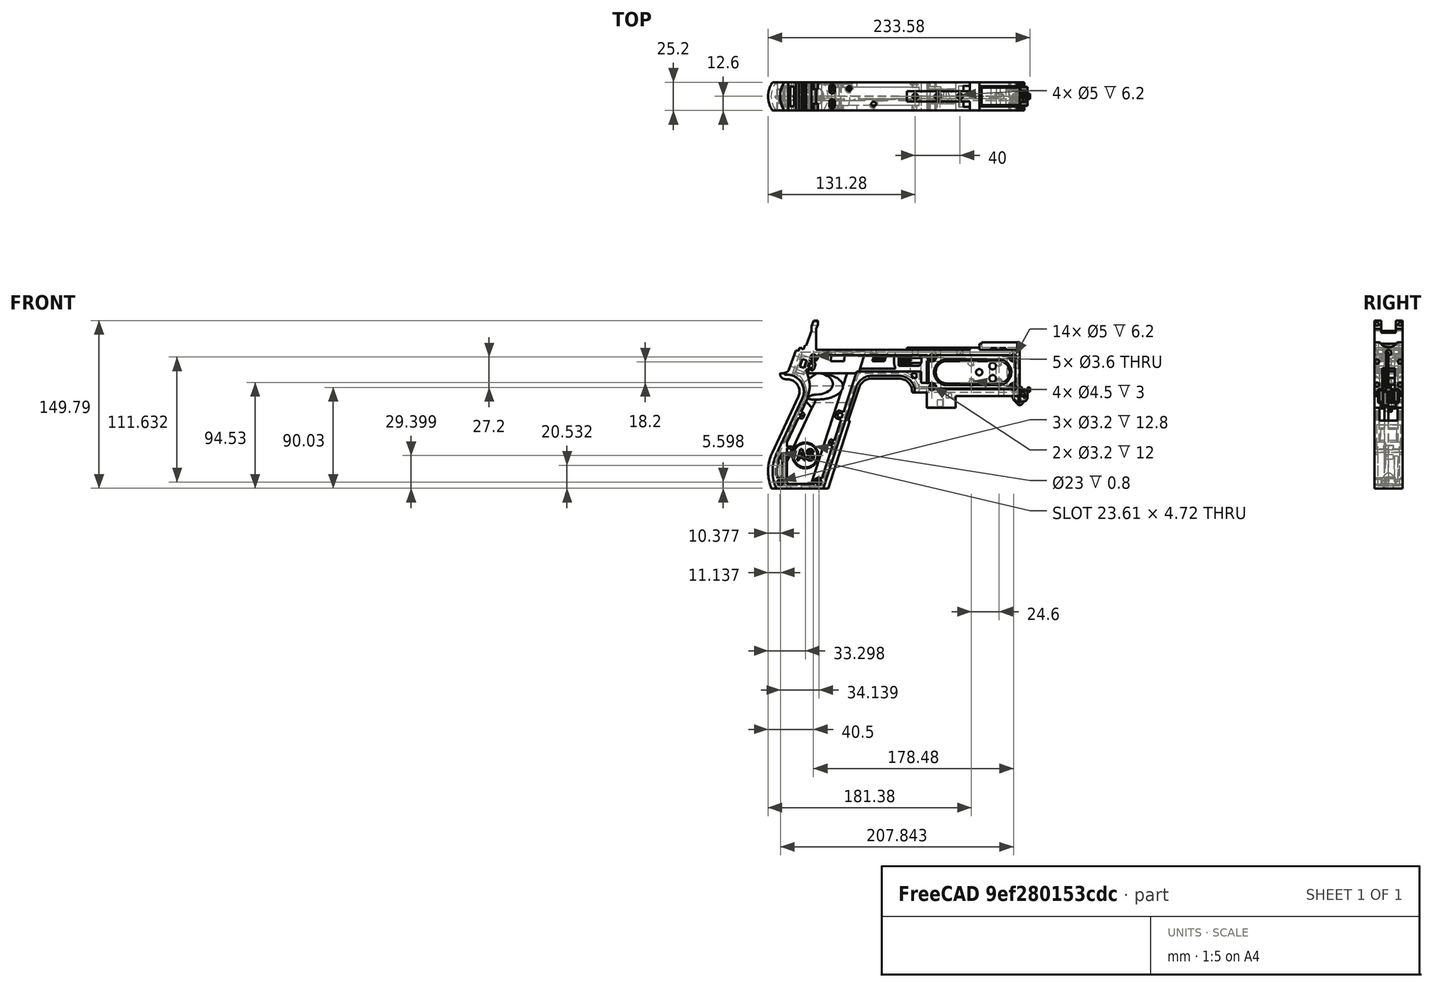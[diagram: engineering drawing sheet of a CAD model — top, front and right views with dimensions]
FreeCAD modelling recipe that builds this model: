
FCSTD DOCUMENT  (FreeCAD 1.0R39319 (Git))
Label: PICON-OF_ver_38
License: All rights reserved
LicenseURL: https://en.wikipedia.org/wiki/All_rights_reserved
objects: Sketcher::SketchObject×107, Part::Extrusion×50, Part::Cut×39, PartDesign::Pad×29, PartDesign::Pocket×18, PartDesign::Chamfer×15, PartDesign::Body×10, PartDesign::Fillet×6, PartDesign::SubtractivePipe×4, Part::Part2DObjectPython×4, PartDesign::SubtractiveLoft×4, PartDesign::Plane×2, PartDesign::SubShapeBinder×2, Part::Sweep×1, PartDesign::ShapeBinder×1, Part::MultiFuse×1, Mesh::Feature×1
note: 552 computed .brp shape members not serialized (recipe doc carries the construction recipe); baked Part::Feature solids carry a one-line shape summary decoded from their .brp

FEATURE [Sketcher::SketchObject] Sketch  label="corpo principale"
  ArcFitTolerance = 1e-06
  AttacherType = Attacher::AttachEngine3D
  AttachmentSupport = -> [XZ_Plane]
  FullyConstrained = true
  MakeInternals = false
  MapMode = 5
  Placement = pos=(0,0,0) rot=(1,0,0;1.5708rad)
  sketch-geometry (65):
    g0: LineSegment StartX=0 StartY=0 StartZ=0 EndX=-57.2 EndY=0 EndZ=0
    g1: LineSegment StartX=-57.2 StartY=0 StartZ=0 EndX=-57.2 EndY=-10.4 EndZ=0
    g2: LineSegment StartX=-57.2 StartY=-10.4 StartZ=0 EndX=-82.8 EndY=-10.4 EndZ=0
    g3: LineSegment StartX=-82.8 StartY=-10.4 StartZ=0 EndX=-82.8 EndY=3.2 EndZ=0
    g4: LineSegment StartX=-82.8 StartY=3.2 StartZ=0 EndX=-93.6 EndY=3.2 EndZ=0
    g5: LineSegment StartX=-93.6 StartY=3.2 StartZ=0 EndX=-93.6 EndY=4 EndZ=0
    g6: LineSegment StartX=-107.6 StartY=18 StartZ=0 EndX=-132.428 EndY=18 EndZ=0
    g7: LineSegment StartX=-145.743 StartY=8.32624 StartZ=0 EndX=-175.232 EndY=-82.4316 EndZ=0
    g8: LineSegment StartX=-175.232 StartY=-82.4316 StartZ=0 EndX=-217.232 EndY=-82.4316 EndZ=0
    g9: LineSegment StartX=-217.232 StartY=-52.1862 StartZ=0 EndX=-193.988 EndY=-2.33927 EndZ=0
    g10: LineSegment StartX=-206.196 StartY=23.0857 StartZ=0 EndX=-199.861 EndY=40.4914 EndZ=0
    g11: LineSegment StartX=-199.861 StartY=40.4914 StartZ=0 EndX=-197.061 EndY=40.4914 EndZ=0
    g12: LineSegment StartX=-197.061 StartY=40.4914 StartZ=0 EndX=-197.061 EndY=42.8914 EndZ=0
    g13: LineSegment StartX=-197.061 StartY=42.8914 StartZ=0 EndX=-194.261 EndY=42.8914 EndZ=0
    g14: LineSegment StartX=-194.261 StartY=42.8914 StartZ=0 EndX=-194.535 EndY=42.1397 EndZ=0
    g15: LineSegment StartX=-194.535 StartY=42.1397 StartZ=0 EndX=-193.031 EndY=41.5924 EndZ=0
    g16: LineSegment StartX=-193.031 StartY=41.5924 StartZ=0 EndX=-191.663 EndY=45.3512 EndZ=0
    g17: LineSegment StartX=-191.663 StartY=45.3512 StartZ=0 EndX=-190.536 EndY=44.9408 EndZ=0
    g18: LineSegment StartX=-190.536 StartY=44.9408 StartZ=0 EndX=-185.747 EndY=58.0965 EndZ=0
    g19: LineSegment StartX=-185.747 StartY=58.0965 StartZ=0 EndX=-185.747 EndY=62.0965 EndZ=0
    g20: LineSegment StartX=-185.747 StartY=62.0965 StartZ=0 EndX=-183.832 EndY=67.3588 EndZ=0
    g21: LineSegment StartX=-183.832 StartY=67.3588 StartZ=0 EndX=-180.232 EndY=67.3588 EndZ=0
    g22: LineSegment StartX=-180.232 StartY=67.3588 StartZ=0 EndX=-180.232 EndY=63.7588 EndZ=0
    g23: LineSegment StartX=-180.232 StartY=63.7588 StartZ=0 EndX=-181.6 EndY=60 EndZ=0
    g24: LineSegment StartX=-181.6 StartY=60 StartZ=0 EndX=-181.6 EndY=41.2 EndZ=0
    g25: LineSegment StartX=-181.6 StartY=41.2 StartZ=0 EndX=-100.8 EndY=41.2 EndZ=0
    g26: LineSegment StartX=-36 StartY=43.2 StartZ=0 EndX=-36 EndY=41.2 EndZ=0
    g27: LineSegment StartX=0 StartY=48 StartZ=0 EndX=0 EndY=0 EndZ=0
    g28: LineSegment StartX=-209.901 StartY=19.85 StartZ=0 EndX=-209.901 EndY=20.1 EndZ=0
    g29: LineSegment StartX=-208.001 StartY=22 StartZ=0 EndX=-207.747 EndY=22 EndZ=0
    g30: LineSegment StartX=-207.583 StartY=19 StartZ=0 EndX=-209.051 EndY=19 EndZ=0
    g31: ArcOfCircle CenterX=-208.001 CenterY=20.1 CenterZ=0 NormalX=0 NormalY=0 NormalZ=1 AngleXU=0 Radius=1.9 StartAngle=1.5708 EndAngle=3.14159
    g32: GeomPoint [constr] X=-209.901 Y=22 Z=0
    g33: ArcOfCircle CenterX=-209.051 CenterY=19.85 CenterZ=0 NormalX=0 NormalY=0 NormalZ=1 AngleXU=0 Radius=0.85 StartAngle=3.14159 EndAngle=4.71239
    g34: GeomPoint [constr] X=-209.901 Y=19 Z=0
    g35: ArcOfCircle CenterX=-207.747 CenterY=23.65 CenterZ=0 NormalX=0 NormalY=0 NormalZ=1 AngleXU=0 Radius=1.65 StartAngle=4.71239 EndAngle=5.93412
    g36: GeomPoint [constr] X=-206.591 Y=22 Z=0
    g37: LineSegment StartX=-4 StartY=6 StartZ=0 EndX=-4 EndY=36.4 EndZ=0
    g38: LineSegment StartX=-4 StartY=36.4 StartZ=0 EndX=-185.2 EndY=36.4 EndZ=0
    g39: LineSegment StartX=-185.2 StartY=36.4 StartZ=0 EndX=-190.441 EndY=22 EndZ=0
    g40: LineSegment StartX=-214.575 StartY=-78.4316 StartZ=0 EndX=-178.142 EndY=-78.4316 EndZ=0
    g41: LineSegment StartX=-178.142 StartY=-78.4316 StartZ=0 EndX=-145.51 EndY=22 EndZ=0
    g42: LineSegment StartX=-145.51 StartY=22 StartZ=0 EndX=-87.91 EndY=22 EndZ=0
    g43: LineSegment StartX=-87.91 StartY=22 StartZ=0 EndX=-87.91 EndY=11.6 EndZ=0
    g44: LineSegment StartX=-87.91 StartY=11.6 StartZ=0 EndX=-80.11 EndY=11.6 EndZ=0
    g45: LineSegment StartX=-80.11 StartY=11.6 StartZ=0 EndX=-80.11 EndY=6 EndZ=0
    g46: LineSegment StartX=-80.11 StartY=6 StartZ=0 EndX=-4 EndY=6 EndZ=0
    g47: LineSegment StartX=-190.363 StartY=-4.02975 StartZ=0 EndX=-213.607 EndY=-53.8767 EndZ=0
    g48: ArcOfCircle CenterX=-132.428 CenterY=4 CenterZ=0 NormalX=0 NormalY=0 NormalZ=1 AngleXU=0 Radius=14 StartAngle=1.5708 EndAngle=2.82743
    g49: GeomPoint [constr] X=-142.6 Y=18 Z=0
    g50: ArcOfCircle CenterX=-107.6 CenterY=4 CenterZ=0 NormalX=0 NormalY=0 NormalZ=1 AngleXU=0 Radius=14 StartAngle=0 EndAngle=1.5708
    g51: GeomPoint [constr] X=-93.6 Y=18 Z=0
    g52: ArcOfCircle CenterX=-184.801 CenterY=-67.3089 CenterZ=0 NormalX=0 NormalY=0 NormalZ=1 AngleXU=0 Radius=35.7833 StartAngle=2.70526 EndAngle=3.57792
    g53: ArcOfCircle CenterX=-207.583 CenterY=4 CenterZ=0 NormalX=0 NormalY=0 NormalZ=1 AngleXU=0 Radius=15 StartAngle=5.84685 EndAngle=7.85398
    g54: LineSegment [constr] StartX=-213.607 StartY=-53.8767 StartZ=0 EndX=-217.232 EndY=-52.1862 EndZ=0
    g55: ArcOfCircle CenterX=-184.801 CenterY=-67.3089 CenterZ=0 NormalX=0 NormalY=0 NormalZ=1 AngleXU=0 Radius=31.7833 StartAngle=2.70526 EndAngle=3.49911
    g56: ArcOfCircle CenterX=-218.095 CenterY=8.90192 CenterZ=0 NormalX=0 NormalY=0 NormalZ=1 AngleXU=0 Radius=30.5989 StartAngle=5.84685 EndAngle=6.72553
    g57: LineSegment StartX=-44.6 StartY=43.2 StartZ=0 EndX=-36 EndY=43.2 EndZ=0
    g58: LineSegment StartX=-100.8 StartY=41.2 StartZ=0 EndX=-44.6 EndY=41.2 EndZ=0
    g59: LineSegment StartX=-44.6 StartY=41.2 StartZ=0 EndX=-44.6 EndY=43.2 EndZ=0
    g60: LineSegment StartX=-2.4 StartY=48 StartZ=0 EndX=0 EndY=48 EndZ=0
    g61: LineSegment StartX=-36 StartY=41.2 StartZ=0 EndX=-2.4 EndY=41.2 EndZ=0
    g62: LineSegment StartX=-2.4 StartY=41.2 StartZ=0 EndX=-2.4 EndY=48 EndZ=0
    g63: LineSegment [constr] StartX=-181.6 StartY=36.4 StartZ=0 EndX=-152.209 EndY=36.4 EndZ=0
    g64: LineSegment [constr] StartX=-181.6 StartY=36.4 StartZ=0 EndX=-130.41 EndY=36.4 EndZ=0
  constraints (183):
    c: Coincident(g-1,g0)
    c: PointOnObject(g0,g-1)
    c: Coincident(g0,g1)
    c: Vertical(g1)
    c: Coincident(g1,g2)
    c: Horizontal(g2)
    c: Coincident(g2,g3)
    c: Vertical(g3)
    c: Coincident(g3,g4)
    c: Coincident(g4,g5)
    c: Vertical(g5)
    c: Horizontal(g6)
    c: Coincident(g7,g8)
    c: Horizontal(g8)
    c: Coincident(g10,g11)
    c: Horizontal(g11)
    c: Coincident(g11,g12)
    c: Vertical(g12)
    c: Coincident(g12,g13)
    c: Horizontal(g13)
    c: Coincident(g13,g14)
    c: Coincident(g14,g15)
    c: Coincident(g15,g16)
    c: Coincident(g16,g17)
    c: Coincident(g17,g18)
    c: Coincident(g18,g19)
    c: Vertical(g19)
    c: Coincident(g19,g20)
    c: Coincident(g20,g21)
    c: Horizontal(g21)
    c: Coincident(g21,g22)
    c: Vertical(g22)
    c: Coincident(g22,g23)
    c: Coincident(g23,g24)
    c: Vertical(g24)
    c: Coincident(g24,g25)
    c: Horizontal(g25)
    c: Coincident(g57,g26)
    c: Vertical(g26)
    c: Coincident(g26,g61)
    c: PointOnObject(g60,g-2)
    c: Coincident(g60,g27)
    c: Coincident(g27,g0)
    c: DistanceY(g27,g27) = 48
    c: DistanceY(g1,g1) = 10.4
    c: DistanceX(g0,g0) = 57.2
    c: DistanceX(g2,g2) = 25.6
    c: Horizontal(g4)
    c: DistanceY(g3,g3) = 13.6
    c: DistanceX(g4,g4) = 10.8
    c: DistanceY(g5,g51) = 14.8
    c: DistanceX(g49,g51) = 49
    c: Distance(g7,g49) = 105.6
    c: DistanceX(g61,g60) = 36
    c: DistanceX(g25,g25) = 80.8
    c: DistanceY(g24,g24) = 18.8
    c: DistanceY(g22,g22) = 3.6
    c: Distance(g23) = 4
    c: Angle(g-1,g23) = 1.22173
    c: DistanceX(g21,g21) = 3.6
    c: Distance(g20) = 5.6
    c: Angle(g-1,g20) = 1.22173
    c: DistanceY(g19,g19) = 4
    c: Distance(g18) = 14
    c: Angle(g-1,g18) = 1.22173
    c: Distance(g17) = 1.2
    c: Distance(g16) = 4
    c: Angle(g16) = 1.22173
    c: Perpendicular(g18,g17)
    c: Distance(g15) = 1.6
    c: Perpendicular(g16,g15)
    c: Distance(g14) = 0.8
    c: DistanceX(g13,g13) = 2.8
    c: Perpendicular(g15,g14)
    c: DistanceY(g12,g12) = 2.4
    c: DistanceX(g11,g11) = 2.8
    c: Distance(g9) = 55
    c: Angle(g9,g-1) = 2.00713
    c: Horizontal(g29)
    c: Vertical(g28)
    c: Horizontal(g30)
    c: PointOnObject(g32,g29)
    c: PointOnObject(g32,g28)
    c: Tangent(g29,g31) = 1.5708
    c: Tangent(g28,g31) = 1.5708
    c: PointOnObject(g34,g28)
    c: PointOnObject(g34,g30)
    c: Tangent(g28,g33) = 1.5708
    c: Tangent(g30,g33) = 1.5708
    c: PointOnObject(g36,g29)
    c: PointOnObject(g36,g10)
    c: Tangent(g29,g35) = -1.5708
    c: Tangent(g10,g35) = -1.5708
    c: Angle(g-1,g10) = 1.22173
    c: Radius(g35) = 1.65
    c: Vertical(g37)
    c: Coincident(g37,g38)
    c: Horizontal(g38)
    c: Coincident(g38,g39)
    c: Horizontal(g40)
    c: Coincident(g40,g41)
    c: Coincident(g41,g42)
    c: Horizontal(g42)
    c: Coincident(g42,g43)
    c: Vertical(g43)
    c: Coincident(g43,g44)
    c: Horizontal(g44)
    c: Coincident(g44,g45)
    c: Vertical(g45)
    c: Coincident(g45,g46)
    c: Coincident(g46,g37)
    c: Horizontal(g46)
    c: DistanceY(g0,g37) = 6
    c: DistanceX(g37,g0) = 4
    c: DistanceY(g37,g25) = 4.8
    c: DistanceX(g38,g38) = 181.2
    c: DistanceX(g42,g42) = 57.6
    c: DistanceY(g49,g41) = 4
    c: DistanceX(g41,g49) = 2.91
    c: DistanceY(g43,g43) = 10.4
    c: DistanceX(g44,g44) = 7.8
    c: DistanceY(g7,g40) = 4
    c: Distance(g47) = 55
    c: Angle(g-1,g39) = 1.22173
    c: PointOnObject(g49,g7)
    c: PointOnObject(g49,g6)
    c: Tangent(g7,g48) = -1.5708
    c: Tangent(g6,g48) = -1.5708
    c: PointOnObject(g51,g5)
    c: PointOnObject(g51,g6)
    c: Tangent(g5,g50) = -1.5708
    c: Tangent(g6,g50) = -1.5708
    c: Radius(g50) = 14
    c: Radius(g48) = 14
    c: DistanceX(g8,g8) = 42
    c: Angle(g7,g-1) = 1.88496
    c: Parallel(g41,g7)
    c: Parallel(g47,g9)
    c: Coincident(g52,g8)
    c: Tangent(g52,g9) = 1.5708
    c: DistanceX(g9,g8) = 0
    c: Tangent(g53,g9) = -1.5708
    c: Tangent(g53,g30) = -1.5708
    c: Diameter(g53) = 30
    c: DistanceY(g53,g0) = -4
    c: Coincident(g54,g47)
    c: Distance(g54) = 4
    c: Coincident(g54,g9)
    c: Coincident(g55,g40)
    c: Tangent(g55,g47) = -1.5708
    c: Coincident(g52,g55)
    c: Coincident(g56,g39)
    c: Tangent(g56,g47) = 1.5708
    c: Horizontal(g57)
    c: DistanceX(g57,g57) = 8.6
    c: Coincident(g58,g25)
    c: Horizontal(g58)
    c: Coincident(g59,g58)
    c: Vertical(g59)
    c: DistanceY(g58,g57) = 2
    c: DistanceX(g58,g58) = 56.2
    c: Coincident(g59,g57)
    c: DistanceY(g41,g36) = 0
    c: DistanceY(g36,g39) = 0
    c: DistanceY(g28,g28) = 0.25
    c: DistanceX(g30,g36) = 2.46
    c: DistanceX(g28,g29) = 1.9
    c: Coincident(g62,g60)
    c: Horizontal(g60)
    c: DistanceX(g62,g27) = 2.4
    c: Coincident(g61,g62)
    c: DistanceY(g26,g26) = 2
    c: Vertical(g62)
    c: DistanceY(g61,g60) = 6.8
    c: Horizontal(g61)
    c: Distance(g63) = 29.391
    c: PointOnObject(g63,g38)
    c: PointOnObject(g63,g38)
    c: Distance(g64) = 51.19
    c: PointOnObject(g64,g38)
    c: PointOnObject(g64,g38)
    c: DistanceX(g24,g63) = 0
    c: DistanceX(g24,g64) = 0
FEATURE [Part::Extrusion] Extrude  label="Extrude corpo principale"
  Base = -> Sketch
  Dir = (0,-1,2e-16)
  DirMode = 2
  FaceMakerClass = Part::FaceMakerBullseye
  FaceMakerMode = 3
  LengthFwd = 25.2
  LengthRev = 12.6
  Solid = true
  Symmetric = true
FEATURE [Sketcher::SketchObject] Sketch002  label="scavo grilletto"
  ArcFitTolerance = 1e-06
  AttachmentSupport = -> [XZ_Plane]
  ExternalGeometry = -> [Sketch]
  FullyConstrained = true
  MakeInternals = false
  MapMode = 5
  Placement = pos=(0,0,0) rot=(1,0,0;1.5708rad)
  sketch-geometry (4):
    g0: LineSegment StartX=-89.51 StartY=22 StartZ=0 EndX=-152.71 EndY=22 EndZ=0
    g1: LineSegment StartX=-152.71 StartY=22 StartZ=0 EndX=-167.006 EndY=-22 EndZ=0
    g2: LineSegment StartX=-167.006 StartY=-22 StartZ=0 EndX=-89.51 EndY=-22 EndZ=0
    g3: LineSegment StartX=-89.51 StartY=-22 StartZ=0 EndX=-89.51 EndY=22 EndZ=0
  constraints (12):
    c: Horizontal(g0)
    c: Coincident(g0,g1)
    c: Coincident(g1,g2)
    c: Horizontal(g2)
    c: Coincident(g2,g3)
    c: Coincident(g3,g0)
    c: Vertical(g3)
    c: Angle(g1,g0) = 1.88496
    c: DistanceY(g3,g3) = 44
    c: DistanceX(g0,g0) = 63.2
    c: DistanceX(g0,g-3) = 1.6
    c: DistanceY(g-3,g0) = 0
FEATURE [Sketcher::SketchObject] Sketch004  label="traiettoria arrotondamento impugnatura anteriore"
  ArcFitTolerance = 1e-06
  AttachmentSupport = -> [XZ_Plane]
  ExternalGeometry = -> [Sketch]
  FullyConstrained = true
  MakeInternals = false
  MapMode = 5
  Placement = pos=(0,0,0) rot=(1,0,0;1.5708rad)
  sketch-geometry (13):
    g0: LineSegment StartX=-175.232 StartY=-82.4316 StartZ=0 EndX=-145.743 EndY=8.32624 EndZ=0
    g1: LineSegment StartX=-93.6 StartY=3.2 StartZ=0 EndX=-93.6 EndY=4 EndZ=0
    g2: LineSegment StartX=-132.428 StartY=18 StartZ=0 EndX=-107.6 EndY=18 EndZ=0
    g3: ArcOfCircle CenterX=-132.428 CenterY=4 CenterZ=0 NormalX=0 NormalY=0 NormalZ=1 AngleXU=0 Radius=14 StartAngle=1.5708 EndAngle=2.82743
    g4: ArcOfCircle CenterX=-107.6 CenterY=4 CenterZ=0 NormalX=0 NormalY=0 NormalZ=1 AngleXU=0 Radius=14 StartAngle=0 EndAngle=1.5708
    g5: LineSegment StartX=-175.232 StartY=-82.4316 StartZ=0 EndX=-217.232 EndY=-82.4316 EndZ=0
    g6: LineSegment StartX=-217.232 StartY=-52.1862 StartZ=0 EndX=-193.988 EndY=-2.33927 EndZ=0
    g7: LineSegment StartX=-209.051 StartY=19 StartZ=0 EndX=-207.583 EndY=19 EndZ=0
    g8: LineSegment StartX=-209.901 StartY=20.1 StartZ=0 EndX=-209.901 EndY=19.85 EndZ=0
    g9: ArcOfCircle CenterX=-184.801 CenterY=-67.3089 CenterZ=0 NormalX=0 NormalY=0 NormalZ=1 AngleXU=0 Radius=35.7833 StartAngle=2.70526 EndAngle=3.57792
    g10: ArcOfCircle CenterX=-207.583 CenterY=4 CenterZ=0 NormalX=0 NormalY=0 NormalZ=1 AngleXU=0 Radius=15 StartAngle=5.84685 EndAngle=7.85398
    g11: ArcOfCircle CenterX=-209.051 CenterY=19.85 CenterZ=0 NormalX=0 NormalY=0 NormalZ=1 AngleXU=0 Radius=0.85 StartAngle=3.14159 EndAngle=4.71239
    g12: ArcOfCircle CenterX=-208.001 CenterY=20.1 CenterZ=0 NormalX=0 NormalY=0 NormalZ=1 AngleXU=0 Radius=1.9 StartAngle=1.5708 EndAngle=3.14159
  constraints (26):
    c: Coincident(g0,g-3)
    c: Coincident(g0,g-6)
    c: Coincident(g1,g-8)
    c: Coincident(g1,g-7)
    c: Coincident(g2,g-5)
    c: Coincident(g2,g-4)
    c: Coincident(g3,g2)
    c: Tangent(g3,g0) = 1.5708
    c: Coincident(g4,g1)
    c: Tangent(g4,g2) = 1.5708
    c: Coincident(g5,g0)
    c: Coincident(g5,g-9)
    c: Coincident(g6,g-12)
    c: Coincident(g6,g-11)
    c: Coincident(g7,g-15)
    c: Coincident(g7,g-14)
    c: Coincident(g8,g-16)
    c: Coincident(g8,g-17)
    c: Tangent(g9,g6) = 1.5708
    c: Coincident(g9,g5)
    c: Coincident(g10,g7)
    c: Tangent(g10,g6) = -1.5708
    c: Tangent(g11,g7) = -1.5708
    c: Coincident(g11,g8)
    c: Tangent(g12,g8) = -1.5708
    c: Coincident(g12,g-17)
FEATURE [PartDesign::Plane] DatumPlane  label="Piano per disegno arrotondamento impugnatura"
  AttachmentSupport = -> [Sketch]
  Length = 68.5841
  MapMode = 7
  Placement = pos=(-145.743,1.8e-15,8.32624) rot=(0.154555,0.154555,0.97582;1.59527rad)
  ResizeMode = 0
  Width = 191.269
FEATURE [Sketcher::SketchObject] Sketch005  label="forma arrotondamento impugnatura anteriore"
  ArcFitTolerance = 1e-06
  AttachmentSupport = -> [DatumPlane]
  FullyConstrained = true
  MakeInternals = false
  MapMode = 5
  Placement = pos=(-145.743,1.8e-15,8.32624) rot=(0.154555,0.154555,0.97582;1.59527rad)
  sketch-geometry (5):
    g0: GeomPoint [constr] X=0 Y=-4 Z=0
    g1: GeomPoint [constr] X=-12.6 Y=7.1e-15 Z=0
    g2: GeomPoint [constr] X=12.6 Y=4.97e-14 Z=0
    g3: LineSegment StartX=-12.6 StartY=7.1e-15 StartZ=0 EndX=12.6 EndY=4.97e-14 EndZ=0
    g4: ArcOfCircle CenterX=-3.88e-14 CenterY=17.845 CenterZ=0 NormalX=0 NormalY=0 NormalZ=1 AngleXU=0 Radius=21.845 StartAngle=4.09759 EndAngle=5.32718
  constraints (11):
    c: DistanceY(g0,g-1) = 4
    c: DistanceX(g-1,g0) = 0
    c: DistanceX(g1,g-1) = 12.6
    c: DistanceX(g-1,g2) = 12.6
    c: DistanceY(g-1,g2) = 0
    c: DistanceY(g-1,g1) = 0
    c: Coincident(g3,g1)
    c: Coincident(g3,g2)
    c: Coincident(g4,g1)
    c: Coincident(g4,g2)
    c: PointOnObject(g0,g4)
FEATURE [Part::Sweep] Sweep  label="Sweep impugnatura"
  Frenet = true
  Sections = -> [Sketch005]
  Solid = true
  Spine = -> Sketch [Edge32,Edge33,Edge34,Edge35,Edge36,Edge37,Edge38,Edge39,Edge40,Edge41,Edge42,Edge43,Edge44]
  Transition = 1
FEATURE [Sketcher::SketchObject] Sketch008  label="buchi e pulizie varie"
  ArcFitTolerance = 1e-06
  AttachmentSupport = -> [XZ_Plane]
  ExternalGeometry = -> [Sketch]
  FullyConstrained = true
  MakeInternals = false
  MapMode = 5
  Placement = pos=(0,0,0) rot=(1,0,0;1.5708rad)
  sketch-geometry (26):
    g0: LineSegment StartX=-96.278 StartY=20.155 StartZ=0 EndX=-92.278 EndY=20.155 EndZ=0
    g1: LineSegment StartX=-92.278 StartY=20.155 StartZ=0 EndX=-92.278 EndY=16.155 EndZ=0
    g2: LineSegment StartX=-92.278 StartY=16.155 StartZ=0 EndX=-96.278 EndY=16.155 EndZ=0
    g3: LineSegment StartX=-96.278 StartY=16.155 StartZ=0 EndX=-96.278 EndY=20.155 EndZ=0
    g4: LineSegment StartX=-222.232 StartY=-82.4316 StartZ=0 EndX=-170.232 EndY=-82.4316 EndZ=0
    g5: LineSegment StartX=-170.232 StartY=-82.4316 StartZ=0 EndX=-170.232 EndY=-86.4316 EndZ=0
    g6: LineSegment StartX=-170.232 StartY=-86.4316 StartZ=0 EndX=-222.232 EndY=-86.4316 EndZ=0
    g7: LineSegment StartX=-222.232 StartY=-86.4316 StartZ=0 EndX=-222.232 EndY=-82.4316 EndZ=0
    g8: LineSegment StartX=-213.901 StartY=20.1 StartZ=0 EndX=-213.901 EndY=26 EndZ=0
    g9: LineSegment StartX=-213.901 StartY=26 StartZ=0 EndX=-206.196 EndY=26 EndZ=0
    g10: LineSegment StartX=-17.4 StartY=42.8 StartZ=0 EndX=-12.4 EndY=42.8 EndZ=0
    g11: LineSegment StartX=-12.4 StartY=42.8 StartZ=0 EndX=-12.4 EndY=41.2 EndZ=0
    g12: LineSegment StartX=-12.4 StartY=41.2 StartZ=0 EndX=-17.4 EndY=41.2 EndZ=0
    g13: LineSegment StartX=-17.4 StartY=41.2 StartZ=0 EndX=-17.4 EndY=42.8 EndZ=0
    g14: LineSegment StartX=-25.9 StartY=42.8 StartZ=0 EndX=-20.9 EndY=42.8 EndZ=0
    g15: LineSegment StartX=-20.9 StartY=42.8 StartZ=0 EndX=-20.9 EndY=41.2 EndZ=0
    g16: LineSegment StartX=-20.9 StartY=41.2 StartZ=0 EndX=-25.9 EndY=41.2 EndZ=0
    g17: LineSegment StartX=-25.9 StartY=41.2 StartZ=0 EndX=-25.9 EndY=42.8 EndZ=0
    g18: GeomPoint [constr] X=-206.196 Y=23.0857 Z=0
    g19: GeomPoint [constr] X=-213.901 Y=20.1 Z=0
    g20: BSplineCurve PolesCount=4 KnotsCount=2 Degree=3 IsPeriodic=0
    g21-g24: Circle [constr] x4 (B-spline internal-alignment scaffolding for g20; pole/knot coordinates omitted)
    g25: LineSegment StartX=-206.196 StartY=26 StartZ=0 EndX=-206.196 EndY=23.0857 EndZ=0
  constraints (73):
    c: Horizontal(g0)
    c: Coincident(g1,g0)
    c: Vertical(g1)
    c: Coincident(g2,g1)
    c: Horizontal(g2)
    c: Coincident(g3,g2)
    c: Coincident(g3,g0)
    c: Vertical(g3)
    c: DistanceX(g0,g-4) = 4.368
    c: DistanceY(g0,g-4) = 1.845
    c: DistanceY(g1,g1) = 4
    c: DistanceX(g2,g2) = 4
    c: Horizontal(g4)
    c: Coincident(g5,g4)
    c: Vertical(g5)
    c: Coincident(g6,g5)
    c: Horizontal(g6)
    c: Coincident(g7,g6)
    c: Coincident(g7,g4)
    c: Vertical(g7)
    c: DistanceY(g7,g7) = 4
    c: DistanceX(g4,g-5) = 5
    c: DistanceX(g-5,g4) = 5
    c: DistanceY(g4,g-5) = 0
    c: Coincident(g9,g8)
    c: Parallel(g9,g-6)
    c: DistanceX(g8,g-8) = 4
    c: Horizontal(g10)
    c: Coincident(g11,g10)
    c: Vertical(g11)
    c: Coincident(g12,g11)
    c: Horizontal(g12)
    c: Coincident(g13,g12)
    c: Coincident(g13,g10)
    c: Vertical(g13)
    c: Horizontal(g14)
    c: Coincident(g15,g14)
    c: Vertical(g15)
    c: Coincident(g16,g15)
    c: Horizontal(g16)
    c: Coincident(g17,g16)
    c: Coincident(g17,g14)
    c: Vertical(g17)
    c: DistanceY(g11,g10) = 1.6
    c: DistanceX(g10,g10) = 5
    c: DistanceY(g15,g14) = 1.6
    c: DistanceX(g14,g14) = 5
    c: DistanceX(g15,g12) = 3.5
    c: DistanceX(g11,g-9) = 10
    c: DistanceY(g-9,g11) = 0
    c: DistanceY(g-9,g15) = 0
    c: Perpendicular(g8,g9)
    c: DistanceY(g-7,g9) = 4
    c: DistanceY(g8,g-8) = 0
    c: InternalAlignment(g18,g20)
    c: InternalAlignment(g19,g20)
    c: InternalAlignment(g21,g20)
    c: Weight(g21) = 1
    c: InternalAlignment(g22,g20)
    c: Equal(g22,g21)
    c: InternalAlignment(g23,g20)
    c: Equal(g23,g21)
    c: InternalAlignment(g24,g20)
    c: Equal(g24,g21)
    c: Coincident(g18,g-12)
    c: Coincident(g19,g8)
    c: Coincident(g25,g9)
    c: Coincident(g25,g20)
    c: Vertical(g25)
    c: DistanceY(g20,g23) = 0
    c: DistanceY(g22,g18) = 2.26
    c: DistanceX(g22,g18) = 0.93
    c: DistanceX(g20,g23) = 2.9
FEATURE [Part::Extrusion] Extrude004  label="Extrude Buchi e pulizie varie"
  Base = -> Sketch008
  Dir = (0,-1,2e-16)
  DirMode = 2
  FaceMakerClass = Part::FaceMakerBullseye
  FaceMakerMode = 3
  LengthFwd = 25.2
  LengthRev = 0
  Solid = true
  Symmetric = true
FEATURE [Sketcher::SketchObject] Sketch009  label="rinforzi"
  ArcFitTolerance = 1e-06
  AttachmentSupport = -> [XZ_Plane]
  ExternalGeometry = -> [Sketch]
  FullyConstrained = true
  MakeInternals = false
  MapMode = 5
  Placement = pos=(0,0,0) rot=(1,0,0;1.5708rad)
  sketch-geometry (9):
    g0: LineSegment StartX=-87.91 StartY=22 StartZ=0 EndX=-87.91 EndY=36.4 EndZ=0
    g1: LineSegment StartX=-87.91 StartY=36.4 StartZ=0 EndX=-97.91 EndY=36.4 EndZ=0
    g2: LineSegment StartX=-97.91 StartY=36.4 StartZ=0 EndX=-97.91 EndY=22 EndZ=0
    g3: LineSegment StartX=-97.91 StartY=22 StartZ=0 EndX=-87.91 EndY=22 EndZ=0
    g4: LineSegment StartX=-149.713 StartY=9.06563 StartZ=0 EndX=-154.586 EndY=-5.93437 EndZ=0
    g5: LineSegment StartX=-154.586 StartY=-5.93437 StartZ=0 EndX=-191.863 EndY=-5.93437 EndZ=0
    g6: LineSegment StartX=-191.863 StartY=-5.93437 StartZ=0 EndX=-191.863 EndY=9.06563 EndZ=0
    g7: LineSegment StartX=-191.863 StartY=9.06563 StartZ=0 EndX=-149.713 EndY=9.06563 EndZ=0
    g8: LineSegment [constr] StartX=-145.51 StartY=22 StartZ=0 EndX=-149.713 EndY=9.06563 EndZ=0
  constraints (25):
    c: Vertical(g0)
    c: Coincident(g1,g0)
    c: Horizontal(g1)
    c: Coincident(g2,g1)
    c: Vertical(g2)
    c: Coincident(g3,g2)
    c: Coincident(g3,g0)
    c: Horizontal(g3)
    c: Coincident(g0,g-4)
    c: DistanceX(g3,g3) = 10
    c: DistanceY(g0,g-3) = 0
    c: Coincident(g5,g4)
    c: Horizontal(g5)
    c: Coincident(g6,g5)
    c: Vertical(g6)
    c: Coincident(g7,g6)
    c: Coincident(g7,g4)
    c: Horizontal(g7)
    c: Distance(g8) = 13.6
    c: Parallel(g-6,g8)
    c: Coincident(g-6,g8)
    c: Parallel(g4,g-6)
    c: DistanceY(g4,g4) = 15
    c: Coincident(g4,g8)
    c: DistanceX(g-5,g5) = -1.5
FEATURE [Part::Extrusion] Extrude001  label="Extrude scavo grilletto"
  Base = -> Sketch002
  Dir = (0,-1,2e-16)
  DirMode = 2
  FaceMakerClass = Part::FaceMakerBullseye
  FaceMakerMode = 3
  LengthFwd = 16
  LengthRev = 0
  Solid = true
  Symmetric = true
FEATURE [Part::Extrusion] Extrude005  label="Extrude Rinforzi"
  Base = -> Sketch009
  Dir = (0,-1,2e-16)
  DirMode = 2
  FaceMakerClass = Part::FaceMakerBullseye
  FaceMakerMode = 3
  LengthFwd = 2
  LengthRev = 0
  Placement = pos=(0,12.6,0) rot=(0,0,1;0rad)
  Solid = true
  Symmetric = false
FEATURE [PartDesign::ShapeBinder] CopyCut
  TraceSupport = false
FEATURE [PartDesign::Plane] DatumPlane001
  AttachmentSupport = -> [CopyCut]
  Length = 60
  MapMode = 5
  Placement = pos=(0,12.6,0) rot=(0,0.707107,0.707107;3.14159rad)
  ResizeMode = 0
  Width = 60
FEATURE [Sketcher::SketchObject] Sketch010  label="buco neopixel"
  ArcFitTolerance = 1e-06
  AttachmentSupport = -> [XZ_Plane]
  ExternalGeometry = -> [Sketch]
  FullyConstrained = true
  MakeInternals = false
  MapMode = 5
  Placement = pos=(0,0,0) rot=(1,0,0;1.5708rad)
  sketch-geometry (5):
    g0: LineSegment [constr] StartX=-199.861 StartY=40.4914 StartZ=0 EndX=-201.368 EndY=36.3521 EndZ=0
    g1: LineSegment StartX=-201.368 StartY=36.3521 StartZ=0 EndX=-204.932 EndY=26.5605 EndZ=0
    g2: LineSegment StartX=-201.368 StartY=36.3521 StartZ=0 EndX=-180.2 EndY=28.6477 EndZ=0
    g3: LineSegment StartX=-180.2 StartY=28.6477 StartZ=0 EndX=-183.764 EndY=18.8561 EndZ=0
    g4: LineSegment StartX=-183.764 StartY=18.8561 StartZ=0 EndX=-204.932 EndY=26.5605 EndZ=0
  constraints (14):
    c: Parallel(g0,g-3)
    c: Distance(g0) = 4.405
    c: Coincident(g0,g-3)
    c: Coincident(g2,g1)
    c: Coincident(g3,g2)
    c: Coincident(g4,g3)
    c: Coincident(g4,g1)
    c: Parallel(g1,g-3)
    c: Distance(g1) = 10.42
    c: Coincident(g1,g0)
    c: Parallel(g2,g4)
    c: Perpendicular(g1,g2)
    c: DistanceX(g-4,g2) = 5
    c: Parallel(g3,g1)
FEATURE [Part::Extrusion] Extrude006  label="Extrude buco neopixel"
  Base = -> Sketch010
  Dir = (0,-1,2e-16)
  DirMode = 2
  FaceMakerClass = Part::FaceMakerBullseye
  FaceMakerMode = 3
  LengthFwd = 17.2
  LengthRev = 0
  Solid = true
  Symmetric = true
FEATURE [Sketcher::SketchObject] Sketch011  label="fermo grilletto"
  ArcFitTolerance = 1e-06
  AttachmentSupport = -> [XZ_Plane]
  ExternalGeometry = -> [Sketch]
  FullyConstrained = true
  MakeInternals = false
  MapMode = 5
  Placement = pos=(0,0,0) rot=(1,0,0;1.5708rad)
  sketch-geometry (18):
    g0: LineSegment [constr] StartX=-145.51 StartY=22 StartZ=0 EndX=-157.347 EndY=-14.4293 EndZ=0
    g1: LineSegment [constr] StartX=-157.347 StartY=-14.4293 StartZ=0 EndX=-157.841 EndY=-15.951 EndZ=0
    g2: LineSegment StartX=-161.151 StartY=-13.1932 StartZ=0 EndX=-155.825 EndY=-14.9237 EndZ=0
    g3: LineSegment StartX=-163.167 StartY=-14.2205 StartZ=0 EndX=-164.403 EndY=-18.0247 EndZ=0
    g4: LineSegment StartX=-163.376 StartY=-20.0408 StartZ=0 EndX=-158.05 EndY=-21.7713 EndZ=0
    g5: LineSegment StartX=-158.05 StartY=-21.7713 StartZ=0 EndX=-155.825 EndY=-14.9237 EndZ=0
    g6: LineSegment StartX=-161.645 StartY=-14.7149 StartZ=0 EndX=-157.841 EndY=-15.951 EndZ=0
    g7: LineSegment StartX=-157.841 StartY=-15.951 StartZ=0 EndX=-159.077 EndY=-19.7552 EndZ=0
    g8: LineSegment StartX=-159.077 StartY=-19.7552 StartZ=0 EndX=-162.881 EndY=-18.5191 EndZ=0
    g9: LineSegment StartX=-162.881 StartY=-18.5191 StartZ=0 EndX=-161.645 EndY=-14.7149 EndZ=0
    g10: LineSegment [constr] StartX=-161.645 StartY=-14.7149 StartZ=0 EndX=-161.151 EndY=-13.1932 EndZ=0
    g11: LineSegment [constr] StartX=-159.077 StartY=-19.7552 StartZ=0 EndX=-157.555 EndY=-20.2496 EndZ=0
    g12: LineSegment [constr] StartX=-159.077 StartY=-19.7552 StartZ=0 EndX=-159.572 EndY=-21.2769 EndZ=0
    g13: LineSegment [constr] StartX=-161.645 StartY=-14.7149 StartZ=0 EndX=-163.167 EndY=-14.2205 EndZ=0
    g14: ArcOfCircle CenterX=-161.645 CenterY=-14.7149 CenterZ=0 NormalX=0 NormalY=0 NormalZ=1 AngleXU=0 Radius=1.6 StartAngle=1.25664 EndAngle=2.82743
    g15: GeomPoint [constr] X=-162.673 Y=-12.6988 Z=0
    g16: ArcOfCircle CenterX=-162.881 CenterY=-18.5191 CenterZ=0 NormalX=0 NormalY=0 NormalZ=1 AngleXU=0 Radius=1.6 StartAngle=2.82743 EndAngle=4.39823
    g17: GeomPoint [constr] X=-164.897 Y=-19.5464 Z=0
  constraints (48):
    c: Parallel(g0,g-3)
    c: Distance(g0) = 38.304
    c: Coincident(g0,g-3)
    c: Parallel(g1,g-3)
    c: Distance(g1) = 1.6
    c: Coincident(g1,g0)
    c: Coincident(g5,g4)
    c: Coincident(g5,g2)
    c: Coincident(g7,g6)
    c: Coincident(g8,g7)
    c: Coincident(g9,g8)
    c: Coincident(g9,g6)
    c: Parallel(g7,g-3)
    c: Parallel(g9,g7)
    c: Perpendicular(g6,g7)
    c: Parallel(g6,g8)
    c: Distance(g6) = 4
    c: Distance(g9) = 4
    c: Parallel(g5,g7)
    c: Parallel(g9,g3)
    c: Parallel(g2,g6)
    c: Parallel(g4,g8)
    c: Parallel(g13,g6)
    c: Parallel(g10,g9)
    c: Parallel(g11,g8)
    c: Parallel(g12,g7)
    c: Distance(g10) = 1.6
    c: Distance(g13) = 1.6
    c: Distance(g12) = 1.6
    c: Distance(g11) = 1.6
    c: Coincident(g10,g6)
    c: Coincident(g13,g6)
    c: Coincident(g12,g7)
    c: Coincident(g11,g7)
    c: Distance(g10,g15) = 1.6
    c: Distance(g15,g13) = 1.6
    c: Distance(g4,g12) = 1.6
    c: Distance(g4,g11) = 1.6
    c: PointOnObject(g15,g2)
    c: Tangent(g3,g14) = -1.5708
    c: Tangent(g2,g14) = 1.5708
    c: PointOnObject(g17,g4)
    c: PointOnObject(g17,g3)
    c: Tangent(g4,g16) = -1.5708
    c: Tangent(g3,g16) = -1.5708
    c: Equal(g16,g14)
    c: Coincident(g16,g8)
    c: Coincident(g6,g1)
FEATURE [Part::Extrusion] Extrude007  label="Extrude fermo grilletto"
  Base = -> Sketch011
  Dir = (0,-1,2e-16)
  DirMode = 2
  FaceMakerClass = Part::FaceMakerBullseye
  FaceMakerMode = 3
  LengthFwd = 25.2
  LengthRev = 0
  Solid = true
  Symmetric = true
FEATURE [Sketcher::SketchObject] Sketch012  label="buco oled"
  ArcFitTolerance = 1e-06
  AttachmentSupport = -> [XZ_Plane]
  ExternalGeometry = -> [Sketch]
  FullyConstrained = true
  MakeInternals = false
  MapMode = 5
  Placement = pos=(0,0,0) rot=(1,0,0;1.5708rad)
  sketch-geometry (4):
    g0: LineSegment StartX=-185.747 StartY=58.0965 StartZ=0 EndX=-180.232 EndY=56.0891 EndZ=0
    g1: LineSegment StartX=-185.747 StartY=58.0965 StartZ=0 EndX=-185.747 EndY=67.3588 EndZ=0
    g2: LineSegment StartX=-185.747 StartY=67.3588 StartZ=0 EndX=-180.232 EndY=67.3588 EndZ=0
    g3: LineSegment StartX=-180.232 StartY=67.3588 StartZ=0 EndX=-180.232 EndY=56.0891 EndZ=0
  constraints (10):
    c: Coincident(g1,g0)
    c: Coincident(g2,g1)
    c: Coincident(g3,g2)
    c: Coincident(g3,g0)
    c: Parallel(g1,g-5)
    c: Perpendicular(g-3,g0)
    c: Parallel(g2,g-6)
    c: Parallel(g3,g-4)
    c: Coincident(g0,g-5)
    c: Coincident(g2,g-6)
FEATURE [Part::Extrusion] Extrude008  label="Extrude buco oled"
  Base = -> Sketch012
  Dir = (0,-1,2e-16)
  DirMode = 2
  FaceMakerClass = Part::FaceMakerBullseye
  FaceMakerMode = 3
  LengthFwd = 12.8
  LengthRev = 0
  Solid = true
  Symmetric = true
FEATURE [Sketcher::SketchObject] Sketch013  label="buco pompa"
  ArcFitTolerance = 1e-06
  AttachmentSupport = -> [XZ_Plane]
  ExternalGeometry = -> [Sketch]
  FullyConstrained = true
  MakeInternals = false
  MapMode = 5
  Placement = pos=(0,0,0) rot=(1,0,0;1.5708rad)
  sketch-geometry (8):
    g0: LineSegment StartX=-82.8 StartY=-10.4 StartZ=0 EndX=-82.8 EndY=-9.6 EndZ=0
    g1: LineSegment StartX=-82.8 StartY=-9.6 StartZ=0 EndX=-67.9 EndY=-9.6 EndZ=0
    g2: LineSegment StartX=-67.9 StartY=-9.6 StartZ=0 EndX=-67.9 EndY=6 EndZ=0
    g3: LineSegment StartX=-67.9 StartY=6 StartZ=0 EndX=-65.9 EndY=6 EndZ=0
    g4: LineSegment StartX=-65.9 StartY=6 StartZ=0 EndX=-65.9 EndY=-1.7 EndZ=0
    g5: LineSegment StartX=-65.9 StartY=-1.7 StartZ=0 EndX=-57.2 EndY=-1.7 EndZ=0
    g6: LineSegment StartX=-57.2 StartY=-1.7 StartZ=0 EndX=-57.2 EndY=-10.4 EndZ=0
    g7: LineSegment StartX=-57.2 StartY=-10.4 StartZ=0 EndX=-82.8 EndY=-10.4 EndZ=0
  constraints (22):
    c: Vertical(g0)
    c: Coincident(g1,g0)
    c: Horizontal(g1)
    c: Coincident(g2,g1)
    c: Vertical(g2)
    c: Coincident(g3,g2)
    c: Horizontal(g3)
    c: Coincident(g4,g3)
    c: Vertical(g4)
    c: Coincident(g5,g4)
    c: Horizontal(g5)
    c: Coincident(g6,g5)
    c: Vertical(g6)
    c: Coincident(g7,g6)
    c: Coincident(g7,g0)
    c: DistanceY(g0,g0) = 0.8
    c: DistanceY(g6,g6) = 8.7
    c: DistanceX(g1,g1) = 14.9
    c: DistanceX(g3,g3) = 2
    c: Coincident(g0,g-4)
    c: DistanceY(g2,g-6) = 0
    c: Coincident(g6,g-5)
FEATURE [Part::Extrusion] Extrude009  label="Extrude buco pompa"
  Base = -> Sketch013
  Dir = (0,-1,2e-16)
  DirMode = 2
  FaceMakerClass = Part::FaceMakerBullseye
  FaceMakerMode = 3
  LengthFwd = 13.2
  LengthRev = 0
  Solid = true
  Symmetric = true
FEATURE [Sketcher::SketchObject] Sketch014  label="buco frontale"
  ArcFitTolerance = 1e-06
  AttachmentSupport = -> [XZ_Plane]
  ExternalGeometry = -> [Sketch]
  FullyConstrained = true
  MakeInternals = false
  MapMode = 5
  Placement = pos=(0,0,0) rot=(1,0,0;1.5708rad)
  sketch-geometry (10):
    g0: LineSegment StartX=0 StartY=0 StartZ=0 EndX=0 EndY=24.671 EndZ=0
    g1: LineSegment StartX=0 StartY=24.671 StartZ=0 EndX=-4 EndY=24.671 EndZ=0
    g2: LineSegment StartX=-4 StartY=24.671 StartZ=0 EndX=-4 EndY=16 EndZ=0
    g3: LineSegment StartX=-4 StartY=16 StartZ=0 EndX=-2.4 EndY=16 EndZ=0
    g4: LineSegment StartX=-2.4 StartY=16 StartZ=0 EndX=-2.4 EndY=10 EndZ=0
    g5: LineSegment StartX=-2.4 StartY=10 StartZ=0 EndX=-12 EndY=10 EndZ=0
    g6: LineSegment StartX=-12 StartY=10 StartZ=0 EndX=-12 EndY=6 EndZ=0
    g7: LineSegment StartX=-12 StartY=6 StartZ=0 EndX=-2.4 EndY=6 EndZ=0
    g8: LineSegment StartX=-2.4 StartY=6 StartZ=0 EndX=-2.4 EndY=0 EndZ=0
    g9: LineSegment StartX=-2.4 StartY=0 StartZ=0 EndX=0 EndY=0 EndZ=0
  constraints (29):
    c: Vertical(g0)
    c: Coincident(g1,g0)
    c: Horizontal(g1)
    c: Coincident(g2,g1)
    c: Vertical(g2)
    c: Coincident(g3,g2)
    c: Horizontal(g3)
    c: Coincident(g4,g3)
    c: Vertical(g4)
    c: Coincident(g5,g4)
    c: Horizontal(g5)
    c: Coincident(g6,g5)
    c: Vertical(g6)
    c: Coincident(g7,g6)
    c: Coincident(g8,g7)
    c: Vertical(g8)
    c: Coincident(g9,g8)
    c: Coincident(g9,g0)
    c: Horizontal(g9)
    c: DistanceY(g0,g0) = 24.671
    c: Horizontal(g7)
    c: DistanceY(g6,g6) = 4
    c: DistanceY(g4,g4) = 6
    c: DistanceX(g9,g9) = 2.4
    c: Coincident(g0,g-1)
    c: DistanceY(g-3,g7) = 0
    c: DistanceX(g8,g4) = 0
    c: DistanceX(g-3,g1) = 0
    c: DistanceX(g6,g-3) = 8
FEATURE [Part::Extrusion] Extrude010  label="Extrude buco frontale"
  Base = -> Sketch014
  Dir = (0,-1,2e-16)
  DirMode = 2
  FaceMakerClass = Part::FaceMakerBullseye
  FaceMakerMode = 3
  LengthFwd = 11.2
  LengthRev = 0
  Solid = true
  Symmetric = true
FEATURE [Sketcher::SketchObject] Sketch015  label="guida rail"
  ArcFitTolerance = 1e-06
  AttachmentSupport = -> [XZ_Plane]
  ExternalGeometry = -> [Sketch]
  FullyConstrained = true
  MakeInternals = false
  MapMode = 5
  Placement = pos=(0,0,0) rot=(1,0,0;1.5708rad)
  sketch-geometry (4):
    g0: LineSegment StartX=-100.8 StartY=43.2 StartZ=0 EndX=-44.6 EndY=43.2 EndZ=0
    g1: LineSegment StartX=-44.6 StartY=43.2 StartZ=0 EndX=-44.6 EndY=41.2 EndZ=0
    g2: LineSegment StartX=-44.6 StartY=41.2 StartZ=0 EndX=-100.8 EndY=41.2 EndZ=0
    g3: LineSegment StartX=-100.8 StartY=41.2 StartZ=0 EndX=-100.8 EndY=43.2 EndZ=0
  constraints (9):
    c: Horizontal(g0)
    c: Coincident(g1,g0)
    c: Coincident(g2,g1)
    c: Coincident(g3,g2)
    c: Coincident(g3,g0)
    c: Vertical(g3)
    c: Coincident(g2,g-3)
    c: Coincident(g1,g-3)
    c: Coincident(g0,g-4)
FEATURE [Part::Extrusion] Extrude011  label="Extrude guida rail"
  Base = -> Sketch015
  Dir = (0,-1,2e-16)
  DirMode = 2
  FaceMakerClass = Part::FaceMakerBullseye
  FaceMakerMode = 3
  LengthFwd = 9
  LengthRev = 0
  Solid = true
  Symmetric = true
FEATURE [Sketcher::SketchObject] Sketch016  label="guide per coperture laterali"
  ArcFitTolerance = 1e-06
  AttachmentSupport = -> [XZ_Plane]
  ExternalGeometry = -> [Sketch]
  FullyConstrained = true
  MakeInternals = false
  MapMode = 5
  Placement = pos=(0,0,0) rot=(1,0,0;1.5708rad)
  sketch-geometry (14):
    g0: Circle CenterX=-5.6 CenterY=7.6 CenterZ=0 NormalX=0 NormalY=0 NormalZ=1 AngleXU=0 Radius=1.6
    g1: Circle CenterX=-5.6 CenterY=7.6 CenterZ=0 NormalX=0 NormalY=0 NormalZ=1 AngleXU=0 Radius=4
    g2: Circle CenterX=-5.6 CenterY=34.8 CenterZ=0 NormalX=0 NormalY=0 NormalZ=1 AngleXU=0 Radius=1.6
    g3: Circle CenterX=-5.6 CenterY=34.8 CenterZ=0 NormalX=0 NormalY=0 NormalZ=1 AngleXU=0 Radius=4
    g4: Circle CenterX=-184.08 CenterY=34.8 CenterZ=0 NormalX=0 NormalY=0 NormalZ=1 AngleXU=0 Radius=1.6
    g5: Circle CenterX=-184.08 CenterY=34.8 CenterZ=0 NormalX=0 NormalY=0 NormalZ=1 AngleXU=0 Radius=4
    g6: Circle CenterX=-179.305 CenterY=-76.8316 CenterZ=0 NormalX=0 NormalY=0 NormalZ=1 AngleXU=0 Radius=1.6
    g7: Circle CenterX=-179.305 CenterY=-76.8316 CenterZ=0 NormalX=0 NormalY=0 NormalZ=1 AngleXU=0 Radius=4
    g8: Circle CenterX=-213.443 CenterY=-76.8316 CenterZ=0 NormalX=0 NormalY=0 NormalZ=1 AngleXU=0 Radius=1.6
    g9: Circle CenterX=-213.443 CenterY=-76.8316 CenterZ=0 NormalX=0 NormalY=0 NormalZ=1 AngleXU=0 Radius=4
    g10: Circle CenterX=-78.51 CenterY=7.6 CenterZ=0 NormalX=0 NormalY=0 NormalZ=1 AngleXU=0 Radius=1.6
    g11: Circle CenterX=-78.51 CenterY=7.6 CenterZ=0 NormalX=0 NormalY=0 NormalZ=1 AngleXU=0 Radius=4
    g12: Circle CenterX=-78.51 CenterY=34.8 CenterZ=0 NormalX=0 NormalY=0 NormalZ=1 AngleXU=0 Radius=1.6
    g13: Circle CenterX=-78.51 CenterY=34.8 CenterZ=0 NormalX=0 NormalY=0 NormalZ=1 AngleXU=0 Radius=4
  constraints (35):
    c: Diameter(g0) = 3.2
    c: Diameter(g1) = 8
    c: Coincident(g0,g1)
    c: Diameter(g2) = 3.2
    c: Diameter(g3) = 8
    c: Coincident(g3,g2)
    c: Tangent(g2,g-7)
    c: Diameter(g4) = 3.2
    c: Diameter(g5) = 8
    c: Coincident(g5,g4)
    c: Tangent(g4,g-7)
    c: Tangent(g4,g-8)
    c: Diameter(g6) = 3.2
    c: Diameter(g7) = 8
    c: Coincident(g7,g6)
    c: Tangent(g6,g-9)
    c: Tangent(g6,g-10)
    c: Diameter(g8) = 3.2
    c: Diameter(g9) = 8
    c: Coincident(g9,g8)
    c: Tangent(g8,g-10)
    c: Tangent(g8,g-11)
    c: Diameter(g10) = 3.2
    c: Diameter(g11) = 8
    c: Diameter(g12) = 3.2
    c: Diameter(g13) = 8
    c: Coincident(g12,g13)
    c: Coincident(g10,g11)
    c: Tangent(g12,g-7)
    c: DistanceX(g12,g10) = 0
    c: Tangent(g2,g-6)
    c: Tangent(g0,g-6)
    c: Tangent(g0,g-3)
    c: Tangent(g10,g-3)
    c: Tangent(g10,g-4)
FEATURE [Part::Extrusion] Extrude012  label="extrude guide per coperture laterali"
  Base = -> Sketch016
  Dir = (0,-1,2e-16)
  DirMode = 2
  FaceMakerClass = Part::FaceMakerBullseye
  FaceMakerMode = 3
  LengthFwd = 25.2
  LengthRev = 0
  Solid = true
  Symmetric = true
FEATURE [Sketcher::SketchObject] Sketch017  label="supporto CAM"
  ArcFitTolerance = 1e-06
  AttachmentSupport = -> [XZ_Plane]
  ExternalGeometry = -> [Sketch]
  FullyConstrained = true
  MakeInternals = false
  MapMode = 5
  Placement = pos=(0,0,0) rot=(1,0,0;1.5708rad)
  sketch-geometry (6):
    g0: LineSegment StartX=-2.4 StartY=48 StartZ=0 EndX=-2.4 EndY=41.2 EndZ=0
    g1: LineSegment StartX=-2.4 StartY=48 StartZ=0 EndX=-34 EndY=48 EndZ=0
    g2: LineSegment StartX=-34 StartY=48 StartZ=0 EndX=-34 EndY=46.72 EndZ=0
    g3: LineSegment StartX=-34 StartY=46.72 StartZ=0 EndX=-36 EndY=46.72 EndZ=0
    g4: LineSegment StartX=-36 StartY=46.72 StartZ=0 EndX=-36 EndY=41.2 EndZ=0
    g5: LineSegment StartX=-36 StartY=41.2 StartZ=0 EndX=-2.4 EndY=41.2 EndZ=0
  constraints (15):
    c: Coincident(g1,g0)
    c: Horizontal(g1)
    c: Coincident(g2,g1)
    c: Vertical(g2)
    c: Coincident(g3,g2)
    c: Horizontal(g3)
    c: Coincident(g4,g3)
    c: Coincident(g5,g4)
    c: DistanceX(g1,g0) = 31.6
    c: Coincident(g5,g0)
    c: Vertical(g4)
    c: DistanceY(g2,g1) = 1.28
    c: Coincident(g0,g-3)
    c: Coincident(g0,g-3)
    c: Coincident(g4,g-4)
FEATURE [Part::Extrusion] Extrude013  label="Extrude supporto CAM"
  Base = -> Sketch017
  Dir = (0,-1,2e-16)
  DirMode = 2
  FaceMakerClass = Part::FaceMakerBullseye
  FaceMakerMode = 3
  LengthFwd = 17.8
  LengthRev = 0
  Solid = true
  Symmetric = true
FEATURE [Sketcher::SketchObject] Sketch018  label="Scavo CAM"
  ArcFitTolerance = 1e-06
  AttachmentSupport = -> [YZ_Plane]
  ExternalGeometry = -> [Sketch]
  FullyConstrained = true
  MakeInternals = false
  MapMode = 5
  Placement = pos=(0,0,0) rot=(0.57735,0.57735,0.57735;2.0944rad)
  sketch-geometry (4):
    g0: LineSegment StartX=-7.73 StartY=48 StartZ=0 EndX=7.73 EndY=48 EndZ=0
    g1: LineSegment [constr] StartX=1.07e-14 StartY=48 StartZ=0 EndX=0 EndY=43.5155 EndZ=0
    g2: ArcOfCircle CenterX=9e-15 CenterY=52.42 CenterZ=0 NormalX=0 NormalY=0 NormalZ=1 AngleXU=0 Radius=8.90445 StartAngle=3.66102 EndAngle=5.76376
    g3: Circle [constr] CenterX=9e-15 CenterY=52.42 CenterZ=0 NormalX=0 NormalY=0 NormalZ=1 AngleXU=0 Radius=8.9
  constraints (13):
    c: Horizontal(g0)
    c: DistanceY(g-3,g0) = 0
    c: DistanceX(g0,g0) = 15.46
    c: DistanceX(g0,g-3) = 7.73
    c: DistanceX(g-3) = 0
    c: Coincident(g1,g-3)
    c: PointOnObject(g1,g-2)
    c: Coincident(g2,g0)
    c: Coincident(g2,g0)
    c: PointOnObject(g1,g2)
    c: Diameter(g3) = 17.8
    c: DistanceY(g1,g3) = 4.42
    c: Coincident(g2,g3)
FEATURE [Part::Extrusion] Extrude014  label="Extrude Scavo CAM"
  Base = -> Sketch018
  Dir = (1,0,0)
  DirMode = 2
  FaceMakerClass = Part::FaceMakerBullseye
  FaceMakerMode = 3
  LengthFwd = -34
  LengthRev = 0
  Solid = true
  Symmetric = false
FEATURE [Sketcher::SketchObject] Sketch019  label="scavo rumble"
  ArcFitTolerance = 1e-06
  AttachmentSupport = -> [XZ_Plane]
  ExternalGeometry = -> [Sketch]
  FullyConstrained = true
  MakeInternals = false
  MapMode = 5
  Placement = pos=(0,0,0) rot=(1,0,0;1.5708rad)
  sketch-geometry (6):
    g0: LineSegment StartX=-164.575 StartY=-24.3786 StartZ=0 EndX=-159.439 EndY=-26.0473 EndZ=0
    g1: LineSegment StartX=-159.439 StartY=-26.0473 StartZ=0 EndX=-166.547 EndY=-47.9216 EndZ=0
    g2: LineSegment StartX=-166.547 StartY=-47.9216 StartZ=0 EndX=-171.682 EndY=-46.2529 EndZ=0
    g3: LineSegment StartX=-171.682 StartY=-46.2529 StartZ=0 EndX=-164.575 EndY=-24.3786 EndZ=0
    g4: LineSegment [constr] StartX=-145.51 StartY=22 StartZ=0 EndX=-160.961 EndY=-25.5528 EndZ=0
    g5: LineSegment [constr] StartX=-159.439 StartY=-26.0473 StartZ=0 EndX=-160.961 EndY=-25.5528 EndZ=0
  constraints (17):
    c: Coincident(g1,g0)
    c: Coincident(g2,g1)
    c: Coincident(g3,g2)
    c: Coincident(g3,g0)
    c: Parallel(g3,g-3)
    c: Parallel(g3,g1)
    c: Perpendicular(g3,g0)
    c: Perpendicular(g2,g3)
    c: Distance(g2,g0) = 23
    c: Parallel(g4,g-3)
    c: Distance(g4) = 50
    c: Coincident(g4,g-3)
    c: Parallel(g5,g0)
    c: Distance(g5) = 1.6
    c: Coincident(g5,g0)
    c: Distance(g5,g0) = 3.8
    c: Coincident(g5,g4)
FEATURE [Part::Extrusion] Extrude015  label="scavo rumble001"
  Base = -> Sketch019
  Dir = (0,-1,2e-16)
  DirMode = 2
  FaceMakerClass = Part::FaceMakerBullseye
  FaceMakerMode = 3
  LengthFwd = 21
  LengthRev = 0
  Solid = true
  Symmetric = true
FEATURE [Sketcher::SketchObject] Sketch020  label="fermo rumble"
  ArcFitTolerance = 1e-06
  AttachmentSupport = -> [XZ_Plane]
  ExternalGeometry = -> [Sketch019,Sketch]
  FullyConstrained = true
  MakeInternals = false
  MapMode = 5
  Placement = pos=(0,0,0) rot=(1,0,0;1.5708rad)
  sketch-geometry (16):
    g0: LineSegment [constr] StartX=-166.709 StartY=-43.2425 StartZ=0 EndX=-168.068 EndY=-47.4271 EndZ=0
    g1: LineSegment [constr] StartX=-168.068 StartY=-47.4271 StartZ=0 EndX=-166.547 EndY=-47.9216 EndZ=0
    g2: LineSegment StartX=-168.121 StartY=-40.4703 StartZ=0 EndX=-166.029 EndY=-41.1502 EndZ=0
    g3: LineSegment StartX=-166.029 StartY=-41.1502 StartZ=0 EndX=-166.709 EndY=-43.2425 EndZ=0
    g4: LineSegment StartX=-166.709 StartY=-43.2425 StartZ=0 EndX=-168.801 EndY=-42.5626 EndZ=0
    g5: LineSegment StartX=-168.801 StartY=-42.5626 StartZ=0 EndX=-168.121 EndY=-40.4703 EndZ=0
    g6: LineSegment StartX=-167.627 StartY=-38.9486 StartZ=0 EndX=-164.203 EndY=-40.0611 EndZ=0
    g7: LineSegment StartX=-164.203 StartY=-40.0611 StartZ=0 EndX=-165.81 EndY=-45.0066 EndZ=0
    g8: LineSegment StartX=-165.81 StartY=-45.0066 StartZ=0 EndX=-169.234 EndY=-43.8941 EndZ=0
    g9: LineSegment StartX=-170.261 StartY=-41.878 StartZ=0 EndX=-169.643 EndY=-39.9759 EndZ=0
    g10: LineSegment [constr] StartX=-169.643 StartY=-39.9759 StartZ=0 EndX=-169.148 EndY=-38.4542 EndZ=0
    g11: LineSegment [constr] StartX=-169.148 StartY=-38.4542 StartZ=0 EndX=-167.627 EndY=-38.9486 EndZ=0
    g12: ArcOfCircle CenterX=-168.739 CenterY=-42.3724 CenterZ=0 NormalX=0 NormalY=0 NormalZ=1 AngleXU=0 Radius=1.6 StartAngle=2.82743 EndAngle=4.39823
    g13: GeomPoint [constr] X=-170.755 Y=-43.3997 Z=0
    g14: ArcOfCircle CenterX=-168.121 CenterY=-40.4703 CenterZ=0 NormalX=0 NormalY=0 NormalZ=1 AngleXU=0 Radius=1.6 StartAngle=1.25664 EndAngle=2.82743
    g15: GeomPoint [constr] X=-169.148 Y=-38.4542 Z=0
  constraints (42):
    c: Parallel(g0,g-4)
    c: Distance(g0) = 4.4
    c: Coincident(g1,g0)
    c: Perpendicular(g0,g1)
    c: Distance(g1) = 1.6
    c: Coincident(g1,g-5)
    c: Coincident(g3,g2)
    c: Coincident(g4,g3)
    c: Coincident(g5,g4)
    c: Coincident(g5,g2)
    c: Parallel(g3,g-4)
    c: Parallel(g3,g5)
    c: Perpendicular(g2,g3)
    c: Parallel(g4,g2)
    c: Distance(g2) = 2.2
    c: Distance(g3) = 2.2
    c: Coincident(g7,g6)
    c: Coincident(g8,g7)
    c: Parallel(g7,g-4)
    c: Parallel(g7,g9)
    c: Perpendicular(g6,g7)
    c: Parallel(g6,g8)
    c: Distance(g6,g15) = 5.2
    c: Distance(g7) = 5.2
    c: Coincident(g11,g10)
    c: Parallel(g10,g9)
    c: Parallel(g11,g6)
    c: Distance(g10) = 1.6
    c: Distance(g11) = 1.6
    c: Coincident(g10,g15)
    c: Distance(g11,g2) = 1.6
    c: Distance(g2,g10) = 1.6
    c: PointOnObject(g13,g8)
    c: PointOnObject(g13,g9)
    c: Tangent(g8,g12) = 1.5708
    c: Tangent(g9,g12) = 1.5708
    c: PointOnObject(g15,g9)
    c: Tangent(g6,g14) = 1.5708
    c: Tangent(g9,g14) = 1.5708
    c: Equal(g12,g14)
    c: Coincident(g6,g11)
    c: Coincident(g3,g0)
FEATURE [Part::Extrusion] Extrude016  label="Extrude fermo rumble"
  Base = -> Sketch020
  Dir = (0,-1,2e-16)
  DirMode = 2
  FaceMakerClass = Part::FaceMakerBullseye
  FaceMakerMode = 3
  LengthFwd = 25.2
  LengthRev = 0
  Solid = true
  Symmetric = true
FEATURE [Sketcher::SketchObject] Sketch021  label="perno fermo rumble001"
  ArcFitTolerance = 1e-06
  AttachmentSupport = -> [XZ_Plane001]
  FullyConstrained = true
  MakeInternals = false
  MapMode = 5
  Placement = pos=(0,0,0) rot=(1,0,0;1.5708rad)
  sketch-geometry (16):
    g0: LineSegment StartX=0 StartY=0.45 StartZ=0 EndX=0 EndY=1.55 EndZ=0
    g1: LineSegment StartX=0.45 StartY=2 StartZ=0 EndX=1.55 EndY=2 EndZ=0
    g2: LineSegment StartX=2 StartY=1.55 StartZ=0 EndX=2 EndY=0.45 EndZ=0
    g3: LineSegment StartX=1.55 StartY=0 StartZ=0 EndX=0.45 EndY=0 EndZ=0
    g4: ArcOfCircle [constr] CenterX=0.45 CenterY=1.55 CenterZ=0 NormalX=0 NormalY=0 NormalZ=1 AngleXU=0 Radius=0.45 StartAngle=1.5708 EndAngle=3.14159
    g5: GeomPoint [constr] X=0 Y=2 Z=0
    g6: LineSegment StartX=0.45 StartY=2 StartZ=0 EndX=0 EndY=1.55 EndZ=0
    g7: ArcOfCircle [constr] CenterX=1.55 CenterY=1.55 CenterZ=0 NormalX=0 NormalY=0 NormalZ=1 AngleXU=0 Radius=0.45 StartAngle=0 EndAngle=1.5708
    g8: GeomPoint [constr] X=2 Y=2 Z=0
    g9: LineSegment StartX=2 StartY=1.55 StartZ=0 EndX=1.55 EndY=2 EndZ=0
    g10: ArcOfCircle [constr] CenterX=1.55 CenterY=0.45 CenterZ=0 NormalX=0 NormalY=0 NormalZ=1 AngleXU=0 Radius=0.45 StartAngle=4.71239 EndAngle=6.28319
    g11: GeomPoint [constr] X=2 Y=0 Z=0
    g12: LineSegment StartX=1.55 StartY=0 StartZ=0 EndX=2 EndY=0.45 EndZ=0
    g13: ArcOfCircle [constr] CenterX=0.45 CenterY=0.45 CenterZ=0 NormalX=0 NormalY=0 NormalZ=1 AngleXU=0 Radius=0.45 StartAngle=3.14159 EndAngle=4.71239
    g14: GeomPoint [constr] X=0 Y=0 Z=0
    g15: LineSegment StartX=0 StartY=0.45 StartZ=0 EndX=0.45 EndY=0 EndZ=0
  constraints (35):
    c: Coincident(g14,g-1)
    c: PointOnObject(g5,g-2)
    c: Horizontal(g1)
    c: Vertical(g2)
    c: Horizontal(g3)
    c: DistanceX(g5,g8) = 2
    c: DistanceY(g11,g8) = 2
    c: PointOnObject(g5,g0)
    c: PointOnObject(g5,g1)
    c: Tangent(g0,g4) = 1.5708
    c: Tangent(g1,g4) = 1.5708
    c: Coincident(g6,g0)
    c: Coincident(g6,g1)
    c: PointOnObject(g8,g2)
    c: PointOnObject(g8,g1)
    c: Tangent(g2,g7) = 1.5708
    c: Tangent(g1,g7) = 1.5708
    c: Coincident(g9,g2)
    c: Coincident(g9,g1)
    c: PointOnObject(g11,g2)
    c: PointOnObject(g11,g3)
    c: Tangent(g2,g10) = 1.5708
    c: Tangent(g3,g10) = 1.5708
    c: Coincident(g12,g2)
    c: Coincident(g12,g3)
    c: PointOnObject(g14,g0)
    c: PointOnObject(g14,g3)
    c: Tangent(g0,g13) = 1.5708
    c: Tangent(g3,g13) = 1.5708
    c: Coincident(g15,g0)
    c: Coincident(g15,g3)
    c: Equal(g6,g9)
    c: Equal(g9,g12)
    c: Equal(g12,g15)
    c: DistanceX(g14,g3) = 0.45
FEATURE [Sketcher::SketchObject] Sketch022  label="fori per M3x5(OD)x6(L)"
  ArcFitTolerance = 1e-06
  AttachmentSupport = -> [XZ_Plane]
  ExternalGeometry = -> [Sketch016]
  FullyConstrained = true
  MakeInternals = false
  MapMode = 5
  Placement = pos=(0,0,0) rot=(1,0,0;1.5708rad)
  sketch-geometry (7):
    g0: Circle CenterX=-5.6 CenterY=34.8 CenterZ=0 NormalX=0 NormalY=0 NormalZ=1 AngleXU=0 Radius=2.5
    g1: Circle CenterX=-5.6 CenterY=7.6 CenterZ=0 NormalX=0 NormalY=0 NormalZ=1 AngleXU=0 Radius=2.5
    g2: Circle CenterX=-78.51 CenterY=34.8 CenterZ=0 NormalX=0 NormalY=0 NormalZ=1 AngleXU=0 Radius=2.5
    g3: Circle CenterX=-78.51 CenterY=7.6 CenterZ=0 NormalX=0 NormalY=0 NormalZ=1 AngleXU=0 Radius=2.5
    g4: Circle CenterX=-184.08 CenterY=34.8 CenterZ=0 NormalX=0 NormalY=0 NormalZ=1 AngleXU=0 Radius=2.5
    g5: Circle CenterX=-179.305 CenterY=-76.8316 CenterZ=0 NormalX=0 NormalY=0 NormalZ=1 AngleXU=0 Radius=2.5
    g6: Circle CenterX=-213.443 CenterY=-76.8316 CenterZ=0 NormalX=0 NormalY=0 NormalZ=1 AngleXU=0 Radius=2.5
  constraints (14):
    c: Diameter(g0) = 5
    c: Diameter(g1) = 5
    c: Diameter(g2) = 5
    c: Diameter(g3) = 5
    c: Diameter(g4) = 5
    c: Diameter(g5) = 5
    c: Diameter(g6) = 5
    c: Coincident(g0,g-8)
    c: Coincident(g1,g-9)
    c: Coincident(g2,g-6)
    c: Coincident(g3,g-7)
    c: Coincident(g4,g-5)
    c: Coincident(g5,g-4)
    c: Coincident(g6,g-3)
FEATURE [Part::Extrusion] Extrude018  label="Extrude fori M3x5x6 - dx"
  Base = -> Sketch022
  Dir = (0,-1,2e-16)
  DirMode = 2
  FaceMakerClass = Part::FaceMakerBullseye
  FaceMakerMode = 3
  LengthFwd = 6.2
  LengthRev = 0
  Placement = pos=(0,-9.5,0) rot=(0,0,1;0rad)
  Solid = true
  Symmetric = true
FEATURE [Part::Extrusion] Extrude019  label="Extrude fori M3x5x6 - sx"
  Base = -> Sketch022
  Dir = (0,-1,2e-16)
  DirMode = 2
  FaceMakerClass = Part::FaceMakerBullseye
  FaceMakerMode = 3
  LengthFwd = 6.2
  LengthRev = 0
  Placement = pos=(0,9.5,0) rot=(0,0,1;0rad)
  Solid = true
  Symmetric = true
FEATURE [Sketcher::SketchObject] Sketch023  label="foro anteriore M3x5x6"
  ArcFitTolerance = 1e-06
  AttachmentSupport = -> [YZ_Plane]
  FullyConstrained = true
  MakeInternals = false
  MapMode = 5
  Placement = pos=(0,0,0) rot=(0.57735,0.57735,0.57735;2.0944rad)
  sketch-geometry (2):
    g0: LineSegment [constr] StartX=0 StartY=0 StartZ=0 EndX=0 EndY=38.6 EndZ=0
    g1: Circle CenterX=0 CenterY=38.6 CenterZ=0 NormalX=0 NormalY=0 NormalZ=1 AngleXU=0 Radius=2.5
  constraints (5):
    c: Coincident(g0,g-1)
    c: PointOnObject(g0,g-2)
    c: DistanceY(g0,g0) = 38.6
    c: Diameter(g1) = 5
    c: Coincident(g1,g0)
FEATURE [Part::Extrusion] Extrude020  label="Extrude foro anteriore M3x5x6"
  Base = -> Sketch023
  Dir = (1,0,0)
  DirMode = 2
  FaceMakerClass = Part::FaceMakerBullseye
  FaceMakerMode = 3
  LengthFwd = -6.2
  LengthRev = 0
  Solid = true
  Symmetric = false
FEATURE [Sketcher::SketchObject] Sketch024  label="fori per viti frontale"
  ArcFitTolerance = 1e-06
  AttachmentSupport = -> [YZ_Plane]
  FullyConstrained = true
  MakeInternals = false
  MapMode = 5
  Placement = pos=(0,0,0) rot=(0.57735,0.57735,0.57735;2.0944rad)
  sketch-geometry (9):
    g0: LineSegment [constr] StartX=-10.3 StartY=30.721 StartZ=0 EndX=10.3 EndY=30.721 EndZ=0
    g1: LineSegment [constr] StartX=10.3 StartY=30.721 StartZ=0 EndX=10.3 EndY=10.121 EndZ=0
    g2: LineSegment [constr] StartX=10.3 StartY=10.121 StartZ=0 EndX=-10.3 EndY=10.121 EndZ=0
    g3: LineSegment [constr] StartX=-10.3 StartY=10.121 StartZ=0 EndX=-10.3 EndY=30.721 EndZ=0
    g4: LineSegment [constr] StartX=0 StartY=0 StartZ=0 EndX=0 EndY=10.121 EndZ=0
    g5: Circle CenterX=-10.3 CenterY=30.721 CenterZ=0 NormalX=0 NormalY=0 NormalZ=1 AngleXU=0 Radius=2
    g6: Circle CenterX=10.3 CenterY=30.721 CenterZ=0 NormalX=0 NormalY=0 NormalZ=1 AngleXU=0 Radius=2
    g7: Circle CenterX=-10.3 CenterY=10.121 CenterZ=0 NormalX=0 NormalY=0 NormalZ=1 AngleXU=0 Radius=2
    g8: Circle CenterX=10.3 CenterY=10.121 CenterZ=0 NormalX=0 NormalY=0 NormalZ=1 AngleXU=0 Radius=2
  constraints (22):
    c: Horizontal(g0)
    c: Coincident(g1,g0)
    c: Vertical(g1)
    c: Coincident(g2,g1)
    c: Horizontal(g2)
    c: Coincident(g3,g2)
    c: Coincident(g3,g0)
    c: Vertical(g3)
    c: DistanceX(g0,g0) = 20.6
    c: DistanceY(g3,g3) = 20.6
    c: Coincident(g4,g-1)
    c: PointOnObject(g4,g-2)
    c: DistanceY(g4,g4) = 10.121
    c: Symmetric(g2,g2,g4)
    c: Diameter(g5) = 4
    c: Diameter(g6) = 4
    c: Diameter(g7) = 4
    c: Diameter(g8) = 4
    c: Coincident(g5,g0)
    c: Coincident(g6,g0)
    c: Coincident(g7,g2)
    c: Coincident(g8,g1)
FEATURE [Part::Extrusion] Extrude021  label="Extrude fori per viti frontale"
  Base = -> Sketch024
  Dir = (1,0,0)
  DirMode = 2
  FaceMakerClass = Part::FaceMakerBullseye
  FaceMakerMode = 3
  LengthFwd = -2.4
  LengthRev = 0
  Solid = true
  Symmetric = false
FEATURE [Sketcher::SketchObject] Sketch025  label="foro per filo CAM"
  ArcFitTolerance = 1e-06
  AttachmentSupport = -> [XZ_Plane]
  ExternalGeometry = -> [Sketch]
  FullyConstrained = true
  MakeInternals = false
  MapMode = 5
  Placement = pos=(0,0,0) rot=(1,0,0;1.5708rad)
  sketch-geometry (4):
    g0: LineSegment StartX=-44.6 StartY=41.2 StartZ=0 EndX=-44.6 EndY=36.4 EndZ=0
    g1: LineSegment StartX=-44.6 StartY=36.4 StartZ=0 EndX=-54.6 EndY=36.4 EndZ=0
    g2: LineSegment StartX=-54.6 StartY=36.4 StartZ=0 EndX=-50.4 EndY=41.2 EndZ=0
    g3: LineSegment StartX=-50.4 StartY=41.2 StartZ=0 EndX=-44.6 EndY=41.2 EndZ=0
  constraints (11):
    c: Vertical(g0)
    c: Coincident(g1,g0)
    c: Horizontal(g1)
    c: Coincident(g2,g1)
    c: Coincident(g3,g2)
    c: Coincident(g3,g0)
    c: Horizontal(g3)
    c: Coincident(g0,g-3)
    c: DistanceY(g0,g-4) = 0
    c: DistanceX(g3,g3) = 5.8
    c: DistanceX(g1,g1) = 10
FEATURE [Part::Extrusion] Extrude022  label="Extrude foro per filo CAM dx"
  Base = -> Sketch025
  Dir = (0,-1,2e-16)
  DirMode = 2
  FaceMakerClass = Part::FaceMakerBullseye
  FaceMakerMode = 3
  LengthFwd = 4.9
  LengthRev = 0
  Placement = pos=(0,6.95,0) rot=(0,0,1;0rad)
  Solid = true
  Symmetric = true
FEATURE [Part::Extrusion] Extrude023  label="Extrude foro per filo CAM sx"
  Base = -> Sketch025
  Dir = (0,-1,2e-16)
  DirMode = 2
  FaceMakerClass = Part::FaceMakerBullseye
  FaceMakerMode = 3
  LengthFwd = 4.9
  LengthRev = 0
  Placement = pos=(0,-6.95,0) rot=(0,0,1;0rad)
  Solid = true
  Symmetric = true
FEATURE [Sketcher::SketchObject] Sketch026  label="foro sotto anteriore M3x5x6"
  ArcFitTolerance = 1e-06
  AttachmentSupport = -> [XY_Plane]
  FullyConstrained = true
  MakeInternals = false
  MapMode = 5
  sketch-geometry (2):
    g0: LineSegment [constr] StartX=0 StartY=0 StartZ=0 EndX=-16.5 EndY=0 EndZ=0
    g1: Circle CenterX=-16.5 CenterY=0 CenterZ=0 NormalX=0 NormalY=0 NormalZ=1 AngleXU=0 Radius=2.5
  constraints (5):
    c: Distance(g0) = 16.5
    c: Coincident(g0,g-1)
    c: PointOnObject(g0,g-1)
    c: Diameter(g1) = 5
    c: Coincident(g0,g1)
FEATURE [Sketcher::SketchObject] Sketch027  label="foro sotto posteriore M3x5x6"
  ArcFitTolerance = 1e-06
  AttachmentSupport = -> [XY_Plane]
  ExternalGeometry = -> [Sketch]
  FullyConstrained = true
  MakeInternals = false
  MapMode = 5
  sketch-geometry (2):
    g0: LineSegment [constr] StartX=-82.8 StartY=2e-16 StartZ=0 EndX=-71.3 EndY=2e-16 EndZ=0
    g1: Circle CenterX=-71.3 CenterY=2e-16 CenterZ=0 NormalX=0 NormalY=0 NormalZ=1 AngleXU=0 Radius=2.5
  constraints (5):
    c: Distance(g0) = 11.5
    c: Coincident(g0,g-3)
    c: PointOnObject(g0,g-3)
    c: Diameter(g1) = 5
    c: Coincident(g1,g0)
FEATURE [Sketcher::SketchObject] Sketch029  label="fori sotto impugnatura"
  ArcFitTolerance = 1e-06
  AttachmentSupport = -> [XY_Plane]
  ExternalGeometry = -> [Sketch]
  FullyConstrained = true
  MakeInternals = false
  MapMode = 5
  sketch-geometry (15):
    g0: LineSegment [constr] StartX=-175.232 StartY=-1.83e-14 StartZ=0 EndX=-191.232 EndY=0 EndZ=0
    g1: Circle CenterX=-191.232 CenterY=0 CenterZ=0 NormalX=0 NormalY=0 NormalZ=1 AngleXU=0 Radius=3.95
    g2: LineSegment [constr] StartX=-175.232 StartY=-1.83e-14 StartZ=0 EndX=-204.275 EndY=0 EndZ=0
    g3: LineSegment StartX=-204.275 StartY=3.525 StartZ=0 EndX=-204.275 EndY=-3.525 EndZ=0
    g4: LineSegment StartX=-205.4 StartY=-4.65 StartZ=0 EndX=-206.65 EndY=-4.65 EndZ=0
    g5: LineSegment StartX=-207.775 StartY=-3.525 StartZ=0 EndX=-207.775 EndY=3.525 EndZ=0
    g6: LineSegment StartX=-206.65 StartY=4.65 StartZ=0 EndX=-205.4 EndY=4.65 EndZ=0
    g7: ArcOfCircle CenterX=-206.65 CenterY=3.525 CenterZ=0 NormalX=0 NormalY=0 NormalZ=1 AngleXU=0 Radius=1.125 StartAngle=1.5708 EndAngle=3.14159
    g8: GeomPoint [constr] X=-207.775 Y=4.65 Z=0
    g9: ArcOfCircle CenterX=-205.4 CenterY=3.525 CenterZ=0 NormalX=0 NormalY=0 NormalZ=1 AngleXU=0 Radius=1.125 StartAngle=0 EndAngle=1.5708
    g10: GeomPoint [constr] X=-204.275 Y=4.65 Z=0
    g11: ArcOfCircle CenterX=-205.4 CenterY=-3.525 CenterZ=0 NormalX=0 NormalY=0 NormalZ=1 AngleXU=0 Radius=1.125 StartAngle=4.71239 EndAngle=6.28319
    g12: GeomPoint [constr] X=-204.275 Y=-4.65 Z=0
    g13: ArcOfCircle CenterX=-206.65 CenterY=-3.525 CenterZ=0 NormalX=0 NormalY=0 NormalZ=1 AngleXU=0 Radius=1.125 StartAngle=3.14159 EndAngle=4.71239
    g14: GeomPoint [constr] X=-207.775 Y=-4.65 Z=0
  constraints (35):
    c: Distance(g0) = 16
    c: Coincident(g0,g-3)
    c: PointOnObject(g0,g-1)
    c: Diameter(g1) = 7.9
    c: Coincident(g1,g0)
    c: Coincident(g2,g0)
    c: PointOnObject(g2,g-1)
    c: Vertical(g3)
    c: Horizontal(g4)
    c: Vertical(g5)
    c: Horizontal(g6)
    c: DistanceY(g12,g10) = 9.3
    c: DistanceX(g8,g10) = 3.5
    c: Symmetric(g10,g12,g2)
    c: PointOnObject(g8,g5)
    c: PointOnObject(g8,g6)
    c: Tangent(g5,g7) = 1.5708
    c: Tangent(g6,g7) = 1.5708
    c: PointOnObject(g10,g3)
    c: PointOnObject(g10,g6)
    c: Tangent(g3,g9) = 1.5708
    c: Tangent(g6,g9) = 1.5708
    c: PointOnObject(g12,g3)
    c: PointOnObject(g12,g4)
    c: Tangent(g3,g11) = 1.5708
    c: Tangent(g4,g11) = 1.5708
    c: PointOnObject(g14,g4)
    c: PointOnObject(g14,g5)
    c: Tangent(g4,g13) = 1.5708
    c: Tangent(g5,g13) = 1.5708
    c: Equal(g7,g9)
    c: Equal(g9,g11)
    c: Equal(g11,g13)
    c: DistanceX(g6,g6) = 1.25
    c: DistanceX(g-5,g5) = 6.8
FEATURE [Sketcher::SketchObject] Sketch030  label="fori superiori per solenoide e oled"
  ArcFitTolerance = 1e-06
  AttachmentSupport = -> [XY_Plane]
  ExternalGeometry = -> [Sketch]
  FullyConstrained = true
  MakeInternals = false
  MapMode = 5
  sketch-geometry (33):
    g0: LineSegment [constr] StartX=-181.6 StartY=1.12e-14 StartZ=0 EndX=-169.91 EndY=0 EndZ=0
    g1: LineSegment [constr] StartX=-169.91 StartY=0 StartZ=0 EndX=-169.91 EndY=-2.6 EndZ=0
    g2: LineSegment [constr] StartX=-169.91 StartY=0 StartZ=0 EndX=-169.91 EndY=2.6 EndZ=0
    g3: LineSegment StartX=-169.91 StartY=4.975 StartZ=0 EndX=-169.91 EndY=8.225 EndZ=0
    g4: LineSegment StartX=-167.535 StartY=10.6 StartZ=0 EndX=-167.285 EndY=10.6 EndZ=0
    g5: LineSegment StartX=-164.91 StartY=8.225 StartZ=0 EndX=-164.91 EndY=4.975 EndZ=0
    g6: LineSegment StartX=-167.285 StartY=2.6 StartZ=0 EndX=-167.535 EndY=2.6 EndZ=0
    g7: LineSegment StartX=-169.91 StartY=-4.975 StartZ=0 EndX=-169.91 EndY=-8.225 EndZ=0
    g8: LineSegment StartX=-167.535 StartY=-10.6 StartZ=0 EndX=-167.285 EndY=-10.6 EndZ=0
    g9: LineSegment StartX=-164.91 StartY=-8.225 StartZ=0 EndX=-164.91 EndY=-4.975 EndZ=0
    g10: LineSegment StartX=-167.285 StartY=-2.6 StartZ=0 EndX=-167.535 EndY=-2.6 EndZ=0
    g11: ArcOfCircle CenterX=-167.535 CenterY=8.225 CenterZ=0 NormalX=0 NormalY=0 NormalZ=1 AngleXU=0 Radius=2.375 StartAngle=1.5708 EndAngle=3.14159
    g12: GeomPoint [constr] X=-169.91 Y=10.6 Z=0
    g13: ArcOfCircle CenterX=-167.285 CenterY=8.225 CenterZ=0 NormalX=0 NormalY=0 NormalZ=1 AngleXU=0 Radius=2.375 StartAngle=0 EndAngle=1.5708
    g14: GeomPoint [constr] X=-164.91 Y=10.6 Z=0
    g15: ArcOfCircle CenterX=-167.285 CenterY=4.975 CenterZ=0 NormalX=0 NormalY=0 NormalZ=1 AngleXU=0 Radius=2.375 StartAngle=4.71239 EndAngle=6.28319
    g16: GeomPoint [constr] X=-164.91 Y=2.6 Z=0
    g17: ArcOfCircle CenterX=-167.535 CenterY=4.975 CenterZ=0 NormalX=0 NormalY=0 NormalZ=1 AngleXU=0 Radius=2.375 StartAngle=3.14159 EndAngle=4.71239
    g18: GeomPoint [constr] X=-169.91 Y=2.6 Z=0
    g19: ArcOfCircle CenterX=-167.535 CenterY=-4.975 CenterZ=0 NormalX=0 NormalY=0 NormalZ=1 AngleXU=0 Radius=2.375 StartAngle=1.5708 EndAngle=3.14159
    g20: GeomPoint [constr] X=-169.91 Y=-2.6 Z=0
    g21: ArcOfCircle CenterX=-167.285 CenterY=-4.975 CenterZ=0 NormalX=0 NormalY=0 NormalZ=1 AngleXU=0 Radius=2.375 StartAngle=0 EndAngle=1.5708
    g22: GeomPoint [constr] X=-164.91 Y=-2.6 Z=0
    g23: ArcOfCircle CenterX=-167.285 CenterY=-8.225 CenterZ=0 NormalX=0 NormalY=0 NormalZ=1 AngleXU=0 Radius=2.375 StartAngle=4.71239 EndAngle=6.28319
    g24: GeomPoint [constr] X=-164.91 Y=-10.6 Z=0
    g25: ArcOfCircle CenterX=-167.535 CenterY=-8.225 CenterZ=0 NormalX=0 NormalY=0 NormalZ=1 AngleXU=0 Radius=2.375 StartAngle=3.14159 EndAngle=4.71239
    g26: GeomPoint [constr] X=-169.91 Y=-10.6 Z=0
    g27: LineSegment [constr] StartX=-181.6 StartY=1.12e-14 StartZ=0 EndX=-152.209 EndY=0 EndZ=0
    g28: LineSegment [constr] StartX=-181.6 StartY=1.12e-14 StartZ=0 EndX=-130.41 EndY=0 EndZ=0
    g29: LineSegment [constr] StartX=-152.209 StartY=0 StartZ=0 EndX=-152.209 EndY=6.95 EndZ=0
    g30: LineSegment [constr] StartX=-130.41 StartY=0 StartZ=0 EndX=-130.41 EndY=-6.95 EndZ=0
    g31: Circle CenterX=-152.209 CenterY=6.95 CenterZ=0 NormalX=0 NormalY=0 NormalZ=1 AngleXU=0 Radius=2.1
    g32: Circle CenterX=-130.41 CenterY=-6.95 CenterZ=0 NormalX=0 NormalY=0 NormalZ=1 AngleXU=0 Radius=2.1
  constraints (79):
    c: Distance(g0) = 11.69
    c: PointOnObject(g0,g-1)
    c: Coincident(g-4,g0)
    c: Distance(g1) = 2.6
    c: Coincident(g1,g0)
    c: Vertical(g1)
    c: Distance(g2) = 2.6
    c: Coincident(g2,g0)
    c: Vertical(g2)
    c: Distance(g18,g12) = 8
    c: Coincident(g18,g2)
    c: Vertical(g3)
    c: Distance(g14,g12) = 5
    c: Horizontal(g4)
    c: Distance(g16,g14) = 8
    c: Vertical(g5)
    c: Distance(g26,g20) = 8
    c: Coincident(g20,g1)
    c: Vertical(g7)
    c: Distance(g26,g24) = 5
    c: Horizontal(g8)
    c: Distance(g24,g22) = 8
    c: Vertical(g9)
    c: PointOnObject(g12,g3)
    c: PointOnObject(g12,g4)
    c: Tangent(g3,g11) = 1.5708
    c: Tangent(g4,g11) = 1.5708
    c: PointOnObject(g14,g5)
    c: PointOnObject(g14,g4)
    c: Tangent(g5,g13) = 1.5708
    c: Tangent(g4,g13) = 1.5708
    c: PointOnObject(g16,g5)
    c: PointOnObject(g16,g6)
    c: Tangent(g5,g15) = 1.5708
    c: Tangent(g6,g15) = 1.5708
    c: PointOnObject(g18,g3)
    c: PointOnObject(g18,g6)
    c: Tangent(g3,g17) = 1.5708
    c: Tangent(g6,g17) = 1.5708
    c: Equal(g11,g13)
    c: Equal(g13,g15)
    c: Equal(g15,g17)
    c: DistanceX(g4,g4) = 0.25
    c: PointOnObject(g20,g7)
    c: PointOnObject(g20,g10)
    c: Tangent(g7,g19) = -1.5708
    c: Tangent(g10,g19) = -1.5708
    c: PointOnObject(g22,g9)
    c: PointOnObject(g22,g10)
    c: Tangent(g9,g21) = -1.5708
    c: Tangent(g10,g21) = -1.5708
    c: PointOnObject(g24,g9)
    c: PointOnObject(g24,g8)
    c: Tangent(g9,g23) = -1.5708
    c: Tangent(g8,g23) = -1.5708
    c: PointOnObject(g26,g8)
    c: PointOnObject(g26,g7)
    c: Tangent(g8,g25) = -1.5708
    c: Tangent(g7,g25) = -1.5708
    c: Equal(g19,g21)
    c: Equal(g21,g23)
    c: Equal(g23,g25)
    c: DistanceX(g10,g10) = 0.25
    c: Distance(g27) = 29.391
    c: Coincident(g27,g0)
    c: PointOnObject(g27,g-1)
    c: Distance(g28) = 51.19
    c: Coincident(g28,g0)
    c: PointOnObject(g28,g-1)
    c: Distance(g29) = 6.95
    c: Coincident(g29,g27)
    c: Vertical(g29)
    c: Distance(g30) = 6.95
    c: Coincident(g30,g28)
    c: Vertical(g30)
    c: Diameter(g31) = 4.2
    c: Diameter(g32) = 4.2
    c: Coincident(g32,g30)
    c: Coincident(g31,g29)
FEATURE [Sketcher::SketchObject] Sketch031  label="fori inferiori switch pompa"
  ArcFitTolerance = 1e-06
  AttachmentSupport = -> [XY_Plane]
  ExternalGeometry = -> [Sketch]
  FullyConstrained = true
  MakeInternals = false
  MapMode = 5
  sketch-geometry (4):
    g0: LineSegment [constr] StartX=-57.2 StartY=1.9e-15 StartZ=0 EndX=-62.45 EndY=1.9e-15 EndZ=0
    g1: LineSegment [constr] StartX=-62.45 StartY=3.25 StartZ=0 EndX=-62.45 EndY=-3.25 EndZ=0
    g2: Circle CenterX=-62.45 CenterY=3.25 CenterZ=0 NormalX=0 NormalY=0 NormalZ=1 AngleXU=0 Radius=1.6
    g3: Circle CenterX=-62.45 CenterY=-3.25 CenterZ=0 NormalX=0 NormalY=0 NormalZ=1 AngleXU=0 Radius=1.6
  constraints (10):
    c: Distance(g0) = 5.25
    c: Coincident(g0,g-3)
    c: PointOnObject(g0,g-3)
    c: Vertical(g1)
    c: DistanceY(g1,g1) = 6.5
    c: Symmetric(g1,g1,g0)
    c: Diameter(g2) = 3.2
    c: Diameter(g3) = 3.2
    c: Coincident(g2,g1)
    c: Coincident(g3,g1)
FEATURE [Sketcher::SketchObject] Sketch032  label="spazio per PILA 18650"
  ArcFitTolerance = 1e-06
  AttachmentSupport = -> [XY_Plane]
  ExternalGeometry = -> [Sketch]
  FullyConstrained = true
  MakeInternals = false
  MapMode = 5
  sketch-geometry (2):
    g0: LineSegment [constr] StartX=-178.142 StartY=-1.74e-14 StartZ=0 EndX=-190.142 EndY=-1.83e-14 EndZ=0
    g1: Circle CenterX=-190.142 CenterY=-1.83e-14 CenterZ=0 NormalX=0 NormalY=0 NormalZ=1 AngleXU=0 Radius=9.25
  constraints (5):
    c: Distance(g0) = 12
    c: Coincident(g0,g-3)
    c: PointOnObject(g0,g-4)
    c: Diameter(g1) = 18.5
    c: Coincident(g1,g0)
FEATURE [Part::Extrusion] Extrude030  label="Extrude spazio per PILA 18650"
  Base = -> Sketch032
  Dir = (0,0,1)
  DirLink = -> Sketch [Edge45]
  DirMode = 2
  FaceMakerClass = Part::FaceMakerBullseye
  FaceMakerMode = 3
  LengthFwd = 68
  LengthRev = 0
  Placement = pos=(6,0,-72.7) rot=(0,0,1;0rad)
  Solid = true
  Symmetric = false
FEATURE [Sketcher::SketchObject] Sketch033  label="fermo per scheda micro"
  ArcFitTolerance = 1e-06
  AttachmentSupport = -> [XZ_Plane]
  ExternalGeometry = -> [Sketch]
  FullyConstrained = true
  MakeInternals = false
  MapMode = 5
  Placement = pos=(0,0,0) rot=(1,0,0;1.5708rad)
  sketch-geometry (12):
    g0: LineSegment StartX=-11.6 StartY=6 StartZ=0 EndX=-4 EndY=6 EndZ=0
    g1: LineSegment StartX=-4 StartY=6 StartZ=0 EndX=-4 EndY=36.4 EndZ=0
    g2: LineSegment StartX=-4 StartY=36.4 StartZ=0 EndX=-11.6 EndY=36.4 EndZ=0
    g3: LineSegment StartX=-11.6 StartY=36.4 StartZ=0 EndX=-11.6 EndY=6 EndZ=0
    g4: LineSegment StartX=-80.11 StartY=11.6 StartZ=0 EndX=-70.51 EndY=11.6 EndZ=0
    g5: LineSegment StartX=-70.51 StartY=11.6 StartZ=0 EndX=-70.51 EndY=6 EndZ=0
    g6: LineSegment StartX=-70.51 StartY=6 StartZ=0 EndX=-80.11 EndY=6 EndZ=0
    g7: LineSegment StartX=-80.11 StartY=6 StartZ=0 EndX=-80.11 EndY=11.6 EndZ=0
    g8: LineSegment StartX=-78.51 StartY=36.4 StartZ=0 EndX=-70.51 EndY=36.4 EndZ=0
    g9: LineSegment StartX=-70.51 StartY=36.4 StartZ=0 EndX=-70.51 EndY=30.8 EndZ=0
    g10: LineSegment StartX=-70.51 StartY=30.8 StartZ=0 EndX=-78.51 EndY=30.8 EndZ=0
    g11: LineSegment StartX=-78.51 StartY=30.8 StartZ=0 EndX=-78.51 EndY=36.4 EndZ=0
  constraints (33):
    c: Horizontal(g0)
    c: Coincident(g1,g0)
    c: Coincident(g2,g1)
    c: Horizontal(g2)
    c: Coincident(g3,g2)
    c: Coincident(g3,g0)
    c: Vertical(g3)
    c: DistanceX(g2,g2) = 7.6
    c: Coincident(g1,g-3)
    c: Coincident(g0,g-3)
    c: Horizontal(g4)
    c: Coincident(g5,g4)
    c: Vertical(g5)
    c: Coincident(g6,g5)
    c: Horizontal(g6)
    c: Coincident(g7,g6)
    c: Coincident(g7,g4)
    c: Vertical(g7)
    c: DistanceY(g5,g5) = 5.6
    c: DistanceX(g4,g4) = 9.6
    c: Coincident(g9,g8)
    c: Vertical(g9)
    c: Coincident(g10,g9)
    c: Horizontal(g10)
    c: Coincident(g11,g10)
    c: Coincident(g11,g8)
    c: Vertical(g11)
    c: DistanceY(g9,g9) = 5.6
    c: DistanceX(g10,g10) = 8
    c: Coincident(g4,g-4)
    c: DistanceX(g4,g10) = 1.6
    c: Horizontal(g8)
    c: DistanceY(g8,g1) = 0
FEATURE [Sketcher::SketchObject] Sketch034  label="buchi guida rail"
  ArcFitTolerance = 1e-06
  AttachmentSupport = -> [XY_Plane]
  ExternalGeometry = -> [Sketch]
  FullyConstrained = true
  MakeInternals = false
  MapMode = 5
  sketch-geometry (6):
    g0: LineSegment [constr] StartX=-100.8 StartY=9.1e-15 StartZ=0 EndX=-93.3 EndY=0 EndZ=0
    g1: LineSegment [constr] StartX=-93.3 StartY=0 StartZ=0 EndX=-73.3 EndY=0 EndZ=0
    g2: LineSegment [constr] StartX=-73.3 StartY=0 StartZ=0 EndX=-53.3 EndY=0 EndZ=0
    g3: Circle CenterX=-93.3 CenterY=0 CenterZ=0 NormalX=0 NormalY=0 NormalZ=1 AngleXU=0 Radius=2.5
    g4: Circle CenterX=-73.3 CenterY=0 CenterZ=0 NormalX=0 NormalY=0 NormalZ=1 AngleXU=0 Radius=2.5
    g5: Circle CenterX=-53.3 CenterY=0 CenterZ=0 NormalX=0 NormalY=0 NormalZ=1 AngleXU=0 Radius=2.5
  constraints (15):
    c: Distance(g0) = 7.5
    c: Coincident(g0,g-3)
    c: PointOnObject(g0,g-1)
    c: Distance(g1) = 20
    c: Coincident(g1,g0)
    c: PointOnObject(g1,g-1)
    c: Distance(g2) = 20
    c: Coincident(g2,g1)
    c: PointOnObject(g2,g-1)
    c: Diameter(g3) = 5
    c: Diameter(g4) = 5
    c: Diameter(g5) = 5
    c: Coincident(g3,g0)
    c: Coincident(g4,g1)
    c: Coincident(g5,g2)
FEATURE [Part::Extrusion] Extrude032  label="Extrude buchi guida rail"
  Base = -> Sketch034
  Dir = (0,0,1)
  DirMode = 2
  FaceMakerClass = Part::FaceMakerBullseye
  FaceMakerMode = 3
  LengthFwd = -6.2
  LengthRev = 0
  Placement = pos=(0,0,43.2) rot=(0,0,1;0rad)
  Solid = true
  Symmetric = false
FEATURE [Part::Extrusion] Extrude033  label="Extrude fori superiori per solenoide e oled001"
  Base = -> Sketch030
  Dir = (0,0,1)
  DirMode = 2
  FaceMakerClass = Part::FaceMakerBullseye
  FaceMakerMode = 3
  LengthFwd = -4.8
  LengthRev = 0
  Placement = pos=(0,0,41.2) rot=(0,0,1;0rad)
  Solid = true
  Symmetric = false
FEATURE [Part::Extrusion] Extrude034  label="Extrude fori sotto impugnatura001"
  Base = -> Sketch029
  Dir = (0,0,1)
  DirMode = 2
  FaceMakerClass = Part::FaceMakerBullseye
  FaceMakerMode = 3
  LengthFwd = 5
  LengthRev = 0
  Placement = pos=(0,0,-83) rot=(0,0,1;0rad)
  Solid = true
  Symmetric = false
FEATURE [Part::Extrusion] Extrude035  label="Extrude fori inferiori switch pompa001"
  Base = -> Sketch031
  Dir = (0,0,1)
  DirMode = 2
  FaceMakerClass = Part::FaceMakerBullseye
  FaceMakerMode = 3
  LengthFwd = 4
  LengthRev = 0
  Placement = pos=(0,0,-1.7) rot=(0,0,1;0rad)
  Solid = true
  Symmetric = false
FEATURE [Part::Extrusion] Extrude036  label="Extrude foro sotto posteriore M3x5x007"
  Base = -> Sketch027
  Dir = (0,0,1)
  DirMode = 2
  FaceMakerClass = Part::FaceMakerBullseye
  FaceMakerMode = 3
  LengthFwd = 6.2
  LengthRev = 0
  Placement = pos=(0,0,-9.6) rot=(0,0,1;0rad)
  Solid = true
  Symmetric = false
FEATURE [Part::Extrusion] Extrude037  label="Extrude foro sotto anteriore M3x5x007"
  Base = -> Sketch026
  Dir = (0,0,1)
  DirMode = 2
  FaceMakerClass = Part::FaceMakerBullseye
  FaceMakerMode = 3
  LengthFwd = 6.2
  LengthRev = 0
  Solid = true
  Symmetric = false
FEATURE [Sketcher::SketchObject] Sketch035  label="foro per fissaggio micro"
  ArcFitTolerance = 1e-06
  AttachmentSupport = -> [XZ_Plane]
  ExternalGeometry = -> [Sketch,Sketch033]
  FullyConstrained = true
  MakeInternals = false
  MapMode = 5
  Placement = pos=(0,0,0) rot=(1,0,0;1.5708rad)
  sketch-geometry (3):
    g0: Circle CenterX=-7.8 CenterY=21.2 CenterZ=0 NormalX=0 NormalY=0 NormalZ=1 AngleXU=0 Radius=1.6
    g1: GeomPoint [constr] X=-4 Y=21.2 Z=0
    g2: LineSegment [constr] StartX=-4 StartY=21.2 StartZ=0 EndX=-11.6 EndY=21.2 EndZ=0
  constraints (6):
    c: Diameter(g0) = 3.2
    c: Symmetric(g-3,g-3,g1)
    c: Coincident(g2,g1)
    c: Horizontal(g2)
    c: DistanceX(g-4,g2) = 0
    c: Symmetric(g2,g1,g0)
FEATURE [Part::Extrusion] Extrude038  label="Extrude foro per fissaggio micro"
  Base = -> Sketch035
  Dir = (0,-1,2e-16)
  DirMode = 2
  FaceMakerClass = Part::FaceMakerBullseye
  FaceMakerMode = 3
  LengthFwd = 3
  LengthRev = 0
  Placement = pos=(0,8.6,0) rot=(0,0,1;0rad)
  Solid = true
  Symmetric = false
FEATURE [Sketcher::SketchObject] Sketch036  label="supporto per alimentatore"
  ArcFitTolerance = 1e-06
  AttachmentSupport = -> [XZ_Plane]
  ExternalGeometry = -> [Sketch,Sketch016,Sketch022]
  FullyConstrained = true
  MakeInternals = false
  MapMode = 5
  Placement = pos=(0,0,0) rot=(1,0,0;1.5708rad)
  sketch-geometry (5):
    g0: LineSegment StartX=-211.843 StartY=-50.0944 StartZ=0 EndX=-211.843 EndY=-80.4316 EndZ=0
    g1: LineSegment StartX=-211.843 StartY=-50.0944 StartZ=0 EndX=-207.775 EndY=-41.3701 EndZ=0
    g2: LineSegment [constr] StartX=-209.443 StartY=-50.0944 StartZ=0 EndX=-209.443 EndY=-80.4316 EndZ=0
    g3: LineSegment StartX=-207.775 StartY=-41.3701 StartZ=0 EndX=-207.775 EndY=-80.4316 EndZ=0
    g4: LineSegment StartX=-211.843 StartY=-80.4316 StartZ=0 EndX=-207.775 EndY=-80.4316 EndZ=0
  constraints (15):
    c: Vertical(g0)
    c: Coincident(g1,g0)
    c: Vertical(g2)
    c: Tangent(g2,g-5)
    c: Coincident(g3,g1)
    c: Vertical(g3)
    c: DistanceY(g-3,g3) = -2
    c: Tangent(g1,g-8)
    c: DistanceY(g-3,g0) = -2
    c: Coincident(g4,g0)
    c: Coincident(g4,g3)
    c: Tangent(g0,g-6)
    c: DistanceY(g-3,g2) = -2
    c: DistanceY(g2,g0) = 0
    c: DistanceX(g-3,g3) = 6.8
FEATURE [Part::Extrusion] Extrude039  label="Extrude039 supporto alimentatore"
  Base = -> Sketch036
  Dir = (0,-1,2e-16)
  DirMode = 2
  FaceMakerClass = Part::FaceMakerBullseye
  FaceMakerMode = 3
  LengthFwd = 25.2
  LengthRev = 0
  Solid = true
  Symmetric = true
FEATURE [Sketcher::SketchObject] Sketch037  label="scavo per alimentatore"
  ArcFitTolerance = 1e-06
  AttachmentSupport = -> [XZ_Plane]
  ExternalGeometry = -> [Sketch036]
  FullyConstrained = true
  MakeInternals = false
  MapMode = 5
  Placement = pos=(0,0,0) rot=(1,0,0;1.5708rad)
  sketch-geometry (4):
    g0: LineSegment StartX=-209.575 StartY=-50.4316 StartZ=0 EndX=-209.575 EndY=-80.4316 EndZ=0
    g1: LineSegment StartX=-209.575 StartY=-50.4316 StartZ=0 EndX=-207.775 EndY=-50.4316 EndZ=0
    g2: LineSegment StartX=-207.775 StartY=-50.4316 StartZ=0 EndX=-207.775 EndY=-80.4316 EndZ=0
    g3: LineSegment StartX=-207.775 StartY=-80.4316 StartZ=0 EndX=-209.575 EndY=-80.4316 EndZ=0
  constraints (11):
    c: Vertical(g0)
    c: Coincident(g1,g0)
    c: Horizontal(g1)
    c: Coincident(g2,g1)
    c: Vertical(g2)
    c: Coincident(g3,g2)
    c: Coincident(g3,g0)
    c: Horizontal(g3)
    c: DistanceX(g1,g1) = 1.8
    c: Coincident(g2,g-3)
    c: DistanceY(g2,g2) = 30
FEATURE [Part::Extrusion] Extrude040  label="Extrude040 scavo alimentatore"
  Base = -> Sketch037
  Dir = (0,-1,2e-16)
  DirMode = 2
  FaceMakerClass = Part::FaceMakerBullseye
  FaceMakerMode = 3
  LengthFwd = 19.5
  LengthRev = 0
  Solid = true
  Symmetric = true
FEATURE [Part::Extrusion] Extrude031  label="Extrude fermo per scheda micro"
  Base = -> Sketch033
  Dir = (0,-1,2e-16)
  DirMode = 2
  FaceMakerClass = Part::FaceMakerBullseye
  FaceMakerMode = 3
  LengthFwd = 3
  LengthRev = 0
  Placement = pos=(0,8.6,0) rot=(0,0,1;0rad)
  Solid = true
  Symmetric = false
FEATURE [Sketcher::SketchObject] Sketch038  label="scavo driver solenoide"
  ArcFitTolerance = 1e-06
  AttachmentSupport = -> [XZ_Plane]
  ExternalGeometry = -> [Sketch,Sketch036]
  FullyConstrained = true
  MakeInternals = false
  MapMode = 5
  Placement = pos=(0,0,0) rot=(1,0,0;1.5708rad)
  sketch-geometry (7):
    g0: LineSegment StartX=-193.66 StartY=-11.0994 StartZ=0 EndX=-195.11 EndY=-10.4232 EndZ=0
    g1: LineSegment StartX=-195.11 StartY=-10.4232 StartZ=0 EndX=-209.225 EndY=-40.6939 EndZ=0
    g2: LineSegment StartX=-193.66 StartY=-11.0994 StartZ=0 EndX=-190.216 EndY=-12.7054 EndZ=0
    g3: LineSegment StartX=-190.216 StartY=-12.7054 StartZ=0 EndX=-204.331 EndY=-42.9761 EndZ=0
    g4: LineSegment StartX=-204.331 StartY=-42.9761 StartZ=0 EndX=-207.775 EndY=-41.3701 EndZ=0
    g5: LineSegment [constr] StartX=-209.225 StartY=-40.6939 StartZ=0 EndX=-207.775 EndY=-41.3701 EndZ=0
    g6: LineSegment StartX=-209.225 StartY=-40.6939 StartZ=0 EndX=-207.775 EndY=-41.3701 EndZ=0
  constraints (19):
    c: Coincident(g1,g0)
    c: Coincident(g3,g2)
    c: Coincident(g4,g3)
    c: Distance(g2) = 3.8
    c: Distance(g1) = 33.4
    c: Coincident(g5,g1)
    c: Distance(g5) = 1.6
    c: Coincident(g-4,g5)
    c: Perpendicular(g5,g-3)
    c: Parallel(g1,g-3)
    c: Perpendicular(g1,g0)
    c: Distance(g0) = 1.6
    c: Coincident(g6,g1)
    c: Coincident(g6,g5)
    c: Parallel(g3,g-3)
    c: Perpendicular(g3,g4)
    c: Perpendicular(g2,g3)
    c: Coincident(g2,g0)
    c: Coincident(g4,g5)
FEATURE [Part::Extrusion] Extrude041  label="Extrude scavo driver solenoide"
  Base = -> Sketch038
  Dir = (0,-1,2e-16)
  DirMode = 2
  FaceMakerClass = Part::FaceMakerBullseye
  FaceMakerMode = 3
  LengthFwd = 17
  LengthRev = 0
  Solid = true
  Symmetric = true
FEATURE [Sketcher::SketchObject] Sketch039  label="scavo per cavo usb per micro"
  ArcFitTolerance = 1e-06
  AttachmentSupport = -> [XZ_Plane]
  ExternalGeometry = -> [Sketch,Sketch016]
  FullyConstrained = true
  MakeInternals = false
  MapMode = 5
  Placement = pos=(0,0,0) rot=(1,0,0;1.5708rad)
  sketch-geometry (4):
    g0: LineSegment StartX=-82.51 StartY=36.4 StartZ=0 EndX=-74.51 EndY=36.4 EndZ=0
    g1: LineSegment StartX=-74.51 StartY=36.4 StartZ=0 EndX=-74.51 EndY=30.8 EndZ=0
    g2: LineSegment StartX=-74.51 StartY=30.8 StartZ=0 EndX=-82.51 EndY=30.8 EndZ=0
    g3: LineSegment StartX=-82.51 StartY=30.8 StartZ=0 EndX=-82.51 EndY=36.4 EndZ=0
  constraints (11):
    c: Coincident(g1,g0)
    c: Vertical(g1)
    c: Coincident(g2,g1)
    c: Horizontal(g2)
    c: Coincident(g3,g2)
    c: Coincident(g3,g0)
    c: Vertical(g3)
    c: Tangent(g0,g-3)
    c: Tangent(g2,g-4)
    c: Tangent(g3,g-4)
    c: Tangent(g1,g-4)
FEATURE [Part::Extrusion] Extrude042  label="Extrude scavo per cavo usb per micro"
  Base = -> Sketch039
  Dir = (0,-1,2e-16)
  DirMode = 2
  FaceMakerClass = Part::FaceMakerBullseye
  FaceMakerMode = 3
  LengthFwd = 11.2
  LengthRev = 0
  Solid = true
  Symmetric = true
FEATURE [Sketcher::SketchObject] Sketch040  label="scavo saldature alimentatore connettore 5v"
  ArcFitTolerance = 1e-06
  AttachmentSupport = -> [XZ_Plane]
  ExternalGeometry = -> [Sketch037]
  FullyConstrained = true
  MakeInternals = false
  MapMode = 5
  Placement = pos=(0,0,0) rot=(1,0,0;1.5708rad)
  sketch-geometry (4):
    g0: LineSegment StartX=-211.175 StartY=-52.4316 StartZ=0 EndX=-211.175 EndY=-56.4316 EndZ=0
    g1: LineSegment StartX=-211.175 StartY=-52.4316 StartZ=0 EndX=-209.575 EndY=-52.4316 EndZ=0
    g2: LineSegment StartX=-209.575 StartY=-52.4316 StartZ=0 EndX=-209.575 EndY=-56.4316 EndZ=0
    g3: LineSegment StartX=-209.575 StartY=-56.4316 StartZ=0 EndX=-211.175 EndY=-56.4316 EndZ=0
  constraints (11):
    c: Vertical(g0)
    c: Coincident(g1,g0)
    c: Horizontal(g1)
    c: Coincident(g2,g1)
    c: Coincident(g3,g2)
    c: Coincident(g3,g0)
    c: Horizontal(g3)
    c: DistanceX(g1,g1) = 1.6
    c: DistanceY(g2,g2) = 4
    c: Tangent(g2,g-3)
    c: DistanceY(g1,g-3) = 2
FEATURE [Part::Extrusion] Extrude043  label="Extrude scavo saldature alimentatore connettore 5v"
  Base = -> Sketch040
  Dir = (0,-1,2e-16)
  DirMode = 2
  FaceMakerClass = Part::FaceMakerBullseye
  FaceMakerMode = 3
  LengthFwd = 8
  LengthRev = 0
  Solid = true
  Symmetric = true
FEATURE [Sketcher::SketchObject] Sketch041  label="scavo saldature alimentatore connettore 5v verticali"
  ArcFitTolerance = 1e-06
  AttachmentSupport = -> [XZ_Plane]
  ExternalGeometry = -> [Sketch037]
  FullyConstrained = true
  MakeInternals = false
  MapMode = 5
  Placement = pos=(0,0,0) rot=(1,0,0;1.5708rad)
  sketch-geometry (4):
    g0: LineSegment StartX=-211.175 StartY=-53.6316 StartZ=0 EndX=-209.575 EndY=-53.6316 EndZ=0
    g1: LineSegment StartX=-209.575 StartY=-53.6316 StartZ=0 EndX=-209.575 EndY=-76.6316 EndZ=0
    g2: LineSegment StartX=-209.575 StartY=-76.6316 StartZ=0 EndX=-211.175 EndY=-76.6316 EndZ=0
    g3: LineSegment StartX=-211.175 StartY=-76.6316 StartZ=0 EndX=-211.175 EndY=-53.6316 EndZ=0
  constraints (11):
    c: Horizontal(g0)
    c: Coincident(g1,g0)
    c: Coincident(g2,g1)
    c: Horizontal(g2)
    c: Coincident(g3,g2)
    c: Coincident(g3,g0)
    c: Vertical(g3)
    c: DistanceY(g3,g3) = 23
    c: DistanceX(g0,g0) = 1.6
    c: Tangent(g1,g-3)
    c: DistanceY(g0,g-3) = 3.2
FEATURE [Part::Extrusion] Extrude044  label="Extrude scavo saldature alimentatore connettore 5v verticali"
  Base = -> Sketch041
  Dir = (0,-1,2e-16)
  DirMode = 2
  FaceMakerClass = Part::FaceMakerBullseye
  FaceMakerMode = 3
  LengthFwd = 3.2
  LengthRev = 0
  Placement = pos=(0,8.3,0) rot=(0,0,1;0rad)
  Solid = true
  Symmetric = false
FEATURE [Sketcher::SketchObject] Sketch042  label="fermi per driver solenoide e alimentatore"
  ArcFitTolerance = 1e-06
  AttachmentSupport = -> [XZ_Plane]
  ExternalGeometry = -> [Sketch036,Sketch037,Sketch,Sketch038]
  FullyConstrained = true
  MakeInternals = false
  MapMode = 5
  Placement = pos=(0,0,0) rot=(1,0,0;1.5708rad)
  sketch-geometry (27):
    g0: LineSegment StartX=-195.773 StartY=-15.631 StartZ=0 EndX=-196.702 EndY=-17.6249 EndZ=0
    g1: LineSegment StartX=-196.702 StartY=-17.6249 StartZ=0 EndX=-194.709 EndY=-18.5546 EndZ=0
    g2: LineSegment StartX=-194.709 StartY=-18.5546 StartZ=0 EndX=-193.779 EndY=-16.5607 EndZ=0
    g3: LineSegment StartX=-193.779 StartY=-16.5607 StartZ=0 EndX=-195.773 EndY=-15.631 EndZ=0
    g4: LineSegment StartX=-196.547 StartY=-13.5047 StartZ=0 EndX=-198.829 EndY=-18.3988 EndZ=0
    g5: LineSegment StartX=-198.829 StartY=-18.3988 StartZ=0 EndX=-195.385 EndY=-20.0047 EndZ=0
    g6: LineSegment StartX=-193.258 StartY=-19.2308 StartZ=0 EndX=-192.329 EndY=-17.2369 EndZ=0
    g7: LineSegment StartX=-193.103 StartY=-15.1106 StartZ=0 EndX=-196.547 EndY=-13.5047 EndZ=0
    g8: LineSegment [constr] StartX=-193.935 StartY=-20.6809 StartZ=0 EndX=-193.258 EndY=-19.2308 EndZ=0
    g9: LineSegment [constr] StartX=-193.935 StartY=-20.6809 StartZ=0 EndX=-195.385 EndY=-20.0047 EndZ=0
    g10: ArcOfCircle CenterX=-193.779 CenterY=-16.5607 CenterZ=0 NormalX=0 NormalY=0 NormalZ=1 AngleXU=0 Radius=1.6 StartAngle=5.84685 EndAngle=7.41765
    g11: GeomPoint [constr] X=-191.653 Y=-15.7868 Z=0
    g12: ArcOfCircle CenterX=-194.709 CenterY=-18.5546 CenterZ=0 NormalX=0 NormalY=0 NormalZ=1 AngleXU=0 Radius=1.6 StartAngle=4.27606 EndAngle=5.84685
    g13: GeomPoint [constr] X=-193.935 Y=-20.6809 Z=0
    g14: LineSegment StartX=-207.775 StartY=-46.8316 StartZ=0 EndX=-207.775 EndY=-50.8316 EndZ=0
    g15: LineSegment StartX=-207.775 StartY=-46.8316 StartZ=0 EndX=-203.775 EndY=-46.8316 EndZ=0
    g16: LineSegment StartX=-203.775 StartY=-46.8316 StartZ=0 EndX=-203.775 EndY=-50.8316 EndZ=0
    g17: LineSegment StartX=-207.775 StartY=-50.8316 StartZ=0 EndX=-203.775 EndY=-50.8316 EndZ=0
    g18: LineSegment StartX=-209.375 StartY=-52.4316 StartZ=0 EndX=-203.775 EndY=-52.4316 EndZ=0
    g19: LineSegment StartX=-202.175 StartY=-50.8316 StartZ=0 EndX=-202.175 EndY=-46.8316 EndZ=0
    g20: LineSegment StartX=-203.775 StartY=-45.2316 StartZ=0 EndX=-209.375 EndY=-45.2316 EndZ=0
    g21: LineSegment StartX=-209.375 StartY=-45.2316 StartZ=0 EndX=-209.375 EndY=-52.4316 EndZ=0
    g22: ArcOfCircle CenterX=-203.775 CenterY=-46.8316 CenterZ=0 NormalX=0 NormalY=0 NormalZ=1 AngleXU=0 Radius=1.6 StartAngle=1.8e-15 EndAngle=1.5708
    g23: GeomPoint [constr] X=-202.175 Y=-45.2316 Z=0
    g24: ArcOfCircle CenterX=-203.775 CenterY=-50.8316 CenterZ=0 NormalX=0 NormalY=0 NormalZ=1 AngleXU=0 Radius=1.6 StartAngle=4.71239 EndAngle=6.28319
    g25: GeomPoint [constr] X=-202.175 Y=-52.4316 Z=0
    g26: LineSegment [constr] StartX=-207.775 StartY=-50.4316 StartZ=0 EndX=-207.775 EndY=-50.8316 EndZ=0
  constraints (69):
    c: Coincident(g1,g0)
    c: Coincident(g2,g1)
    c: Coincident(g3,g2)
    c: Coincident(g3,g0)
    c: Parallel(g0,g2)
    c: Perpendicular(g3,g0)
    c: Perpendicular(g1,g0)
    c: Coincident(g5,g4)
    c: Coincident(g7,g4)
    c: Distance(g3) = 2.2
    c: Distance(g2) = 2.2
    c: Parallel(g6,g2)
    c: Parallel(g6,g4)
    c: Perpendicular(g5,g6)
    c: Perpendicular(g7,g6)
    c: Distance(g13,g11) = 5.4
    c: Distance(g5,g13) = 5.4
    c: Coincident(g9,g8)
    c: Distance(g8) = 1.6
    c: Distance(g9) = 1.6
    c: Perpendicular(g9,g8)
    c: Parallel(g8,g6)
    c: Coincident(g8,g13)
    c: Distance(g8,g1) = 1.6
    c: Distance(g9,g1) = 1.6
    c: Tangent(g0,g-5)
    c: Distance(g0,g-6) = 26.2
    c: PointOnObject(g11,g7)
    c: PointOnObject(g11,g6)
    c: Tangent(g7,g10) = -1.5708
    c: Tangent(g6,g10) = -1.5708
    c: PointOnObject(g13,g5)
    c: Tangent(g5,g12) = -1.5708
    c: Tangent(g6,g12) = -1.5708
    c: Equal(g10,g12)
    c: Coincident(g10,g2)
    c: Vertical(g14)
    c: Coincident(g15,g14)
    c: Horizontal(g15)
    c: Coincident(g16,g15)
    c: Vertical(g16)
    c: Coincident(g17,g14)
    c: Coincident(g17,g16)
    c: Horizontal(g17)
    c: Distance(g16) = 4
    c: Distance(g15) = 4
    c: Horizontal(g18)
    c: Vertical(g19)
    c: Horizontal(g20)
    c: Coincident(g21,g20)
    c: Coincident(g21,g18)
    c: Vertical(g21)
    c: Distance(g20,g23) = 7.2
    c: Distance(g25,g23) = 7.2
    c: DistanceY(g18,g14) = 1.6
    c: DistanceX(g18,g14) = 1.6
    c: PointOnObject(g23,g20)
    c: PointOnObject(g23,g19)
    c: Tangent(g20,g22) = -1.5708
    c: Tangent(g19,g22) = -1.5708
    c: PointOnObject(g25,g19)
    c: Tangent(g18,g24) = -1.5708
    c: Tangent(g19,g24) = -1.5708
    c: Equal(g22,g24)
    c: Coincident(g22,g15)
    c: Vertical(g26)
    c: Distance(g26) = 0.4
    c: Coincident(g26,g-4)
    c: Coincident(g14,g26)
FEATURE [Part::Extrusion] Extrude045  label="Extrude fermi per driver solenoide e alimentatore"
  Base = -> Sketch042
  Dir = (0,-1,2e-16)
  DirMode = 2
  FaceMakerClass = Part::FaceMakerBullseye
  FaceMakerMode = 3
  LengthFwd = 25.2
  LengthRev = 0
  Solid = true
  Symmetric = true
FEATURE [Sketcher::SketchObject] Sketch043  label="scavo pulizia fermo alimentatore"
  ArcFitTolerance = 1e-06
  AttachmentSupport = -> [XZ_Plane]
  ExternalGeometry = -> [Sketch042,Sketch036,Sketch037]
  FullyConstrained = true
  MakeInternals = false
  MapMode = 5
  Placement = pos=(0,0,0) rot=(1,0,0;1.5708rad)
  sketch-geometry (6):
    g0: LineSegment StartX=-209.375 StartY=-52.4316 StartZ=0 EndX=-209.375 EndY=-50.4316 EndZ=0
    g1: LineSegment StartX=-209.375 StartY=-50.4316 StartZ=0 EndX=-207.775 EndY=-50.4316 EndZ=0
    g2: LineSegment StartX=-207.775 StartY=-50.4316 StartZ=0 EndX=-207.775 EndY=-45.2316 EndZ=0
    g3: LineSegment StartX=-207.775 StartY=-45.2316 StartZ=0 EndX=-202.175 EndY=-45.2316 EndZ=0
    g4: LineSegment StartX=-202.175 StartY=-45.2316 StartZ=0 EndX=-202.175 EndY=-52.4316 EndZ=0
    g5: LineSegment StartX=-202.175 StartY=-52.4316 StartZ=0 EndX=-209.375 EndY=-52.4316 EndZ=0
  constraints (13):
    c: Vertical(g0)
    c: Coincident(g1,g0)
    c: Coincident(g2,g1)
    c: Coincident(g3,g2)
    c: Coincident(g4,g3)
    c: Coincident(g5,g4)
    c: Coincident(g5,g0)
    c: Horizontal(g5)
    c: Coincident(g0,g-6)
    c: Tangent(g1,g-8)
    c: Tangent(g2,g-4)
    c: Tangent(g3,g-7)
    c: Tangent(g4,g-3)
FEATURE [Part::Extrusion] Extrude046  label="Extrude scavo pulizia fermo alimentatore"
  Base = -> Sketch043
  Dir = (0,-1,2e-16)
  DirMode = 2
  FaceMakerClass = Part::FaceMakerBullseye
  FaceMakerMode = 3
  LengthFwd = 19.5
  LengthRev = 0
  Solid = true
  Symmetric = true
FEATURE [Sketcher::SketchObject] Sketch044  label="buchini per fissaggio oled"
  ArcFitTolerance = 1e-06
  AttachmentSupport = -> [YZ_Plane]
  ExternalGeometry = -> [Sketch]
  FullyConstrained = true
  MakeInternals = false
  MapMode = 5
  Placement = pos=(0,0,0) rot=(0.57735,0.57735,0.57735;2.0944rad)
  sketch-geometry (5):
    g0: LineSegment [constr] StartX=1.5e-14 StartY=67.3588 StartZ=0 EndX=0 EndY=64.3588 EndZ=0
    g1: LineSegment [constr] StartX=0 StartY=64.3588 StartZ=0 EndX=10.4 EndY=64.3588 EndZ=0
    g2: LineSegment [constr] StartX=0 StartY=64.3588 StartZ=0 EndX=-10.4 EndY=64.3588 EndZ=0
    g3: Circle CenterX=10.4 CenterY=64.3588 CenterZ=0 NormalX=0 NormalY=0 NormalZ=1 AngleXU=0 Radius=1.5
    g4: Circle CenterX=-10.4 CenterY=64.3588 CenterZ=0 NormalX=0 NormalY=0 NormalZ=1 AngleXU=0 Radius=1.5
  constraints (13):
    c: Distance(g0) = 3
    c: PointOnObject(g0,g-2)
    c: Coincident(g1,g0)
    c: Horizontal(g1)
    c: Coincident(g2,g0)
    c: Horizontal(g2)
    c: DistanceX(g1,g1) = 10.4
    c: Coincident(g3,g1)
    c: Diameter(g4) = 3
    c: Coincident(g4,g2)
    c: Coincident(g0,g-7)
    c: Equal(g1,g2)
    c: Equal(g4,g3)
FEATURE [Part::Extrusion] Extrude047  label="Extrude buchini per fissaggio oled"
  Base = -> Sketch044
  Dir = (1,0,0)
  DirMode = 2
  FaceMakerClass = Part::FaceMakerBullseye
  FaceMakerMode = 3
  LengthFwd = 10
  LengthRev = 0
  Placement = pos=(-186,0,0) rot=(0,0,1;0rad)
  Solid = true
  Symmetric = false
FEATURE [Sketcher::SketchObject] Sketch046  label="scavo 5x5 neopixel"
  ArcFitTolerance = 1e-06
  AttachmentSupport = -> [YZ_Plane002]
  FullyConstrained = true
  MakeInternals = false
  MapMode = 5
  Placement = pos=(0,0,0) rot=(0.57735,0.57735,0.57735;2.0944rad)
  sketch-geometry (4):
    g0: LineSegment StartX=-2.7 StartY=2.7 StartZ=0 EndX=2.7 EndY=2.7 EndZ=0
    g1: LineSegment StartX=2.7 StartY=2.7 StartZ=0 EndX=2.7 EndY=-2.7 EndZ=0
    g2: LineSegment StartX=2.7 StartY=-2.7 StartZ=0 EndX=-2.7 EndY=-2.7 EndZ=0
    g3: LineSegment StartX=-2.7 StartY=-2.7 StartZ=0 EndX=-2.7 EndY=2.7 EndZ=0
  constraints (11):
    c: Horizontal(g0)
    c: Coincident(g1,g0)
    c: Vertical(g1)
    c: Coincident(g2,g1)
    c: Horizontal(g2)
    c: Coincident(g3,g2)
    c: Coincident(g3,g0)
    c: Vertical(g3)
    c: DistanceX(g0,g0) = 5.4
    c: DistanceY(g1,g1) = 5.4
    c: Symmetric(g0,g1,g-1)
FEATURE [Sketcher::SketchObject] Sketch047  label="scavo 10x10 neopixel corpo"
  ArcFitTolerance = 1e-06
  AttachmentOffset = pos=(0,0,1) rot=(0,0,1;0rad)
  AttachmentSupport = -> [YZ_Plane002]
  FullyConstrained = true
  MakeInternals = false
  MapMode = 5
  Placement = pos=(1,0,0) rot=(0.57735,0.57735,0.57735;2.0944rad)
  sketch-geometry (4):
    g0: LineSegment StartX=-5 StartY=5.1 StartZ=0 EndX=5 EndY=5.1 EndZ=0
    g1: LineSegment StartX=5 StartY=5.1 StartZ=0 EndX=5 EndY=-5.1 EndZ=0
    g2: LineSegment StartX=5 StartY=-5.1 StartZ=0 EndX=-5 EndY=-5.1 EndZ=0
    g3: LineSegment StartX=-5 StartY=-5.1 StartZ=0 EndX=-5 EndY=5.1 EndZ=0
  constraints (11):
    c: Horizontal(g0)
    c: Coincident(g1,g0)
    c: Vertical(g1)
    c: Coincident(g2,g1)
    c: Horizontal(g2)
    c: Coincident(g3,g2)
    c: Coincident(g3,g0)
    c: Vertical(g3)
    c: DistanceX(g0,g0) = 10
    c: DistanceY(g1,g1) = 10.2
    c: Symmetric(g0,g2,g-1)
FEATURE [Sketcher::SketchObject] Sketch048  label="buco per perno blocco neopixel"
  ArcFitTolerance = 1e-06
  AttachmentSupport = -> [XZ_Plane002]
  FullyConstrained = true
  MakeInternals = false
  MapMode = 5
  Placement = pos=(0,0,0) rot=(1,0,0;1.5708rad)
  sketch-geometry (4):
    g0: LineSegment StartX=3 StartY=1.2 StartZ=0 EndX=3 EndY=-1.2 EndZ=0
    g1: LineSegment StartX=3 StartY=-1.2 StartZ=0 EndX=5.4 EndY=-1.2 EndZ=0
    g2: LineSegment StartX=5.4 StartY=-1.2 StartZ=0 EndX=5.4 EndY=1.2 EndZ=0
    g3: LineSegment StartX=5.4 StartY=1.2 StartZ=0 EndX=3 EndY=1.2 EndZ=0
  constraints (11):
    c: Coincident(g1,g0)
    c: Horizontal(g1)
    c: Coincident(g2,g1)
    c: Vertical(g2)
    c: Coincident(g3,g2)
    c: Coincident(g3,g0)
    c: Horizontal(g3)
    c: DistanceX(g1,g1) = 2.4
    c: DistanceY(g2,g2) = 2.4
    c: Symmetric(g0,g0,g-1)
    c: DistanceX(g-1,g0) = 3
FEATURE [Sketcher::SketchObject] Sketch045  label="blocco principale per neopixel"
  ArcFitTolerance = 1e-06
  AttachmentSupport = -> [XZ_Plane002]
  ExternalGeometry = -> [Sketch048]
  FullyConstrained = true
  MakeInternals = false
  MapMode = 5
  Placement = pos=(0,0,0) rot=(1,0,0;1.5708rad)
  sketch-geometry (6):
    g0: LineSegment StartX=0 StartY=5.1 StartZ=0 EndX=0 EndY=-5.1 EndZ=0
    g1: LineSegment StartX=0 StartY=-5.1 StartZ=0 EndX=3 EndY=-5.1 EndZ=0
    g2: LineSegment StartX=7 StartY=-1.1 StartZ=0 EndX=7 EndY=5.1 EndZ=0
    g3: LineSegment StartX=7 StartY=5.1 StartZ=0 EndX=0 EndY=5.1 EndZ=0
    g4: ArcOfCircle CenterX=3 CenterY=-1.1 CenterZ=0 NormalX=0 NormalY=0 NormalZ=1 AngleXU=0 Radius=4 StartAngle=4.71239 EndAngle=6.28319
    g5: GeomPoint [constr] X=7 Y=-5.1 Z=0
  constraints (15):
    c: Vertical(g0)
    c: Coincident(g1,g0)
    c: Horizontal(g1)
    c: Vertical(g2)
    c: Coincident(g3,g2)
    c: Coincident(g3,g0)
    c: Horizontal(g3)
    c: DistanceY(g0,g0) = 10.2
    c: Symmetric(g0,g0,g-1)
    c: DistanceX(g3,g3) = 7
    c: PointOnObject(g5,g2)
    c: PointOnObject(g5,g1)
    c: Tangent(g2,g4) = -1.5708
    c: Tangent(g1,g4) = -1.5708
    c: DistanceX(g-3,g1) = 0
FEATURE [Sketcher::SketchObject] Sketch049  label="rinforzi esterni per corpo neopoixel"
  ArcFitTolerance = 1e-06
  AttachmentSupport = -> [XZ_Plane002]
  ExternalGeometry = -> [Sketch045]
  FullyConstrained = true
  MakeInternals = false
  MapMode = 5
  Placement = pos=(0,0,0) rot=(1,0,0;1.5708rad)
  sketch-geometry (8):
    g0: LineSegment StartX=1 StartY=-4.1 StartZ=0 EndX=2 EndY=-4.1 EndZ=0
    g1: LineSegment StartX=2 StartY=-4.1 StartZ=0 EndX=2 EndY=-5.1 EndZ=0
    g2: LineSegment StartX=2 StartY=-5.1 StartZ=0 EndX=1 EndY=-5.1 EndZ=0
    g3: LineSegment StartX=1 StartY=-5.1 StartZ=0 EndX=1 EndY=-4.1 EndZ=0
    g4: LineSegment StartX=1 StartY=5.1 StartZ=0 EndX=2 EndY=5.1 EndZ=0
    g5: LineSegment StartX=2 StartY=5.1 StartZ=0 EndX=2 EndY=4.1 EndZ=0
    g6: LineSegment StartX=2 StartY=4.1 StartZ=0 EndX=1 EndY=4.1 EndZ=0
    g7: LineSegment StartX=1 StartY=4.1 StartZ=0 EndX=1 EndY=5.1 EndZ=0
  constraints (24):
    c: Horizontal(g0)
    c: Coincident(g1,g0)
    c: Vertical(g1)
    c: Coincident(g2,g1)
    c: Horizontal(g2)
    c: Coincident(g3,g2)
    c: Coincident(g3,g0)
    c: Vertical(g3)
    c: Horizontal(g4)
    c: Coincident(g5,g4)
    c: Vertical(g5)
    c: Coincident(g6,g5)
    c: Horizontal(g6)
    c: Coincident(g7,g6)
    c: Coincident(g7,g4)
    c: Vertical(g7)
    c: DistanceX(g4,g4) = 1
    c: DistanceY(g5,g5) = 1
    c: DistanceX(g0,g0) = 1
    c: DistanceY(g1,g1) = 1
    c: DistanceX(g-3,g4) = 1
    c: DistanceY(g-3,g4) = 0
    c: DistanceX(g-4,g2) = 1
    c: DistanceY(g2,g-4) = 0
FEATURE [Sketcher::SketchObject] Sketch052  label="scavo saldature driver solenoide"
  ArcFitTolerance = 1e-06
  AttachmentSupport = -> [XZ_Plane]
  ExternalGeometry = -> [Sketch038]
  FullyConstrained = true
  MakeInternals = false
  MapMode = 5
  Placement = pos=(0,0,0) rot=(1,0,0;1.5708rad)
  sketch-geometry (4):
    g0: LineSegment StartX=-196.56 StartY=-9.74706 StartZ=0 EndX=-198.25 EndY=-13.3723 EndZ=0
    g1: LineSegment StartX=-198.25 StartY=-13.3723 StartZ=0 EndX=-196.8 EndY=-14.0485 EndZ=0
    g2: LineSegment StartX=-196.8 StartY=-14.0485 StartZ=0 EndX=-195.11 EndY=-10.4232 EndZ=0
    g3: LineSegment StartX=-195.11 StartY=-10.4232 StartZ=0 EndX=-196.56 EndY=-9.74706 EndZ=0
  constraints (11):
    c: Coincident(g1,g0)
    c: Coincident(g2,g1)
    c: Coincident(g3,g2)
    c: Coincident(g3,g0)
    c: Parallel(g2,g0)
    c: Perpendicular(g2,g3)
    c: Perpendicular(g1,g2,g1) = 1.5708
    c: Parallel(g2,g-3)
    c: Distance(g2) = 4
    c: Distance(g3) = 1.6
    c: Coincident(g2,g-3)
FEATURE [Part::Extrusion] Extrude055  label="Extrude scavo saldature driver solenoide"
  Base = -> Sketch052
  Dir = (0,-1,2e-16)
  DirMode = 2
  FaceMakerClass = Part::FaceMakerBullseye
  FaceMakerMode = 3
  LengthFwd = 6
  LengthRev = 0
  Solid = true
  Symmetric = true
FEATURE [Sketcher::SketchObject] Sketch053  label="scavo saldature rumble"
  ArcFitTolerance = 1e-06
  AttachmentSupport = -> [XZ_Plane]
  ExternalGeometry = -> [Sketch019]
  FullyConstrained = true
  MakeInternals = false
  MapMode = 5
  Placement = pos=(0,0,0) rot=(1,0,0;1.5708rad)
  sketch-geometry (4):
    g0: LineSegment StartX=-165.31 StartY=-44.1173 StartZ=0 EndX=-166.547 EndY=-47.9216 EndZ=0
    g1: LineSegment StartX=-166.547 StartY=-47.9216 StartZ=0 EndX=-165.405 EndY=-48.2924 EndZ=0
    g2: LineSegment StartX=-165.405 StartY=-48.2924 StartZ=0 EndX=-164.169 EndY=-44.4881 EndZ=0
    g3: LineSegment StartX=-164.169 StartY=-44.4881 StartZ=0 EndX=-165.31 EndY=-44.1173 EndZ=0
  constraints (11):
    c: Coincident(g1,g0)
    c: Coincident(g2,g1)
    c: Coincident(g3,g2)
    c: Coincident(g3,g0)
    c: Parallel(g0,g2)
    c: Perpendicular(g3,g0)
    c: Perpendicular(g1,g0)
    c: Parallel(g0,g-3)
    c: Distance(g0) = 4
    c: Distance(g1) = 1.2
    c: Coincident(g0,g-3)
FEATURE [Part::Extrusion] Extrude056  label="Extrude scavo saldature rumble"
  Base = -> Sketch053
  Dir = (0,-1,2e-16)
  DirMode = 2
  FaceMakerClass = Part::FaceMakerBullseye
  FaceMakerMode = 3
  LengthFwd = 8.4
  LengthRev = 0
  Solid = true
  Symmetric = true
FEATURE [Sketcher::SketchObject] Sketch054  label="scavo saldature alimentatore connettore USB"
  ArcFitTolerance = 1e-06
  AttachmentSupport = -> [XZ_Plane]
  ExternalGeometry = -> [Sketch037]
  FullyConstrained = true
  MakeInternals = false
  MapMode = 5
  Placement = pos=(0,0,0) rot=(1,0,0;1.5708rad)
  sketch-geometry (4):
    g0: LineSegment StartX=-209.575 StartY=-80.4316 StartZ=0 EndX=-210.375 EndY=-80.4316 EndZ=0
    g1: LineSegment StartX=-210.375 StartY=-80.4316 StartZ=0 EndX=-210.375 EndY=-72.4316 EndZ=0
    g2: LineSegment StartX=-210.375 StartY=-72.4316 StartZ=0 EndX=-209.575 EndY=-72.4316 EndZ=0
    g3: LineSegment StartX=-209.575 StartY=-72.4316 StartZ=0 EndX=-209.575 EndY=-80.4316 EndZ=0
  constraints (11):
    c: Horizontal(g0)
    c: Coincident(g1,g0)
    c: Vertical(g1)
    c: Coincident(g2,g1)
    c: Horizontal(g2)
    c: Coincident(g3,g2)
    c: Coincident(g3,g0)
    c: Vertical(g3)
    c: DistanceX(g0,g0) = 0.8
    c: DistanceY(g3,g3) = 8
    c: Coincident(g0,g-4)
FEATURE [Part::Extrusion] Extrude057  label="Extrude scavo saldature alimentatore connettore USB"
  Base = -> Sketch054
  Dir = (0,-1,2e-16)
  DirMode = 2
  FaceMakerClass = Part::FaceMakerBullseye
  FaceMakerMode = 3
  LengthFwd = 11
  LengthRev = 0
  Solid = true
  Symmetric = true
FEATURE [Sketcher::SketchObject] Sketch055  label="buco interno per micro switch"
  ArcFitTolerance = 1e-06
  AttachmentSupport = -> [XZ_Plane]
  ExternalGeometry = -> [Sketch]
  FullyConstrained = true
  MakeInternals = false
  MapMode = 5
  Placement = pos=(0,0,0) rot=(1,0,0;1.5708rad)
  sketch-geometry (11):
    g0: LineSegment [constr] StartX=-194.483 StartY=34.2854 StartZ=0 EndX=-196.022 EndY=30.0568 EndZ=0
    g1: LineSegment [constr] StartX=-196.022 StartY=30.0568 StartZ=0 EndX=-197.561 EndY=25.8282 EndZ=0
    g2: LineSegment [constr] StartX=-196.022 StartY=30.0568 StartZ=0 EndX=-194.143 EndY=29.3727 EndZ=0
    g3: LineSegment [constr] StartX=-196.022 StartY=30.0568 StartZ=0 EndX=-197.902 EndY=30.7408 EndZ=0
    g4: LineSegment StartX=-196.362 StartY=34.9694 StartZ=0 EndX=-192.604 EndY=33.6014 EndZ=0
    g5: LineSegment StartX=-199.441 StartY=26.5122 StartZ=0 EndX=-195.682 EndY=25.1441 EndZ=0
    g6: LineSegment StartX=-192.604 StartY=33.6014 StartZ=0 EndX=-195.682 EndY=25.1441 EndZ=0
    g7: LineSegment StartX=-196.362 StartY=34.9694 StartZ=0 EndX=-199.441 EndY=26.5122 EndZ=0
    g8: GeomPoint [constr] X=-187.821 Y=29.2 Z=0
    g9: LineSegment [constr] StartX=-188.505 StartY=27.3206 StartZ=0 EndX=-196.022 EndY=30.0568 EndZ=0
    g10: LineSegment [constr] StartX=-187.821 StartY=29.2 StartZ=0 EndX=-188.505 EndY=27.3206 EndZ=0
  constraints (27):
    c: Coincident(g2,g0)
    c: Parallel(g0,g-3)
    c: Tangent(g1,g0) = -1.5708
    c: Perpendicular(g0,g2)
    c: Tangent(g2,g3)
    c: Distance(g0,g1) = 9
    c: Equal(g0,g1)
    c: Distance(g3,g2) = 4
    c: Equal(g2,g3)
    c: Parallel(g3,g4)
    c: Symmetric(g4,g4,g0)
    c: Parallel(g6,g1)
    c: Parallel(g7,g1)
    c: Symmetric(g6,g6,g2)
    c: Symmetric(g5,g5,g1)
    c: Symmetric(g7,g7,g3)
    c: Coincident(g7,g4)
    c: Coincident(g6,g4)
    c: Coincident(g5,g6)
    c: Symmetric(g-3,g-3,g8)
    c: Perpendicular(g-3,g9)
    c: Distance(g9) = 8
    c: Coincident(g3,g9)
    c: Coincident(g10,g8)
    c: Parallel(g10,g-3)
    c: Distance(g10) = 2
    c: Coincident(g10,g9)
FEATURE [Sketcher::SketchObject] Sketch056  label="buco esterno per micro switch"
  ArcFitTolerance = 1e-06
  AttachmentSupport = -> [XZ_Plane]
  ExternalGeometry = -> [Sketch055]
  FullyConstrained = true
  MakeInternals = false
  MapMode = 5
  Placement = pos=(0,0,0) rot=(1,0,0;1.5708rad)
  sketch-geometry (17):
    g0: GeomPoint [constr] X=-194.143 Y=29.3727 Z=0
    g1: GeomPoint [constr] X=-194.483 Y=34.2854 Z=0
    g2: GeomPoint [constr] X=-197.902 Y=30.7408 Z=0
    g3: GeomPoint [constr] X=-197.561 Y=25.8282 Z=0
    g4: GeomPoint [constr] X=-196.022 Y=30.0568 Z=0
    g5: LineSegment [constr] StartX=-194.483 StartY=34.2854 StartZ=0 EndX=-196.022 EndY=30.0568 EndZ=0
    g6: LineSegment [constr] StartX=-196.022 StartY=30.0568 StartZ=0 EndX=-197.561 EndY=25.8282 EndZ=0
    g7: LineSegment [constr] StartX=-197.902 StartY=30.7408 StartZ=0 EndX=-196.022 EndY=30.0568 EndZ=0
    g8: LineSegment [constr] StartX=-196.022 StartY=30.0568 StartZ=0 EndX=-194.143 EndY=29.3727 EndZ=0
    g9: LineSegment [constr] StartX=-195.338 StartY=31.9362 StartZ=0 EndX=-196.022 EndY=30.0568 EndZ=0
    g10: LineSegment [constr] StartX=-196.022 StartY=30.0568 StartZ=0 EndX=-196.706 EndY=28.1774 EndZ=0
    g11: LineSegment [constr] StartX=-196.022 StartY=30.0568 StartZ=0 EndX=-196.821 EndY=30.3475 EndZ=0
    g12: LineSegment [constr] StartX=-196.022 StartY=30.0568 StartZ=0 EndX=-195.223 EndY=29.7661 EndZ=0
    g13: LineSegment StartX=-194.539 StartY=31.6454 StartZ=0 EndX=-195.907 EndY=27.8867 EndZ=0
    g14: LineSegment StartX=-196.137 StartY=32.2269 StartZ=0 EndX=-197.505 EndY=28.4681 EndZ=0
    g15: LineSegment StartX=-196.137 StartY=32.2269 StartZ=0 EndX=-194.539 EndY=31.6454 EndZ=0
    g16: LineSegment StartX=-197.505 StartY=28.4681 StartZ=0 EndX=-195.907 EndY=27.8867 EndZ=0
  constraints (34):
    c: Symmetric(g-5,g-5,g1)
    c: Symmetric(g-5,g-6,g0)
    c: Symmetric(g-6,g-6,g3)
    c: Symmetric(g-5,g-6,g2)
    c: Coincident(g5,g1)
    c: Coincident(g5,g4)
    c: Coincident(g6,g4)
    c: Coincident(g6,g3)
    c: Equal(g5,g6)
    c: Coincident(g7,g2)
    c: Coincident(g7,g4)
    c: Coincident(g8,g4)
    c: Coincident(g8,g0)
    c: Equal(g7,g8)
    c: Coincident(g11,g9)
    c: Coincident(g12,g9)
    c: Tangent(g10,g9) = -1.5708
    c: Perpendicular(g11,g9)
    c: Parallel(g9,g-4)
    c: Equal(g9,g10)
    c: Parallel(g12,g11)
    c: Equal(g11,g12)
    c: Distance(g11,g12) = 1.7
    c: Distance(g9,g10) = 4
    c: Symmetric(g13,g13,g12)
    c: Parallel(g13,g9)
    c: Symmetric(g14,g14,g11)
    c: Symmetric(g15,g15,g9)
    c: Parallel(g15,g11)
    c: Symmetric(g16,g16,g10)
    c: Coincident(g16,g14)
    c: Coincident(g15,g14)
    c: Coincident(g13,g15)
    c: Coincident(g9,g4)
FEATURE [Sketcher::SketchObject] Sketch057  label="buco interno per SWITCH"
  ArcFitTolerance = 1e-06
  AttachmentSupport = -> [XZ_Plane]
  ExternalGeometry = -> [Sketch]
  FullyConstrained = true
  MakeInternals = false
  MapMode = 5
  Placement = pos=(0,0,0) rot=(1,0,0;1.5708rad)
  sketch-geometry (10):
    g0: GeomPoint [constr] X=-187.821 Y=29.2 Z=0
    g1: LineSegment [constr] StartX=-188.505 StartY=27.3206 StartZ=0 EndX=-193.203 EndY=29.0307 EndZ=0
    g2: LineSegment [constr] StartX=-190.809 StartY=35.6086 StartZ=0 EndX=-195.597 EndY=22.4529 EndZ=0
    g3: GeomPoint [constr] X=-193.203 Y=29.0307 Z=0
    g4: LineSegment [constr] StartX=-196.492 StartY=30.2278 StartZ=0 EndX=-189.914 EndY=27.8336 EndZ=0
    g5: LineSegment StartX=-194.098 StartY=36.8056 StartZ=0 EndX=-187.52 EndY=34.4115 EndZ=0
    g6: LineSegment StartX=-194.098 StartY=36.8056 StartZ=0 EndX=-198.886 EndY=23.6499 EndZ=0
    g7: LineSegment StartX=-187.52 StartY=34.4115 StartZ=0 EndX=-192.308 EndY=21.2558 EndZ=0
    g8: LineSegment StartX=-198.886 StartY=23.6499 StartZ=0 EndX=-192.308 EndY=21.2558 EndZ=0
    g9: LineSegment [constr] StartX=-187.821 StartY=29.2 StartZ=0 EndX=-188.505 EndY=27.3206 EndZ=0
  constraints (23):
    c: Symmetric(g-3,g-3,g0)
    c: Perpendicular(g1,g-3)
    c: Parallel(g2,g-3)
    c: Symmetric(g2,g2,g3)
    c: Perpendicular(g2,g4)
    c: Symmetric(g4,g4,g3)
    c: Distance(g2) = 14
    c: Distance(g4) = 7
    c: Distance(g1) = 5
    c: Parallel(g5,g4)
    c: Parallel(g7,g2)
    c: Symmetric(g5,g5,g2)
    c: Symmetric(g6,g6,g4)
    c: Symmetric(g7,g7,g4)
    c: Symmetric(g8,g8,g2)
    c: Coincident(g6,g5)
    c: Coincident(g7,g5)
    c: Coincident(g8,g7)
    c: Coincident(g3,g1)
    c: Coincident(g9,g0)
    c: Parallel(g9,g-3)
    c: Distance(g9) = 2
    c: Coincident(g1,g9)
FEATURE [Sketcher::SketchObject] Sketch058  label="buco esterno per SWITCH"
  ArcFitTolerance = 1e-06
  AttachmentSupport = -> [XZ_Plane]
  ExternalGeometry = -> [Sketch057]
  FullyConstrained = true
  MakeInternals = false
  MapMode = 5
  Placement = pos=(0,0,0) rot=(1,0,0;1.5708rad)
  sketch-geometry (12):
    g0: GeomPoint [constr] X=-190.809 Y=35.6086 Z=0
    g1: GeomPoint [constr] X=-196.492 Y=30.2278 Z=0
    g2: GeomPoint [constr] X=-189.914 Y=27.8336 Z=0
    g3: GeomPoint [constr] X=-195.597 Y=22.4529 Z=0
    g4: GeomPoint [constr] X=-193.203 Y=29.0307 Z=0
    g5: LineSegment [constr] StartX=-192.006 StartY=32.3196 StartZ=0 EndX=-194.4 EndY=25.7418 EndZ=0
    g6: GeomPoint [constr] X=-193.203 Y=29.0307 Z=0
    g7: LineSegment [constr] StartX=-195.082 StartY=29.7148 StartZ=0 EndX=-191.324 EndY=28.3467 EndZ=0
    g8: LineSegment StartX=-193.885 StartY=33.0037 StartZ=0 EndX=-190.127 EndY=31.6356 EndZ=0
    g9: LineSegment StartX=-190.127 StartY=31.6356 StartZ=0 EndX=-192.521 EndY=25.0578 EndZ=0
    g10: LineSegment StartX=-196.28 StartY=26.4258 StartZ=0 EndX=-192.521 EndY=25.0578 EndZ=0
    g11: LineSegment StartX=-193.885 StartY=33.0037 StartZ=0 EndX=-196.28 EndY=26.4258 EndZ=0
  constraints (21):
    c: Symmetric(g-6,g-6,g3)
    c: Symmetric(g-4,g-6,g2)
    c: Symmetric(g-5,g-4,g0)
    c: Symmetric(g-5,g-6,g1)
    c: Symmetric(g1,g2,g4)
    c: Parallel(g5,g-4)
    c: Symmetric(g5,g5,g6)
    c: Perpendicular(g7,g5)
    c: Symmetric(g7,g7,g6)
    c: Distance(g5) = 7
    c: Distance(g7) = 4
    c: Parallel(g8,g7)
    c: Parallel(g11,g5)
    c: Symmetric(g8,g8,g5)
    c: Symmetric(g9,g9,g7)
    c: Symmetric(g10,g10,g5)
    c: Symmetric(g11,g11,g7)
    c: Coincident(g11,g8)
    c: Coincident(g9,g8)
    c: Coincident(g9,g10)
    c: Coincident(g6,g4)
FEATURE [Part::Extrusion] Extrude060  label="Extrude buco interno per SWITCH destro"
  Base = -> Sketch057
  Dir = (0,-1,2e-16)
  DirMode = 2
  FaceMakerClass = Part::FaceMakerBullseye
  FaceMakerMode = 3
  LengthFwd = 13.2
  LengthRev = 0
  Placement = pos=(0,2.6,0) rot=(0,0,1;0rad)
  Solid = true
  Symmetric = false
FEATURE [Part::Extrusion] Extrude061  label="Extrude buco esterno per SWITCH destro"
  Base = -> Sketch058
  Dir = (0,-1,2e-16)
  DirMode = 2
  FaceMakerClass = Part::FaceMakerBullseye
  FaceMakerMode = 3
  LengthFwd = 2
  LengthRev = 0
  Placement = pos=(0,-10.6,0) rot=(0,0,1;0rad)
  Solid = true
  Symmetric = false
FEATURE [Sketcher::SketchObject] Sketch059  label="buco per spazio introduzione SWITCH"
  ArcFitTolerance = 1e-06
  AttachmentSupport = -> [XZ_Plane]
  ExternalGeometry = -> [Sketch057,Sketch010]
  FullyConstrained = true
  MakeInternals = false
  MapMode = 5
  Placement = pos=(0,0,0) rot=(1,0,0;1.5708rad)
  sketch-geometry (8):
    g0: LineSegment [constr] StartX=-201.368 StartY=36.3521 StartZ=0 EndX=-195.094 EndY=34.0687 EndZ=0
    g1: LineSegment [constr] StartX=-194.098 StartY=36.8056 StartZ=0 EndX=-195.094 EndY=34.0687 EndZ=0
    g2: LineSegment StartX=-198.658 StartY=24.2771 StartZ=0 EndX=-199.654 EndY=21.5401 EndZ=0
    g3: LineSegment StartX=-199.654 StartY=21.5401 StartZ=0 EndX=-181.196 EndY=14.822 EndZ=0
    g4: LineSegment StartX=-181.196 StartY=14.822 StartZ=0 EndX=-180.2 EndY=17.559 EndZ=0
    g5: LineSegment StartX=-180.2 StartY=17.559 StartZ=0 EndX=-198.658 EndY=24.2771 EndZ=0
    g6: LineSegment [constr] StartX=-204.932 StartY=26.5605 StartZ=0 EndX=-198.658 EndY=24.2771 EndZ=0
    g7: LineSegment [constr] StartX=-198.658 StartY=24.2771 StartZ=0 EndX=-199.654 EndY=21.5401 EndZ=0
  constraints (20):
    c: Parallel(g1,g-3)
    c: Parallel(g0,g-4)
    c: Coincident(g0,g-4)
    c: Coincident(g1,g-3)
    c: Coincident(g0,g1)
    c: Coincident(g3,g2)
    c: Coincident(g4,g3)
    c: Coincident(g5,g4)
    c: Coincident(g5,g2)
    c: Parallel(g5,g-5)
    c: Parallel(g3,g-5)
    c: Parallel(g4,g-6)
    c: DistanceX(g-6,g4) = 0
    c: Coincident(g6,g-5)
    c: Equal(g6,g0)
    c: Coincident(g7,g6)
    c: Equal(g7,g1)
    c: Tangent(g7,g-3)
    c: Coincident(g2,g6)
    c: Coincident(g2,g7)
FEATURE [Part::Extrusion] Extrude062  label="Extrude buco per spazio introduzione SWITCH"
  Base = -> Sketch059
  Dir = (0,-1,2e-16)
  DirMode = 2
  FaceMakerClass = Part::FaceMakerBullseye
  FaceMakerMode = 3
  LengthFwd = 13.2
  LengthRev = 0
  Solid = true
  Symmetric = true
FEATURE [Part::Extrusion] Extrude063  label="Extrude buco interno per SWITCH sinistro"
  Base = -> Sketch057
  Dir = (0,-1,2e-16)
  DirMode = 2
  FaceMakerClass = Part::FaceMakerBullseye
  FaceMakerMode = 3
  LengthFwd = 13.2
  LengthRev = 0
  Placement = pos=(0,10.6,0) rot=(0,0,1;0rad)
  Solid = true
  Symmetric = false
FEATURE [Part::Extrusion] Extrude064  label="Extrude buco esterno per SWITCH sinistro"
  Base = -> Sketch058
  Dir = (0,-1,2e-16)
  DirMode = 2
  FaceMakerClass = Part::FaceMakerBullseye
  FaceMakerMode = 3
  LengthFwd = 2
  LengthRev = 0
  Placement = pos=(0,12.6,0) rot=(0,0,1;0rad)
  Solid = true
  Symmetric = false
FEATURE [Sketcher::SketchObject] Sketch061  label="struttura esterna blocco switch"
  ArcFitTolerance = 1e-06
  AttachmentSupport = -> [XZ_Plane003]
  FullyConstrained = true
  MakeInternals = false
  MapMode = 5
  Placement = pos=(0,0,0) rot=(1,0,0;1.5708rad)
  sketch-geometry (5):
    g0: LineSegment StartX=-1 StartY=-5.1 StartZ=0 EndX=1 EndY=-5.1 EndZ=0
    g1: LineSegment StartX=1 StartY=-5.1 StartZ=0 EndX=1 EndY=5.1 EndZ=0
    g2: LineSegment StartX=1 StartY=5.1 StartZ=0 EndX=-1 EndY=5.1 EndZ=0
    g3: LineSegment StartX=-1 StartY=5.1 StartZ=0 EndX=-1 EndY=-5.1 EndZ=0
    g4: GeomPoint [constr] X=0 Y=0 Z=0
  constraints (12):
    c: Coincident(g0,g1)
    c: Coincident(g1,g2)
    c: Coincident(g2,g3)
    c: Coincident(g3,g0)
    c: Horizontal(g0)
    c: Horizontal(g2)
    c: Vertical(g1)
    c: Vertical(g3)
    c: Symmetric(g2,g0,g4)
    c: Distance(g1,g3) = 2
    c: Distance(g0,g2) = 10.2
    c: Coincident(g4,g-1)
FEATURE [Sketcher::SketchObject] Sketch062  label="struttura interna blocco switch"
  ArcFitTolerance = 1e-06
  AttachmentSupport = -> [XZ_Plane003]
  ExternalGeometry = -> [Sketch061]
  FullyConstrained = true
  MakeInternals = false
  MapMode = 5
  Placement = pos=(0,0,0) rot=(1,0,0;1.5708rad)
  sketch-geometry (5):
    g0: LineSegment StartX=-1 StartY=3.1 StartZ=0 EndX=-1 EndY=-3.1 EndZ=0
    g1: LineSegment StartX=-1 StartY=-3.1 StartZ=0 EndX=1 EndY=-3.1 EndZ=0
    g2: LineSegment StartX=1 StartY=-3.1 StartZ=0 EndX=1 EndY=3.1 EndZ=0
    g3: LineSegment StartX=1 StartY=3.1 StartZ=0 EndX=-1 EndY=3.1 EndZ=0
    g4: GeomPoint [constr] X=0 Y=0 Z=0
  constraints (12):
    c: Coincident(g0,g1)
    c: Coincident(g1,g2)
    c: Coincident(g2,g3)
    c: Coincident(g3,g0)
    c: Vertical(g0)
    c: Vertical(g2)
    c: Horizontal(g1)
    c: Horizontal(g3)
    c: Symmetric(g2,g0,g4)
    c: Coincident(g4,g-1)
    c: Distance(g0) = 6.2
    c: Equal(g3,g-3)
FEATURE [Sketcher::SketchObject] Sketch063  label="blocchi tra switch"
  ArcFitTolerance = 1e-06
  AttachmentSupport = -> [XZ_Plane003]
  ExternalGeometry = -> [Sketch061,Sketch062]
  FullyConstrained = true
  MakeInternals = false
  MapMode = 5
  Placement = pos=(0,0,0) rot=(1,0,0;1.5708rad)
  sketch-geometry (8):
    g0: LineSegment StartX=-3 StartY=5.1 StartZ=0 EndX=-1 EndY=5.1 EndZ=0
    g1: LineSegment StartX=-1 StartY=5.1 StartZ=0 EndX=-1 EndY=3.1 EndZ=0
    g2: LineSegment StartX=-1 StartY=3.1 StartZ=0 EndX=-3 EndY=3.1 EndZ=0
    g3: LineSegment StartX=-3 StartY=3.1 StartZ=0 EndX=-3 EndY=5.1 EndZ=0
    g4: LineSegment StartX=-3 StartY=-3.1 StartZ=0 EndX=-1 EndY=-3.1 EndZ=0
    g5: LineSegment StartX=-1 StartY=-3.1 StartZ=0 EndX=-1 EndY=-5.1 EndZ=0
    g6: LineSegment StartX=-1 StartY=-5.1 StartZ=0 EndX=-3 EndY=-5.1 EndZ=0
    g7: LineSegment StartX=-3 StartY=-5.1 StartZ=0 EndX=-3 EndY=-3.1 EndZ=0
  constraints (20):
    c: Horizontal(g0)
    c: Coincident(g1,g0)
    c: Coincident(g2,g1)
    c: Horizontal(g2)
    c: Coincident(g3,g2)
    c: Coincident(g3,g0)
    c: Vertical(g3)
    c: Horizontal(g4)
    c: Coincident(g5,g4)
    c: Coincident(g6,g5)
    c: Horizontal(g6)
    c: Coincident(g7,g6)
    c: Coincident(g7,g4)
    c: Vertical(g7)
    c: Coincident(g0,g-4)
    c: Coincident(g1,g-5)
    c: Coincident(g4,g-6)
    c: Coincident(g5,g-7)
    c: Distance(g0) = 2
    c: Distance(g4) = 2
FEATURE [Sketcher::SketchObject] Sketch066  label="piano per rampino"
  ArcFitTolerance = 1e-06
  AttachmentSupport = -> [XZ_Plane002]
  ExternalGeometry = -> [Sketch045]
  FullyConstrained = true
  MakeInternals = false
  MapMode = 5
  Placement = pos=(0,0,0) rot=(1,0,0;1.5708rad)
  sketch-geometry (4):
    g0: LineSegment StartX=5.4 StartY=5.1 StartZ=0 EndX=5.4 EndY=3.9 EndZ=0
    g1: LineSegment StartX=5.4 StartY=3.9 StartZ=0 EndX=7 EndY=3.9 EndZ=0
    g2: LineSegment StartX=7 StartY=3.9 StartZ=0 EndX=7 EndY=5.1 EndZ=0
    g3: LineSegment StartX=7 StartY=5.1 StartZ=0 EndX=5.4 EndY=5.1 EndZ=0
  constraints (11):
    c: Coincident(g0,g1)
    c: Coincident(g1,g2)
    c: Coincident(g2,g3)
    c: Coincident(g3,g0)
    c: Vertical(g0)
    c: Vertical(g2)
    c: Horizontal(g1)
    c: Horizontal(g3)
    c: Distance(g0,g2) = 1.6
    c: Distance(g1,g3) = 1.2
    c: Coincident(g2,g-3)
FEATURE [Sketcher::SketchObject] Sketch064  label="rampini_per_serraggio_struttura"
  ArcFitTolerance = 1e-06
  AttachmentSupport = -> [XZ_Plane002]
  ExternalGeometry = -> [Sketch066,Sketch045]
  FullyConstrained = true
  MakeInternals = false
  MapMode = 5
  Placement = pos=(0,0,0) rot=(1,0,0;1.5708rad)
  sketch-geometry (7):
    g0: LineSegment StartX=7 StartY=5.1 StartZ=0 EndX=7 EndY=3.9 EndZ=0
    g1: LineSegment StartX=7 StartY=3.9 StartZ=0 EndX=9 EndY=3.9 EndZ=0
    g2: LineSegment StartX=7 StartY=5.1 StartZ=0 EndX=7 EndY=5.1 EndZ=0
    g3: LineSegment StartX=7 StartY=5.1 StartZ=0 EndX=7 EndY=7.5 EndZ=0
    g4: LineSegment StartX=9 StartY=5.1 StartZ=0 EndX=9 EndY=3.9 EndZ=0
    g5: LineSegment StartX=7 StartY=7.5 StartZ=0 EndX=9 EndY=7.5 EndZ=0
    g6: LineSegment StartX=9 StartY=7.5 StartZ=0 EndX=9 EndY=5.1 EndZ=0
  constraints (20):
    c: Vertical(g0)
    c: Coincident(g1,g0)
    c: Horizontal(g1)
    c: Coincident(g2,g0)
    c: Horizontal(g2)
    c: Coincident(g3,g2)
    c: Vertical(g3)
    c: Coincident(g5,g3)
    c: Coincident(g4,g6)
    c: Coincident(g4,g1)
    c: Vertical(g4)
    c: Coincident(g0,g-3)
    c: DistanceY(g-4,g3) = 2.4
    c: DistanceX(g1,g1) = 2
    c: DistanceY(g2,g6) = 0
    c: DistanceX(g2,g2) = 0
    c: DistanceY(g0,g0) = 1.2
    c: Coincident(g5,g6)
    c: Horizontal(g5)
    c: Vertical(g6)
FEATURE [Sketcher::SketchObject] Sketch067  label="perno per blocco switch"
  ArcFitTolerance = 1e-06
  AttachmentSupport = -> [XZ_Plane]
  ExternalGeometry = -> [Sketch,Sketch010]
  FullyConstrained = true
  MakeInternals = false
  MapMode = 5
  Placement = pos=(0,0,0) rot=(1,0,0;1.5708rad)
  sketch-geometry (14):
    g0: LineSegment StartX=-191.073 StartY=24.9429 StartZ=0 EndX=-185.81 EndY=23.0276 EndZ=0
    g1: LineSegment StartX=-183.76 StartY=23.9839 StartZ=0 EndX=-182.392 EndY=27.7427 EndZ=0
    g2: LineSegment StartX=-183.348 StartY=29.7934 StartZ=0 EndX=-188.61 EndY=31.7087 EndZ=0
    g3: LineSegment StartX=-188.61 StartY=31.7087 StartZ=0 EndX=-191.073 EndY=24.9429 EndZ=0
    g4: GeomPoint [constr] X=-186.459 Y=27.0946 Z=0
    g5: LineSegment StartX=-189.022 StartY=25.8992 StartZ=0 EndX=-185.263 EndY=24.5311 EndZ=0
    g6: LineSegment StartX=-185.263 StartY=24.5311 StartZ=0 EndX=-183.895 EndY=28.2899 EndZ=0
    g7: LineSegment StartX=-183.895 StartY=28.2899 StartZ=0 EndX=-187.654 EndY=29.658 EndZ=0
    g8: LineSegment StartX=-187.654 StartY=29.658 StartZ=0 EndX=-189.022 EndY=25.8992 EndZ=0
    g9: GeomPoint [constr] X=-186.459 Y=27.0946 Z=0
    g10: ArcOfCircle CenterX=-185.263 CenterY=24.5311 CenterZ=0 NormalX=0 NormalY=0 NormalZ=1 AngleXU=0 Radius=1.6 StartAngle=4.36332 EndAngle=5.93412
    g11: GeomPoint [constr] X=-184.307 Y=22.4804 Z=0
    g12: ArcOfCircle CenterX=-183.895 CenterY=28.2899 CenterZ=0 NormalX=0 NormalY=0 NormalZ=1 AngleXU=0 Radius=1.6 StartAngle=5.93412 EndAngle=7.50492
    g13: GeomPoint [constr] X=-181.844 Y=29.2462 Z=0
  constraints (30):
    c: Coincident(g2,g3)
    c: Coincident(g3,g0)
    c: Symmetric(g13,g0,g4)
    c: Distance(g11,g3) = 7.2
    c: Distance(g0,g2) = 7.2
    c: Parallel(g3,g1)
    c: Parallel(g2,g0)
    c: Perpendicular(g2,g3)
    c: Coincident(g5,g6)
    c: Coincident(g6,g7)
    c: Coincident(g7,g8)
    c: Coincident(g8,g5)
    c: Symmetric(g7,g5,g9)
    c: Distance(g6,g8) = 4
    c: Distance(g5,g7) = 4
    c: Coincident(g9,g4)
    c: Parallel(g8,g6)
    c: Parallel(g7,g5)
    c: Perpendicular(g7,g8)
    c: Tangent(g8,g-3)
    c: Tangent(g2,g-4)
    c: PointOnObject(g11,g1)
    c: PointOnObject(g11,g0)
    c: Tangent(g1,g10) = -1.5708
    c: Tangent(g0,g10) = -1.5708
    c: PointOnObject(g13,g1)
    c: Tangent(g1,g12) = -1.5708
    c: Tangent(g2,g12) = -1.5708
    c: Equal(g10,g12)
    c: Coincident(g10,g5)
FEATURE [Part::Extrusion] Extrude072  label="Extrude perno per blocco switch"
  Base = -> Sketch067
  Dir = (0,-1,2e-16)
  DirMode = 2
  FaceMakerClass = Part::FaceMakerBullseye
  FaceMakerMode = 3
  LengthFwd = 25.2
  LengthRev = 0
  Solid = true
  Symmetric = true
FEATURE [Part::MultiFuse] Fusion
  Refine = true
  Shapes = -> [Extrude,Sweep,Extrude007,Extrude011,Extrude005,Extrude012,Extrude013,Extrude016,Extrude031,Extrude039,Extrude045,Extrude072]
FEATURE [Part::Cut] Cut
  Base = -> Fusion
  Refine = true
  Tool = -> Extrude001
FEATURE [Part::Cut] Cut001
  Base = -> Cut
  Refine = true
  Tool = -> Extrude004
FEATURE [Part::Cut] Cut002
  Base = -> Cut001
  Refine = true
  Tool = -> Extrude006
FEATURE [Part::Cut] Cut003
  Base = -> Cut002
  Refine = true
  Tool = -> Extrude008
FEATURE [Part::Cut] Cut004
  Base = -> Cut003
  Refine = true
  Tool = -> Extrude009
FEATURE [Part::Cut] Cut005
  Base = -> Cut004
  Refine = true
  Tool = -> Extrude010
FEATURE [Part::Cut] Cut006
  Base = -> Cut005
  Refine = true
  Tool = -> Extrude014
FEATURE [Part::Cut] Cut007
  Base = -> Cut006
  Refine = true
  Tool = -> Extrude015
FEATURE [Part::Cut] Cut008
  Base = -> Cut007
  Refine = true
  Tool = -> Extrude018
FEATURE [Part::Cut] Cut009
  Base = -> Cut008
  Refine = true
  Tool = -> Extrude019
FEATURE [Part::Cut] Cut010
  Base = -> Cut009
  Refine = true
  Tool = -> Extrude020
FEATURE [Part::Cut] Cut011
  Base = -> Cut010
  Refine = true
  Tool = -> Extrude021
FEATURE [Part::Cut] Cut012
  Base = -> Cut011
  Refine = true
  Tool = -> Extrude022
FEATURE [Part::Cut] Cut013
  Base = -> Cut012
  Refine = true
  Tool = -> Extrude023
FEATURE [Part::Cut] Cut014
  Base = -> Cut013
  Refine = true
  Tool = -> Extrude032
FEATURE [Part::Cut] Cut015
  Base = -> Cut014
  Refine = true
  Tool = -> Extrude033
FEATURE [Part::Cut] Cut016
  Base = -> Cut015
  Refine = true
  Tool = -> Extrude034
FEATURE [Part::Cut] Cut017
  Base = -> Cut016
  Refine = true
  Tool = -> Extrude035
FEATURE [Part::Cut] Cut018
  Base = -> Cut017
  Refine = true
  Tool = -> Extrude036
FEATURE [Part::Cut] Cut019
  Base = -> Cut018
  Refine = true
  Tool = -> Extrude037
FEATURE [Part::Cut] Cut020
  Base = -> Cut019
  Refine = true
  Tool = -> Extrude030
FEATURE [Part::Cut] Cut022
  Base = -> Cut020
  Refine = true
  Tool = -> Extrude038
FEATURE [Part::Cut] Cut023
  Base = -> Cut022
  Refine = true
  Tool = -> Extrude041
FEATURE [Part::Cut] Cut024
  Base = -> Cut023
  Refine = true
  Tool = -> Extrude040
FEATURE [Part::Cut] Cut025
  Base = -> Cut024
  Refine = true
  Tool = -> Extrude042
FEATURE [Part::Cut] Cut026
  Base = -> Cut025
  Refine = true
  Tool = -> Extrude043
FEATURE [Part::Cut] Cut027
  Base = -> Cut026
  Refine = true
  Tool = -> Extrude044
FEATURE [Part::Cut] Cut028
  Base = -> Cut027
  Refine = true
  Tool = -> Extrude046
FEATURE [Part::Cut] Cut029
  Base = -> Cut028
  Refine = true
  Tool = -> Extrude047
FEATURE [Part::Cut] Cut033
  Base = -> Cut029
  Refine = true
  Tool = -> Extrude055
FEATURE [Part::Cut] Cut034
  Base = -> Cut033
  Refine = true
  Tool = -> Extrude056
FEATURE [Part::Cut] Cut035
  Base = -> Cut034
  Refine = true
  Tool = -> Extrude057
FEATURE [Part::Cut] Cut037
  Base = -> Cut035
  Refine = true
  Tool = -> Extrude060
FEATURE [Part::Cut] Cut038
  Base = -> Cut037
  Refine = true
  Tool = -> Extrude061
FEATURE [Part::Cut] Cut039
  Base = -> Cut038
  Refine = true
  Tool = -> Extrude063
FEATURE [Part::Cut] Cut040
  Base = -> Cut039
  Refine = true
  Tool = -> Extrude064
FEATURE [Part::Cut] Cut041
  Base = -> Cut040
  Refine = true
  Tool = -> Extrude062
FEATURE [Sketcher::SketchObject] Sketch068  label="base con smusso sopra neopixel"
  ArcFitTolerance = 1e-06
  AttachmentSupport = -> [YZ_Plane002]
  FullyConstrained = true
  MakeInternals = false
  MapMode = 5
  Placement = pos=(0,0,0) rot=(0.57735,0.57735,0.57735;2.0944rad)
  sketch-geometry (5):
    g0: LineSegment StartX=-9.5 StartY=-6.1 StartZ=0 EndX=9.5 EndY=-6.1 EndZ=0
    g1: LineSegment StartX=9.5 StartY=-6.1 StartZ=0 EndX=9.5 EndY=6.1 EndZ=0
    g2: LineSegment StartX=9.5 StartY=6.1 StartZ=0 EndX=-9.5 EndY=6.1 EndZ=0
    g3: LineSegment StartX=-9.5 StartY=6.1 StartZ=0 EndX=-9.5 EndY=-6.1 EndZ=0
    g4: GeomPoint [constr] X=0 Y=0 Z=0
  constraints (12):
    c: Coincident(g0,g1)
    c: Coincident(g1,g2)
    c: Coincident(g2,g3)
    c: Coincident(g3,g0)
    c: Horizontal(g0)
    c: Horizontal(g2)
    c: Vertical(g1)
    c: Vertical(g3)
    c: Symmetric(g2,g0,g4)
    c: Distance(g1,g3) = 19
    c: Distance(g0,g2) = 12.2
    c: Coincident(g4,g-1)
FEATURE [Sketcher::SketchObject] Sketch069  label="cilindro minore"
  ArcFitTolerance = 1e-06
  AttachmentSupport = -> [XZ_Plane004]
  FullyConstrained = true
  MakeInternals = false
  MapMode = 5
  Placement = pos=(0,0,0) rot=(1,0,0;1.5708rad)
  sketch-geometry (1):
    g0: Circle CenterX=0 CenterY=0 CenterZ=0 NormalX=0 NormalY=0 NormalZ=1 AngleXU=0 Radius=5.8
  constraints (2):
    c: Diameter(g0) = 11.6
    c: Coincident(g0,g-1)
FEATURE [Sketcher::SketchObject] Sketch070  label="cilindro maggiore"
  ArcFitTolerance = 1e-06
  AttachmentSupport = -> [XZ_Plane004]
  ExternalGeometry = -> [Sketch069]
  FullyConstrained = true
  MakeInternals = false
  MapMode = 5
  Placement = pos=(0,0,0) rot=(1,0,0;1.5708rad)
  sketch-geometry (1):
    g0: Circle CenterX=0 CenterY=0 CenterZ=0 NormalX=0 NormalY=0 NormalZ=1 AngleXU=0 Radius=6.5
  constraints (2):
    c: Coincident(g0,g-1)
    c: Diameter(g0) = 13
FEATURE [Sketcher::SketchObject] Sketch071  label="buco interno"
  ArcFitTolerance = 1e-06
  AttachmentSupport = -> [XZ_Plane004]
  ExternalGeometry = -> [Sketch069]
  FullyConstrained = true
  MakeInternals = false
  MapMode = 5
  Placement = pos=(0,0,0) rot=(1,0,0;1.5708rad)
  sketch-geometry (1):
    g0: Circle CenterX=0 CenterY=0 CenterZ=0 NormalX=0 NormalY=0 NormalZ=1 AngleXU=0 Radius=5
  constraints (2):
    c: Coincident(g0,g-1)
    c: Diameter(g0) = 10
FEATURE [PartDesign::Pad] Pad
  Direction = (0,-1,2e-16)
  Length = 1.2
  Length2 = 10
  Placement = pos=(0,0,0) rot=(1,0,0;1.5708rad)
  Profile = -> Sketch070
  ReferenceAxis = -> Sketch070 [N_Axis]
  Refine = true
  Suppressed = false
  Type = 0
FEATURE [PartDesign::Pad] Pad001
  BaseFeature = -> Pad
  Direction = (0,-1,2e-16)
  Length = 5.6
  Length2 = 10
  Placement = pos=(0,0,0) rot=(1,0,0;1.5708rad)
  Profile = -> Sketch069
  ReferenceAxis = -> Sketch069 [N_Axis]
  Refine = true
  Suppressed = false
  Type = 0
FEATURE [PartDesign::Pocket] Pocket
  BaseFeature = -> Pad001
  Direction = (0,1,-2e-16)
  Length = 7
  Length2 = 5
  Midplane = true
  Placement = pos=(0,0,0) rot=(1,0,0;1.5708rad)
  Profile = -> Sketch071
  ReferenceAxis = -> Sketch071 [N_Axis]
  Refine = true
  Suppressed = false
  Type = 0
FEATURE [PartDesign::Fillet] Fillet
  Base = -> Pocket [Face7]
  BaseFeature = -> Pocket
  Placement = pos=(0,0,0) rot=(1,0,0;1.5708rad)
  Radius = 1
  Refine = true
  SupportTransform = false
  Suppressed = false
  UseAllEdges = false
FEATURE [PartDesign::Body] Body004  label="pulsanti lato sinistro"
  AllowCompound = false
  Group = -> [Sketch069,Sketch070,Sketch071,Pad,Pad001,Pocket,Fillet]
  Origin = -> Origin004
  Tip = -> Fillet
FEATURE [Sketcher::SketchObject] Sketch072  label="buco per saldature e diodo driver solenoide"
  ArcFitTolerance = 1e-06
  AttachmentSupport = -> [XZ_Plane]
  ExternalGeometry = -> [Sketch038]
  FullyConstrained = true
  MakeInternals = false
  MapMode = 5
  Placement = pos=(0,0,0) rot=(1,0,0;1.5708rad)
  sketch-geometry (4):
    g0: LineSegment StartX=-209.225 StartY=-40.6939 StartZ=0 EndX=-204.154 EndY=-29.8182 EndZ=0
    g1: LineSegment StartX=-204.154 StartY=-29.8182 StartZ=0 EndX=-206.51 EndY=-28.7194 EndZ=0
    g2: LineSegment StartX=-206.51 StartY=-28.7194 StartZ=0 EndX=-211.582 EndY=-39.5951 EndZ=0
    g3: LineSegment StartX=-211.582 StartY=-39.5951 StartZ=0 EndX=-209.225 EndY=-40.6939 EndZ=0
  constraints (11):
    c: Coincident(g1,g0)
    c: Coincident(g2,g1)
    c: Coincident(g3,g2)
    c: Coincident(g3,g0)
    c: Parallel(g-3,g0)
    c: Parallel(g0,g2)
    c: Perpendicular(g0,g3)
    c: Perpendicular(g1,g0)
    c: Distance(g3) = 2.6
    c: Distance(g2) = 12
    c: Coincident(g0,g-3)
FEATURE [Part::Extrusion] Extrude074  label="Extrude buco per saldature e diodo driver solenoide"
  Base = -> Sketch072
  Dir = (0,-1,2e-16)
  DirMode = 2
  FaceMakerClass = Part::FaceMakerBullseye
  FaceMakerMode = 3
  LengthFwd = 14.6
  LengthRev = 0
  Solid = true
  Symmetric = true
FEATURE [Part::Cut] Cut042
  Base = -> Cut041
  Refine = true
  Tool = -> Extrude074
FEATURE [Sketcher::SketchObject] Sketch073  label="fori slargati blocco solenoide"
  ArcFitTolerance = 1e-06
  AttachmentSupport = -> [XY_Plane]
  ExternalGeometry = -> [Sketch030]
  FullyConstrained = true
  MakeInternals = false
  MapMode = 5
  sketch-geometry (2):
    g0: Circle CenterX=-152.209 CenterY=6.95 CenterZ=0 NormalX=0 NormalY=0 NormalZ=1 AngleXU=0 Radius=3.7
    g1: Circle CenterX=-130.41 CenterY=-6.95 CenterZ=0 NormalX=0 NormalY=0 NormalZ=1 AngleXU=0 Radius=3.7
  constraints (4):
    c: Diameter(g0) = 7.4
    c: Coincident(g0,g-3)
    c: Diameter(g1) = 7.4
    c: Coincident(g1,g-4)
FEATURE [Part::Extrusion] Extrude075  label="Extrude fori slargati blocco solenoide"
  Base = -> Sketch073
  Dir = (0,0,1)
  DirMode = 2
  FaceMakerClass = Part::FaceMakerBullseye
  FaceMakerMode = 3
  LengthFwd = 1.5
  LengthRev = 0
  Placement = pos=(0,0,36.4) rot=(0,0,1;0rad)
  Solid = true
  Symmetric = false
FEATURE [Part::Cut] Cut043
  Base = -> Cut042
  Refine = true
  Tool = -> Extrude075
FEATURE [Sketcher::SketchObject] Sketch074  label="lato sx pistola"
  ArcFitTolerance = 1e-06
  AttachmentSupport = -> [XZ_Plane]
  ExternalGeometry = -> [Sketch016,Sketch,Sketch058]
  FullyConstrained = true
  MakeInternals = false
  MapMode = 5
  Placement = pos=(0,0,0) rot=(1,0,0;1.5708rad)
  sketch-geometry (37):
    g0: LineSegment StartX=-82.8 StartY=3.2 StartZ=0 EndX=0 EndY=3.2 EndZ=0
    g1: LineSegment StartX=-82.8 StartY=3.2 StartZ=0 EndX=-82.8 EndY=6.2 EndZ=0
    g2: LineSegment [constr] StartX=-107.6 StartY=18 StartZ=0 EndX=-107.6 EndY=20 EndZ=0
    g3: LineSegment [constr] StartX=-132.428 StartY=18 StartZ=0 EndX=-132.428 EndY=20 EndZ=0
    g4: LineSegment StartX=-132.428 StartY=20 StartZ=0 EndX=-107.6 EndY=20 EndZ=0
    g5: ArcOfCircle CenterX=-107.6 CenterY=4 CenterZ=0 NormalX=0 NormalY=0 NormalZ=1 AngleXU=0 Radius=16 StartAngle=0.137937 EndAngle=1.5708
    g6: LineSegment StartX=-82.8 StartY=6.2 StartZ=0 EndX=-91.752 EndY=6.2 EndZ=0
    g7: LineSegment [constr] StartX=-145.743 StartY=8.32624 StartZ=0 EndX=-147.645 EndY=8.94427 EndZ=0
    g8: ArcOfCircle CenterX=-132.428 CenterY=4 CenterZ=0 NormalX=0 NormalY=0 NormalZ=1 AngleXU=0 Radius=16 StartAngle=1.5708 EndAngle=2.82743
    g9: LineSegment StartX=-215.932 StartY=-80.4316 StartZ=0 EndX=-176.685 EndY=-80.4316 EndZ=0
    g10: LineSegment StartX=-147.645 StartY=8.94427 StartZ=0 EndX=-176.685 EndY=-80.4316 EndZ=0
    g11: LineSegment [constr] StartX=-193.988 StartY=-2.33927 StartZ=0 EndX=-192.176 EndY=-3.18451 EndZ=0
    g12: LineSegment [constr] StartX=-217.232 StartY=-52.1862 StartZ=0 EndX=-215.42 EndY=-53.0314 EndZ=0
    g13: LineSegment StartX=-192.176 StartY=-3.18451 StartZ=0 EndX=-215.42 EndY=-53.0314 EndZ=0
    g14: ArcOfCircle CenterX=-184.801 CenterY=-67.3089 CenterZ=0 NormalX=0 NormalY=0 NormalZ=1 AngleXU=0 Radius=33.7833 StartAngle=2.70526 EndAngle=3.54053
    g15: ArcOfCircle CenterX=-207.583 CenterY=4 CenterZ=0 NormalX=0 NormalY=0 NormalZ=1 AngleXU=0 Radius=17 StartAngle=5.84685 EndAngle=7.56663
    g16: LineSegment StartX=-202.765 StartY=20.303 StartZ=0 EndX=-195.887 EndY=39.2 EndZ=0
    g17: LineSegment [constr] StartX=-193.885 StartY=33.0037 StartZ=0 EndX=-197.644 EndY=34.3718 EndZ=0
    g18: LineSegment StartX=-195.887 StartY=39.2 StartZ=0 EndX=0 EndY=39.2 EndZ=0
    g19: LineSegment StartX=0 StartY=3.2 StartZ=0 EndX=0 EndY=39.2 EndZ=0
    g20: LineSegment StartX=-189.939 StartY=31.5672 StartZ=0 EndX=-192.333 EndY=24.9893 EndZ=0
    g21: LineSegment StartX=-196.467 StartY=26.4942 StartZ=0 EndX=-194.073 EndY=33.0721 EndZ=0
    g22: Circle CenterX=-213.443 CenterY=-76.8316 CenterZ=0 NormalX=0 NormalY=0 NormalZ=1 AngleXU=0 Radius=1.8
    g23: Circle CenterX=-179.305 CenterY=-76.8316 CenterZ=0 NormalX=0 NormalY=0 NormalZ=1 AngleXU=0 Radius=1.8
    g24: Circle CenterX=-184.08 CenterY=34.8 CenterZ=0 NormalX=0 NormalY=0 NormalZ=1 AngleXU=0 Radius=1.8
    g25: Circle CenterX=-78.51 CenterY=34.8 CenterZ=0 NormalX=0 NormalY=0 NormalZ=1 AngleXU=0 Radius=1.8
    g26: Circle CenterX=-78.51 CenterY=7.6 CenterZ=0 NormalX=0 NormalY=0 NormalZ=1 AngleXU=0 Radius=1.8
    g27: Circle CenterX=-5.6 CenterY=34.8 CenterZ=0 NormalX=0 NormalY=0 NormalZ=1 AngleXU=0 Radius=1.8
    g28: Circle CenterX=-5.6 CenterY=7.6 CenterZ=0 NormalX=0 NormalY=0 NormalZ=1 AngleXU=0 Radius=1.8
    g29: LineSegment StartX=-190.127 StartY=31.6356 StartZ=0 EndX=-189.939 EndY=31.5672 EndZ=0
    g30: LineSegment StartX=-194.073 StartY=33.0721 StartZ=0 EndX=-193.885 EndY=33.0037 EndZ=0
    g31: LineSegment StartX=-193.885 StartY=33.0037 StartZ=0 EndX=-190.127 EndY=31.6356 EndZ=0
    g32: LineSegment StartX=-196.467 StartY=26.4942 StartZ=0 EndX=-192.333 EndY=24.9893 EndZ=0
    g33: Circle CenterX=-19 CenterY=21.2 CenterZ=0 NormalX=0 NormalY=0 NormalZ=1 AngleXU=0 Radius=6.3
    g34: Circle CenterX=-42 CenterY=21.2 CenterZ=0 NormalX=0 NormalY=0 NormalZ=1 AngleXU=0 Radius=6.3
    g35: Circle CenterX=-65 CenterY=21.2 CenterZ=0 NormalX=0 NormalY=0 NormalZ=1 AngleXU=0 Radius=6.3
    g36: LineSegment [constr] StartX=-4 StartY=21.2 StartZ=0 EndX=-65 EndY=21.2 EndZ=0
  constraints (96):
    c: Coincident(g0,g-41)
    c: Horizontal(g0)
    c: PointOnObject(g0,g-39)
    c: Coincident(g1,g0)
    c: Vertical(g1)
    c: DistanceY(g1,g1) = 3
    c: Coincident(g2,g-17)
    c: Vertical(g2)
    c: Coincident(g3,g-16)
    c: Vertical(g3)
    c: DistanceY(g2,g2) = 2
    c: DistanceY(g3,g3) = 2
    c: Coincident(g4,g3)
    c: Coincident(g4,g2)
    c: Coincident(g5,g-17)
    c: Coincident(g5,g2)
    c: Coincident(g6,g1)
    c: Horizontal(g6)
    c: Coincident(g6,g5)
    c: Coincident(g7,g-15)
    c: Coincident(g8,g7)
    c: Coincident(g8,g3)
    c: Coincident(g8,g-15)
    c: Horizontal(g9)
    c: DistanceY(g-13,g9) = 2
    c: Coincident(g10,g7)
    c: Parallel(g10,g-14)
    c: Coincident(g9,g10)
    c: Distance(g11) = 2
    c: Coincident(g11,g-11)
    c: Perpendicular(g-11,g11)
    c: Distance(g12) = 2
    c: Coincident(g12,g-12)
    c: Perpendicular(g-11,g12)
    c: Coincident(g13,g11)
    c: Coincident(g13,g12)
    c: Coincident(g14,g-32)
    c: Coincident(g14,g12)
    c: Coincident(g14,g9)
    c: Coincident(g15,g-10)
    c: Coincident(g15,g11)
    c: Parallel(g16,g-22)
    c: Distance(g17) = 4
    c: PointOnObject(g17,g16)
    c: Coincident(g15,g16)
    c: Horizontal(g18)
    c: Coincident(g18,g16)
    c: Coincident(g19,g0)
    c: PointOnObject(g19,g-39)
    c: DistanceY(g19,g-36) = 2
    c: Coincident(g18,g19)
    c: Diameter(g22) = 3.6
    c: Coincident(g22,g-9)
    c: Diameter(g23) = 3.6
    c: Coincident(g23,g-8)
    c: Diameter(g24) = 3.6
    c: Diameter(g25) = 3.6
    c: Diameter(g26) = 3.6
    c: Diameter(g27) = 3.6
    c: Diameter(g28) = 3.6
    c: Coincident(g27,g-4)
    c: Coincident(g28,g-3)
    c: Coincident(g25,g-6)
    c: Coincident(g26,g-5)
    c: Coincident(g24,g-7)
    c: Parallel(g20,g-21)
    c: Equal(g20,g-21)
    c: Parallel(g21,g-19)
    c: Equal(g21,g-19)
    c: Distance(g29) = 0.2
    c: Distance(g30) = 0.2
    c: Parallel(g29,g-20)
    c: Parallel(g31,g-20)
    c: Equal(g31,g-20)
    c: Coincident(g30,g31)
    c: Coincident(g31,g29)
    c: Coincident(g29,g-21)
    c: Parallel(g30,g31)
    c: Coincident(g17,g30)
    c: Coincident(g20,g29)
    c: Coincident(g21,g30)
    c: Perpendicular(g16,g17)
    c: Coincident(g32,g21)
    c: Coincident(g32,g20)
    c: Perpendicular(g10,g7)
    c: Diameter(g33) = 12.6
    c: Diameter(g34) = 12.6
    c: Diameter(g35) = 12.6
    c: Horizontal(g36)
    c: PointOnObject(g33,g36)
    c: PointOnObject(g34,g36)
    c: DistanceX(g34,g33) = 23
    c: DistanceX(g35,g34) = 23
    c: DistanceX(g33,g36) = 15
    c: Symmetric(g-24,g-24,g36)
    c: Coincident(g36,g35)
FEATURE [Sketcher::SketchObject] Sketch075  label="lato dx pistola"
  ArcFitTolerance = 1e-06
  AttachmentSupport = -> [XZ_Plane]
  ExternalGeometry = -> [Sketch016,Sketch,Sketch058,Sketch074]
  FullyConstrained = true
  MakeInternals = false
  MapMode = 5
  Placement = pos=(0,0,0) rot=(1,0,0;1.5708rad)
  sketch-geometry (61):
    g0: LineSegment StartX=-82.8 StartY=3.2 StartZ=0 EndX=0 EndY=3.2 EndZ=0
    g1: LineSegment StartX=-82.8 StartY=3.2 StartZ=0 EndX=-82.8 EndY=6.2 EndZ=0
    g2: LineSegment [constr] StartX=-107.6 StartY=18 StartZ=0 EndX=-107.6 EndY=20 EndZ=0
    g3: LineSegment [constr] StartX=-132.428 StartY=18 StartZ=0 EndX=-132.428 EndY=20 EndZ=0
    g4: LineSegment StartX=-132.428 StartY=20 StartZ=0 EndX=-107.6 EndY=20 EndZ=0
    g5: ArcOfCircle CenterX=-107.6 CenterY=4 CenterZ=0 NormalX=0 NormalY=0 NormalZ=1 AngleXU=0 Radius=16 StartAngle=0.137937 EndAngle=1.5708
    g6: LineSegment StartX=-82.8 StartY=6.2 StartZ=0 EndX=-91.752 EndY=6.2 EndZ=0
    g7: LineSegment [constr] StartX=-145.743 StartY=8.32624 StartZ=0 EndX=-147.645 EndY=8.94427 EndZ=0
    g8: ArcOfCircle CenterX=-132.428 CenterY=4 CenterZ=0 NormalX=0 NormalY=0 NormalZ=1 AngleXU=0 Radius=16 StartAngle=1.5708 EndAngle=2.82743
    g9: LineSegment StartX=-215.932 StartY=-80.4316 StartZ=0 EndX=-176.685 EndY=-80.4316 EndZ=0
    g10: LineSegment StartX=-147.645 StartY=8.94427 StartZ=0 EndX=-176.685 EndY=-80.4316 EndZ=0
    g11: LineSegment [constr] StartX=-193.988 StartY=-2.33927 StartZ=0 EndX=-192.176 EndY=-3.18451 EndZ=0
    g12: LineSegment [constr] StartX=-217.232 StartY=-52.1862 StartZ=0 EndX=-215.42 EndY=-53.0314 EndZ=0
    g13: LineSegment StartX=-192.176 StartY=-3.18451 StartZ=0 EndX=-215.42 EndY=-53.0314 EndZ=0
    g14: ArcOfCircle CenterX=-184.801 CenterY=-67.3089 CenterZ=0 NormalX=0 NormalY=0 NormalZ=1 AngleXU=0 Radius=33.7833 StartAngle=2.70526 EndAngle=3.54053
    g15: ArcOfCircle CenterX=-207.583 CenterY=4 CenterZ=0 NormalX=0 NormalY=0 NormalZ=1 AngleXU=0 Radius=17 StartAngle=5.84685 EndAngle=7.56663
    g16: LineSegment StartX=-202.765 StartY=20.303 StartZ=0 EndX=-195.887 EndY=39.2 EndZ=0
    g17: LineSegment [constr] StartX=-193.885 StartY=33.0037 StartZ=0 EndX=-197.644 EndY=34.3718 EndZ=0
    g18: LineSegment StartX=-195.887 StartY=39.2 StartZ=0 EndX=0 EndY=39.2 EndZ=0
    g19: LineSegment StartX=0 StartY=3.2 StartZ=0 EndX=0 EndY=39.2 EndZ=0
    g20: LineSegment StartX=-189.939 StartY=31.5672 StartZ=0 EndX=-192.333 EndY=24.9893 EndZ=0
    g21: LineSegment StartX=-196.467 StartY=26.4942 StartZ=0 EndX=-194.073 EndY=33.0721 EndZ=0
    g22: Circle CenterX=-213.443 CenterY=-76.8316 CenterZ=0 NormalX=0 NormalY=0 NormalZ=1 AngleXU=0 Radius=1.8
    g23: Circle CenterX=-179.305 CenterY=-76.8316 CenterZ=0 NormalX=0 NormalY=0 NormalZ=1 AngleXU=0 Radius=1.8
    g24: Circle CenterX=-184.08 CenterY=34.8 CenterZ=0 NormalX=0 NormalY=0 NormalZ=1 AngleXU=0 Radius=1.8
    g25: Circle CenterX=-78.51 CenterY=34.8 CenterZ=0 NormalX=0 NormalY=0 NormalZ=1 AngleXU=0 Radius=1.8
    g26: Circle CenterX=-78.51 CenterY=7.6 CenterZ=0 NormalX=0 NormalY=0 NormalZ=1 AngleXU=0 Radius=1.8
    g27: Circle CenterX=-5.6 CenterY=34.8 CenterZ=0 NormalX=0 NormalY=0 NormalZ=1 AngleXU=0 Radius=1.8
    g28: Circle CenterX=-5.6 CenterY=7.6 CenterZ=0 NormalX=0 NormalY=0 NormalZ=1 AngleXU=0 Radius=1.8
    g29: LineSegment StartX=-190.127 StartY=31.6356 StartZ=0 EndX=-189.939 EndY=31.5672 EndZ=0
    g30: LineSegment StartX=-194.073 StartY=33.0721 StartZ=0 EndX=-193.885 EndY=33.0037 EndZ=0
    g31: LineSegment StartX=-193.885 StartY=33.0037 StartZ=0 EndX=-190.127 EndY=31.6356 EndZ=0
    g32: LineSegment StartX=-196.467 StartY=26.4942 StartZ=0 EndX=-192.333 EndY=24.9893 EndZ=0
    g33: LineSegment [constr] StartX=-4 StartY=21.2 StartZ=0 EndX=-87.91 EndY=21.2 EndZ=0
    g34: GeomPoint [constr] X=-4 Y=21.2 Z=0
    g35: LineSegment [constr] StartX=-15.2 StartY=33.7 StartZ=0 EndX=-15.2 EndY=8.7 EndZ=0
    g36: LineSegment [constr] StartX=-15.2 StartY=33.7 StartZ=0 EndX=-56.2 EndY=33.7 EndZ=0
    g37: LineSegment [constr] StartX=-15.2 StartY=8.7 StartZ=0 EndX=-56.2 EndY=8.7 EndZ=0
    g38: LineSegment [constr] StartX=-56.2 StartY=33.7 StartZ=0 EndX=-56.2 EndY=8.7 EndZ=0
    g39: Circle CenterX=-18.6 CenterY=30.3 CenterZ=0 NormalX=0 NormalY=0 NormalZ=1 AngleXU=0 Radius=3.4
    g40: Circle CenterX=-18.6 CenterY=12.1 CenterZ=0 NormalX=0 NormalY=0 NormalZ=1 AngleXU=0 Radius=3.4
    g41: Circle CenterX=-43.2 CenterY=30.3 CenterZ=0 NormalX=0 NormalY=0 NormalZ=1 AngleXU=0 Radius=3.4
    g42: Circle CenterX=-43.2 CenterY=12.1 CenterZ=0 NormalX=0 NormalY=0 NormalZ=1 AngleXU=0 Radius=3.4
    g43: LineSegment [constr] StartX=-4 StartY=21.2 StartZ=0 EndX=-15.2 EndY=21.2 EndZ=0
    g44: LineSegment [constr] StartX=-15.2 StartY=21.2 StartZ=0 EndX=-36.2 EndY=21.2 EndZ=0
    g45: LineSegment [constr] StartX=-41.5 StartY=16.2 StartZ=0 EndX=-30.9 EndY=16.2 EndZ=0
    g46: LineSegment [constr] StartX=-30.9 StartY=16.2 StartZ=0 EndX=-30.9 EndY=26.2 EndZ=0
    g47: LineSegment [constr] StartX=-30.9 StartY=26.2 StartZ=0 EndX=-41.5 EndY=26.2 EndZ=0
    g48: LineSegment [constr] StartX=-41.5 StartY=26.2 StartZ=0 EndX=-41.5 EndY=16.2 EndZ=0
    g49: GeomPoint [constr] X=-36.2 Y=21.2 Z=0
    g50: Circle CenterX=-36.2 CenterY=21.2 CenterZ=0 NormalX=0 NormalY=0 NormalZ=1 AngleXU=0 Radius=2.8
    g51: LineSegment [constr] StartX=-24.2 StartY=26.7 StartZ=0 EndX=-24.2 EndY=15.7 EndZ=0
    g52: Circle CenterX=-24.2 CenterY=26.7 CenterZ=0 NormalX=0 NormalY=0 NormalZ=1 AngleXU=0 Radius=3
    g53: Circle CenterX=-24.2 CenterY=15.7 CenterZ=0 NormalX=0 NormalY=0 NormalZ=1 AngleXU=0 Radius=3
    g54: GeomPoint X=-18.6 Y=30.3 Z=0
    g55: GeomPoint X=-18.6 Y=12.1 Z=0
    g56: GeomPoint X=-43.2 Y=12.1 Z=0
    g57: GeomPoint X=-43.2 Y=30.3 Z=0
    g58: Circle CenterX=-65 CenterY=21.2 CenterZ=0 NormalX=0 NormalY=0 NormalZ=1 AngleXU=0 Radius=1.5
    g59: Circle CenterX=-42 CenterY=21.2 CenterZ=0 NormalX=0 NormalY=0 NormalZ=1 AngleXU=0 Radius=1.5
    g60: Circle CenterX=-19 CenterY=21.2 CenterZ=0 NormalX=0 NormalY=0 NormalZ=1 AngleXU=0 Radius=1.5
  constraints (149):
    c: Coincident(g0,g-41)
    c: Horizontal(g0)
    c: PointOnObject(g0,g-39)
    c: Coincident(g1,g0)
    c: Vertical(g1)
    c: DistanceY(g1,g1) = 3
    c: Coincident(g2,g-17)
    c: Vertical(g2)
    c: Coincident(g3,g-16)
    c: Vertical(g3)
    c: DistanceY(g2,g2) = 2
    c: DistanceY(g3,g3) = 2
    c: Coincident(g4,g3)
    c: Coincident(g4,g2)
    c: Coincident(g5,g-17)
    c: Coincident(g5,g2)
    c: Coincident(g6,g1)
    c: Horizontal(g6)
    c: Coincident(g6,g5)
    c: Coincident(g7,g-15)
    c: Coincident(g8,g7)
    c: Coincident(g8,g3)
    c: Coincident(g8,g-15)
    c: Horizontal(g9)
    c: DistanceY(g-13,g9) = 2
    c: Coincident(g10,g7)
    c: Parallel(g10,g-14)
    c: Coincident(g9,g10)
    c: Distance(g11) = 2
    c: Coincident(g11,g-11)
    c: Perpendicular(g-11,g11)
    c: Distance(g12) = 2
    c: Coincident(g12,g-12)
    c: Perpendicular(g-11,g12)
    c: Coincident(g13,g11)
    c: Coincident(g13,g12)
    c: Coincident(g14,g-32)
    c: Coincident(g14,g12)
    c: Coincident(g14,g9)
    c: Coincident(g15,g-10)
    c: Coincident(g15,g11)
    c: Parallel(g16,g-22)
    c: Distance(g17) = 4
    c: PointOnObject(g17,g16)
    c: Coincident(g15,g16)
    c: Horizontal(g18)
    c: Coincident(g18,g16)
    c: Coincident(g19,g0)
    c: PointOnObject(g19,g-39)
    c: DistanceY(g19,g-36) = 2
    c: Coincident(g18,g19)
    c: Diameter(g22) = 3.6
    c: Coincident(g22,g-9)
    c: Diameter(g23) = 3.6
    c: Coincident(g23,g-8)
    c: Diameter(g24) = 3.6
    c: Diameter(g25) = 3.6
    c: Diameter(g26) = 3.6
    c: Diameter(g27) = 3.6
    c: Diameter(g28) = 3.6
    c: Coincident(g27,g-4)
    c: Coincident(g28,g-3)
    c: Coincident(g25,g-6)
    c: Coincident(g26,g-5)
    c: Coincident(g24,g-7)
    c: Parallel(g20,g-21)
    c: Equal(g20,g-21)
    c: Parallel(g21,g-19)
    c: Equal(g21,g-19)
    c: Distance(g29) = 0.2
    c: Distance(g30) = 0.2
    c: Parallel(g29,g-20)
    c: Parallel(g31,g-20)
    c: Equal(g31,g-20)
    c: Coincident(g30,g31)
    c: Coincident(g31,g29)
    c: Coincident(g29,g-21)
    c: Parallel(g30,g31)
    c: Coincident(g17,g30)
    c: Coincident(g20,g29)
    c: Coincident(g21,g30)
    c: Perpendicular(g16,g17)
    c: Coincident(g32,g21)
    c: Coincident(g32,g20)
    c: Perpendicular(g10,g7)
    c: Horizontal(g33)
    c: Symmetric(g-24,g-24,g33)
    c: PointOnObject(g33,g-28)
    c: Symmetric(g-24,g-24,g34)
    c: DistanceY(g35,g35) = 25
    c: Symmetric(g35,g35,g33)
    c: Distance(g36) = 41
    c: Coincident(g36,g35)
    c: Horizontal(g36)
    c: Coincident(g37,g35)
    c: Horizontal(g37)
    c: Coincident(g38,g36)
    c: Vertical(g38)
    c: Coincident(g37,g38)
    c: Diameter(g39) = 6.8
    c: Diameter(g40) = 6.8
    c: Tangent(g39,g36)
    c: Tangent(g40,g37)
    c: Tangent(g39,g35)
    c: Tangent(g40,g35)
    c: Diameter(g41) = 6.8
    c: Diameter(g42) = 6.8
    c: Tangent(g41,g36)
    c: Tangent(g42,g37)
    c: DistanceX(g41,g39) = 24.6
    c: DistanceX(g42,g40) = 24.6
    c: Distance(g43) = 11.2
    c: Coincident(g43,g33)
    c: PointOnObject(g43,g33)
    c: PointOnObject(g43,g35)
    c: Distance(g44) = 21
    c: Coincident(g44,g43)
    c: PointOnObject(g44,g33)
    c: Coincident(g45,g46)
    c: Coincident(g46,g47)
    c: Coincident(g47,g48)
    c: Coincident(g48,g45)
    c: Horizontal(g45)
    c: Horizontal(g47)
    c: Vertical(g46)
    c: Vertical(g48)
    c: Symmetric(g47,g45,g49)
    c: Distance(g46,g48) = 10.6
    c: Distance(g45,g47) = 10
    c: Coincident(g49,g44)
    c: Diameter(g50) = 5.6
    c: Coincident(g50,g44)
    c: Distance(g51) = 11
    c: Symmetric(g51,g51,g33)
    c: DistanceX(g51,g43) = 9
    c: Diameter(g52) = 6
    c: Coincident(g52,g51)
    c: Diameter(g53) = 6
    c: Coincident(g53,g51)
    c: Coincident(g40,g55)
    c: Coincident(g39,g54)
    c: Coincident(g41,g57)
    c: Coincident(g42,g56)
    c: Diameter(g58) = 3
    c: Diameter(g59) = 3
    c: Diameter(g60) = 3
    c: Coincident(g58,g-44)
    c: Coincident(g59,g-46)
    c: Coincident(g60,g-45)
FEATURE [PartDesign::Body] Body  label="Struttura pistola"
  AllowCompound = false
  Group = -> [Sketch,Sketch002,Sketch004,DatumPlane,Sketch005,DatumPlane001,CopyCut,Sketch008,Sketch009,Sketch010,Sketch011,Sketch012,Sketch013,Sketch014,Sketch015,Sketch016,Sketch017,Sketch018,Sketch019,Sketch020,Sketch022,Sketch023,Sketch024,Sketch025,Sketch026,Sketch027,Sketch029,Sketch030,Sketch031,Sketch032,Sketch033,Sketch034,Sketch035,Sketch036,Sketch037,Sketch038,Sketch039,Sketch040,Sketch041,Sketch042,+15 more]
  Origin = -> Origin
FEATURE [Sketcher::SketchObject] Sketch078
  ArcFitTolerance = 1e-06
  AttachmentSupport = -> [XZ_Plane005]
  FullyConstrained = true
  MakeInternals = false
  MapMode = 5
  Placement = pos=(0,0,0) rot=(1,0,0;1.5708rad)
  sketch-geometry (5):
    g0: LineSegment [constr] StartX=0 StartY=5.5 StartZ=0 EndX=0 EndY=-5.5 EndZ=0
    g1: ArcOfCircle CenterX=0 CenterY=5.5 CenterZ=0 NormalX=0 NormalY=0 NormalZ=1 AngleXU=0 Radius=2.7 StartAngle=0 EndAngle=3.14159
    g2: ArcOfCircle CenterX=0 CenterY=-5.5 CenterZ=0 NormalX=0 NormalY=0 NormalZ=1 AngleXU=0 Radius=2.7 StartAngle=3.1416 EndAngle=6.28318
    g3: LineSegment StartX=-2.7 StartY=5.5 StartZ=0 EndX=-2.7 EndY=-5.50001 EndZ=0
    g4: LineSegment StartX=2.7 StartY=5.5 StartZ=0 EndX=2.7 EndY=-5.50001 EndZ=0
  constraints (13):
    c: Distance(g0) = 11
    c: Vertical(g0)
    c: Symmetric(g0,g0,g-1)
    c: Radius(g1) = 2.7
    c: Coincident(g1,g0)
    c: Radius(g2) = 2.7
    c: Coincident(g2,g0)
    c: Vertical(g3)
    c: Vertical(g4)
    c: Coincident(g2,g4)
    c: Coincident(g2,g3)
    c: Tangent(g3,g1) = -1.5708
    c: Tangent(g4,g1) = 1.5708
FEATURE [PartDesign::Pad] Pad002
  Direction = (0,-1,2e-16)
  Length = 0.8
  Length2 = 10
  Placement = pos=(0,0,0) rot=(1,0,0;1.5708rad)
  Profile = -> Sketch078
  ReferenceAxis = -> Sketch078 [N_Axis]
  Refine = true
  Suppressed = false
  Type = 0
FEATURE [Sketcher::SketchObject] Sketch079
  ArcFitTolerance = 1e-06
  AttachmentSupport = -> [XZ_Plane005]
  ExternalGeometry = -> [Sketch078]
  FullyConstrained = true
  MakeInternals = false
  MapMode = 5
  Placement = pos=(0,0,0) rot=(1,0,0;1.5708rad)
  sketch-geometry (2):
    g0: Circle CenterX=-1e-16 CenterY=5.5 CenterZ=0 NormalX=0 NormalY=0 NormalZ=1 AngleXU=0 Radius=2.7
    g1: Circle CenterX=0 CenterY=-5.5 CenterZ=0 NormalX=0 NormalY=0 NormalZ=1 AngleXU=0 Radius=2.7
  constraints (4):
    c: Coincident(g0,g-3)
    c: PointOnObject(g-3,g0)
    c: Coincident(g1,g-4)
    c: Equal(g1,g-4)
FEATURE [PartDesign::Pad] Pad003
  BaseFeature = -> Pad002
  Direction = (0,-1,2e-16)
  Length = 5
  Length2 = 10
  Placement = pos=(0,0,0) rot=(1,0,0;1.5708rad)
  Profile = -> Sketch079
  ReferenceAxis = -> Sketch079 [N_Axis]
  Refine = true
  Suppressed = false
  Type = 0
FEATURE [PartDesign::Fillet] Fillet001
  Base = -> Pad003 [Edge16,Edge14]
  BaseFeature = -> Pad003
  Placement = pos=(0,0,0) rot=(1,0,0;1.5708rad)
  Radius = 0.4
  Refine = true
  SupportTransform = false
  Suppressed = false
  UseAllEdges = false
FEATURE [PartDesign::Body] Body005  label="pulsanti lato destro"
  AllowCompound = false
  Group = -> [Sketch078,Pad002,Sketch079,Pad003,Fillet001]
  Origin = -> Origin005
  Tip = -> Fillet001
FEATURE [PartDesign::SubShapeBinder] Binder
  BindCopyOnChange = 0
  BindMode = 0
  ClaimChildren = false
  Context = -> Body006 [Binder.]
  Fuse = false
  MakeFace = true
  OffsetFill = false
  OffsetIntersection = false
  OffsetJoinType = 0
  OffsetOpenResult = false
  PartialLoad = false
  Refine = true
  Relative = true
  Support = -> [Body[Sketch074.]]
  _Version = 2
FEATURE [PartDesign::SubShapeBinder] Binder001
  BindCopyOnChange = 0
  BindMode = 0
  ClaimChildren = false
  Context = -> Body007 [Binder001.]
  Fuse = false
  MakeFace = true
  OffsetFill = false
  OffsetIntersection = false
  OffsetJoinType = 0
  OffsetOpenResult = false
  PartialLoad = false
  Refine = true
  Relative = true
  Support = -> [Body[Sketch075.]]
  _Version = 2
FEATURE [Mesh::Feature] logo_per_PCB_definitivo_positivo
  Placement = pos=(-191,17,-66) rot=(0,1,1;0rad)
FEATURE [Sketcher::SketchObject] Sketch114  label="Sketch114 - base lato DX"
  ArcFitTolerance = 1e-06
  AttachmentSupport = -> [Binder001]
  ExternalGeometry = -> [Binder001]
  FullyConstrained = true
  MakeInternals = false
  MapMode = 5
  Placement = pos=(0,1e-15,0) rot=(0,0.707107,0.707107;3.14159rad)
  sketch-geometry (30):
    g0: Circle CenterX=5.6 CenterY=34.8 CenterZ=0 NormalX=0 NormalY=0 NormalZ=1 AngleXU=0 Radius=1.8
    g1: Circle CenterX=5.6 CenterY=7.6 CenterZ=0 NormalX=0 NormalY=0 NormalZ=1 AngleXU=0 Radius=1.8
    g2: Circle CenterX=24.2 CenterY=26.7 CenterZ=0 NormalX=0 NormalY=0 NormalZ=1 AngleXU=0 Radius=3
    g3: Circle CenterX=24.2 CenterY=15.7 CenterZ=0 NormalX=0 NormalY=0 NormalZ=1 AngleXU=0 Radius=3
    g4: Circle CenterX=36.2 CenterY=21.2 CenterZ=0 NormalX=0 NormalY=0 NormalZ=1 AngleXU=0 Radius=2.8
    g5: Circle CenterX=78.51 CenterY=34.8 CenterZ=0 NormalX=0 NormalY=0 NormalZ=1 AngleXU=0 Radius=1.8
    g6: Circle CenterX=78.51 CenterY=7.6 CenterZ=0 NormalX=0 NormalY=0 NormalZ=1 AngleXU=0 Radius=1.8
    g7: Circle CenterX=184.08 CenterY=34.8 CenterZ=0 NormalX=0 NormalY=0 NormalZ=1 AngleXU=0 Radius=1.8
    g8: Circle CenterX=213.443 CenterY=-76.8316 CenterZ=0 NormalX=0 NormalY=0 NormalZ=1 AngleXU=0 Radius=1.8
    g9: Circle CenterX=179.305 CenterY=-76.8316 CenterZ=0 NormalX=0 NormalY=0 NormalZ=1 AngleXU=0 Radius=1.8
    g10: ArcOfCircle [constr] CenterX=132.428 CenterY=4 CenterZ=0 NormalX=0 NormalY=0 NormalZ=1 AngleXU=0 Radius=16 StartAngle=0.314159 EndAngle=1.5708
    g11: ArcOfCircle CenterX=107.6 CenterY=4 CenterZ=0 NormalX=0 NormalY=0 NormalZ=1 AngleXU=0 Radius=16 StartAngle=1.5708 EndAngle=3.00366
    g12: ArcOfCircle CenterX=207.583 CenterY=4 CenterZ=0 NormalX=0 NormalY=0 NormalZ=1 AngleXU=0 Radius=17 StartAngle=1.85815 EndAngle=3.57792
    g13: ArcOfCircle CenterX=184.801 CenterY=-67.3089 CenterZ=0 NormalX=0 NormalY=0 NormalZ=1 AngleXU=0 Radius=33.7833 StartAngle=5.88425 EndAngle=6.71952
    g14: LineSegment StartX=0 StartY=39.2 StartZ=0 EndX=0 EndY=3.2 EndZ=0
    g15: LineSegment StartX=0 StartY=3.2 StartZ=0 EndX=82.8 EndY=3.2 EndZ=0
    g16: LineSegment StartX=82.8 StartY=3.2 StartZ=0 EndX=82.8 EndY=6.2 EndZ=0
    g17: LineSegment StartX=82.8 StartY=6.2 StartZ=0 EndX=91.752 EndY=6.2 EndZ=0
    g18: LineSegment StartX=107.6 StartY=20 StartZ=0 EndX=132.428 EndY=20 EndZ=0
    g19: LineSegment StartX=147.645 StartY=8.94427 StartZ=0 EndX=176.685 EndY=-80.4316 EndZ=0
    g20: LineSegment StartX=176.685 StartY=-80.4316 StartZ=0 EndX=215.932 EndY=-80.4316 EndZ=0
    g21: LineSegment StartX=215.42 StartY=-53.0314 StartZ=0 EndX=192.176 EndY=-3.18451 EndZ=0
    g22: LineSegment StartX=202.765 StartY=20.303 StartZ=0 EndX=195.887 EndY=39.2 EndZ=0
    g23: LineSegment StartX=195.887 StartY=39.2 StartZ=0 EndX=0 EndY=39.2 EndZ=0
    g24: LineSegment StartX=196.467 StartY=26.4942 StartZ=0 EndX=194.073 EndY=33.0721 EndZ=0
    g25: LineSegment StartX=194.073 StartY=33.0721 StartZ=0 EndX=189.939 EndY=31.5672 EndZ=0
    g26: LineSegment StartX=189.939 StartY=31.5672 StartZ=0 EndX=192.333 EndY=24.9893 EndZ=0
    g27: LineSegment StartX=192.333 StartY=24.9893 StartZ=0 EndX=196.467 EndY=26.4942 EndZ=0
    g28: LineSegment StartX=132.428 StartY=20 StartZ=0 EndX=144.053 EndY=20 EndZ=0
    g29: LineSegment StartX=144.053 StartY=20 StartZ=0 EndX=147.645 EndY=8.94427 EndZ=0
  constraints (65):
    c: Equal(g0,g-25)
    c: Equal(g2,g-29)
    c: Equal(g3,g-30)
    c: Equal(g4,g-28)
    c: Equal(g1,g-26)
    c: Coincident(g0,g-25)
    c: Coincident(g1,g-26)
    c: Coincident(g2,g-29)
    c: Coincident(g3,g-30)
    c: Coincident(g4,g-28)
    c: Equal(g5,g-23)
    c: Equal(g6,g-24)
    c: Coincident(g5,g-23)
    c: Coincident(g6,g-24)
    c: Equal(g7,g-20)
    c: Coincident(g7,g-20)
    c: Equal(g9,g-22)
    c: Coincident(g9,g-22)
    c: Equal(g8,g-21)
    c: Coincident(g8,g-21)
    c: Equal(g13,g-12)
    c: Equal(g12,g-14)
    c: Equal(g10,g-9)
    c: Equal(g11,g-7)
    c: Coincident(g14,g-27)
    c: Coincident(g14,g-27)
    c: Coincident(g15,g14)
    c: Coincident(g15,g-5)
    c: Coincident(g16,g15)
    c: Coincident(g16,g-6)
    c: Coincident(g17,g16)
    c: Coincident(g17,g-7)
    c: Coincident(g11,g17)
    c: Coincident(g11,g-8)
    c: Coincident(g18,g11)
    c: Coincident(g18,g-9)
    c: Coincident(g10,g18)
    c: Coincident(g10,g-10)
    c: Coincident(g19,g10)
    c: Coincident(g19,g-11)
    c: Coincident(g20,g19)
    c: Coincident(g20,g-12)
    c: Coincident(g13,g20)
    c: Coincident(g13,g-13)
    c: Coincident(g21,g13)
    c: Coincident(g21,g-14)
    c: Coincident(g12,g21)
    c: Coincident(g12,g-15)
    c: Coincident(g22,g12)
    c: Coincident(g22,g-15)
    c: Coincident(g23,g22)
    c: Coincident(g23,g14)
    c: Coincident(g24,g-18)
    c: Coincident(g24,g-16)
    c: Coincident(g25,g24)
    c: Coincident(g25,g-19)
    c: Coincident(g26,g25)
    c: Coincident(g26,g-19)
    c: Coincident(g27,g26)
    c: Coincident(g27,g24)
    c: Coincident(g29,g10)
    c: Coincident(g28,g10)
    c: Coincident(g29,g28)
    c: Parallel(g28,g18)
    c: Parallel(g29,g19)
FEATURE [PartDesign::Pad] Pad011
  Direction = (0,1,-2e-16)
  Length = 2
  Length2 = 10
  Profile = -> Sketch114
  ReferenceAxis = -> Sketch114 [N_Axis]
  Refine = true
  Reversed = true
  Suppressed = false
  Type = 0
FEATURE [Sketcher::SketchObject] Sketch115
  ArcFitTolerance = 1e-06
  AttachmentSupport = -> [Pad011]
  ExternalGeometry = -> [Binder001]
  FullyConstrained = true
  MakeInternals = false
  MapMode = 5
  Placement = pos=(0,1.7e-15,0) rot=(0,0.707107,0.707107;3.14159rad)
  sketch-geometry (4):
    g0: ArcOfCircle CenterX=24.2 CenterY=26.7 CenterZ=0 NormalX=0 NormalY=0 NormalZ=1 AngleXU=0 Radius=3 StartAngle=4.48384e-08 EndAngle=3.14159
    g1: ArcOfCircle CenterX=24.2 CenterY=15.7 CenterZ=0 NormalX=0 NormalY=0 NormalZ=1 AngleXU=0 Radius=3 StartAngle=3.14159 EndAngle=6.28318
    g2: LineSegment StartX=21.2 StartY=26.7 StartZ=0 EndX=21.2 EndY=15.7 EndZ=0
    g3: LineSegment StartX=27.2 StartY=26.7 StartZ=0 EndX=27.2 EndY=15.7 EndZ=0
  constraints (12):
    c: Equal(g1,g-4)
    c: Equal(g0,g-3)
    c: Coincident(g0,g-3)
    c: Coincident(g1,g-4)
    c: Vertical(g2)
    c: Vertical(g3)
    c: Tangent(g3,g-3)
    c: Tangent(g2,g-3)
    c: Coincident(g0,g2)
    c: Coincident(g0,g3)
    c: Coincident(g1,g2)
    c: Coincident(g3,g1)
FEATURE [Sketcher::SketchObject] Sketch117  label="Sketch117 - fori per inserto M3 x 3 x 4.5"
  ArcFitTolerance = 1e-06
  AttachmentSupport = -> [Pad011]
  ExternalGeometry = -> [Binder001]
  FullyConstrained = true
  MakeInternals = false
  MapMode = 5
  Placement = pos=(0,1.7e-15,0) rot=(0,0.707107,0.707107;3.14159rad)
  sketch-geometry (4):
    g0: Circle CenterX=43.2 CenterY=30.3 CenterZ=0 NormalX=0 NormalY=0 NormalZ=1 AngleXU=0 Radius=2.25
    g1: Circle CenterX=43.2 CenterY=12.1 CenterZ=0 NormalX=0 NormalY=0 NormalZ=1 AngleXU=0 Radius=2.25
    g2: Circle CenterX=18.6 CenterY=30.3 CenterZ=0 NormalX=0 NormalY=0 NormalZ=1 AngleXU=0 Radius=2.25
    g3: Circle CenterX=18.6 CenterY=12.1 CenterZ=0 NormalX=0 NormalY=0 NormalZ=1 AngleXU=0 Radius=2.25
  constraints (8):
    c: Diameter(g0) = 4.5
    c: Diameter(g1) = 4.5
    c: Diameter(g2) = 4.5
    c: Diameter(g3) = 4.5
    c: Coincident(g2,g-3)
    c: Coincident(g3,g-6)
    c: Coincident(g0,g-4)
    c: Coincident(g1,g-5)
FEATURE [Sketcher::SketchObject] Sketch118
  ArcFitTolerance = 1e-06
  AttachmentSupport = -> [Pad011]
  ExternalGeometry = -> [Binder001]
  FullyConstrained = true
  MakeInternals = false
  MapMode = 5
  Placement = pos=(0,-2,0) rot=(1,0,0;1.5708rad)
  sketch-geometry (12):
    g0: Circle CenterX=-78.51 CenterY=34.8 CenterZ=0 NormalX=0 NormalY=0 NormalZ=1 AngleXU=0 Radius=1.8
    g1: Circle CenterX=-78.51 CenterY=7.6 CenterZ=0 NormalX=0 NormalY=0 NormalZ=1 AngleXU=0 Radius=1.8
    g2: Circle CenterX=-5.6 CenterY=34.8 CenterZ=0 NormalX=0 NormalY=0 NormalZ=1 AngleXU=0 Radius=1.8
    g3: Circle CenterX=-5.6 CenterY=7.6 CenterZ=0 NormalX=0 NormalY=0 NormalZ=1 AngleXU=0 Radius=1.8
    g4: LineSegment StartX=0 StartY=39.2 StartZ=0 EndX=0 EndY=3.2 EndZ=0
    g5: LineSegment StartX=0 StartY=3.2 StartZ=0 EndX=-82.8 EndY=3.2 EndZ=0
    g6: LineSegment StartX=-82.8 StartY=3.2 StartZ=0 EndX=-82.8 EndY=39.2 EndZ=0
    g7: LineSegment StartX=-82.8 StartY=39.2 StartZ=0 EndX=0 EndY=39.2 EndZ=0
    g8: ArcOfCircle CenterX=-65 CenterY=21.2 CenterZ=0 NormalX=0 NormalY=0 NormalZ=1 AngleXU=0 Radius=10 StartAngle=1.5708 EndAngle=4.71239
    g9: ArcOfCircle CenterX=-19 CenterY=21.2 CenterZ=0 NormalX=0 NormalY=0 NormalZ=1 AngleXU=0 Radius=10 StartAngle=4.71239 EndAngle=7.85398
    g10: LineSegment StartX=-65 StartY=31.2 StartZ=0 EndX=-19 EndY=31.2 EndZ=0
    g11: LineSegment StartX=-65 StartY=11.2 StartZ=0 EndX=-19 EndY=11.2 EndZ=0
  constraints (25):
    c: Equal(g2,g-5)
    c: Equal(g3,g-7)
    c: Equal(g1,g-6)
    c: Equal(g0,g-4)
    c: Coincident(g0,g-4)
    c: Coincident(g1,g-6)
    c: Coincident(g3,g-7)
    c: Coincident(g2,g-5)
    c: Coincident(g4,g-8)
    c: Coincident(g4,g-9)
    c: Coincident(g5,g4)
    c: Coincident(g5,g-10)
    c: Coincident(g6,g5)
    c: PointOnObject(g6,g-3)
    c: Vertical(g6)
    c: Coincident(g7,g6)
    c: Coincident(g7,g4)
    c: Tangent(g8,g10) = 1.5708
    c: Tangent(g8,g11) = -1.5708
    c: Tangent(g9,g10) = 1.5708
    c: Tangent(g9,g11) = -1.5708
    c: Equal(g8,g9)
    c: Radius(g8) = 10
    c: Coincident(g8,g-11)
    c: Coincident(g9,g-12)
FEATURE [Sketcher::SketchObject] Sketch120
  ArcFitTolerance = 1e-06
  AttachmentSupport = -> [Pad011]
  ExternalGeometry = -> [Binder001]
  FullyConstrained = true
  MakeInternals = false
  MapMode = 5
  Placement = pos=(0,-2,0) rot=(1,0,0;1.5708rad)
  sketch-geometry (4):
    g0: LineSegment StartX=-137.815 StartY=39.2 StartZ=0 EndX=-142.655 EndY=24.303 EndZ=0
    g1: LineSegment StartX=-137.815 StartY=39.2 StartZ=0 EndX=-110.815 EndY=39.2 EndZ=0
    g2: LineSegment StartX=-142.655 StartY=24.303 StartZ=0 EndX=-110.815 EndY=24.303 EndZ=0
    g3: ArcOfCircle CenterX=-92.2534 CenterY=31.7515 CenterZ=0 NormalX=0 NormalY=0 NormalZ=1 AngleXU=0 Radius=20 StartAngle=2.75997 EndAngle=3.52321
  constraints (12):
    c: PointOnObject(g0,g-3)
    c: Coincident(g1,g0)
    c: PointOnObject(g1,g-3)
    c: Coincident(g2,g0)
    c: Horizontal(g2)
    c: Tangent(g0,g-4)
    c: Vertical(g2,g1)
    c: DistanceX(g1,g1) = 27
    c: DistanceY(g-6,g0) = 4
    c: Radius(g3) = 20
    c: Coincident(g3,g1)
    c: Coincident(g3,g2)
FEATURE [Sketcher::SketchObject] Sketch121
  ArcFitTolerance = 1e-06
  AttachmentSupport = -> [Pad011]
  ExternalGeometry = -> [Binder001]
  FullyConstrained = true
  MakeInternals = false
  MapMode = 5
  Placement = pos=(0,-2,0) rot=(1,0,0;1.5708rad)
  sketch-geometry (15):
    g0: LineSegment StartX=-137.815 StartY=39.2 StartZ=0 EndX=-143.955 EndY=20.303 EndZ=0
    g1: LineSegment StartX=-143.955 StartY=20.303 StartZ=0 EndX=-190.141 EndY=20.303 EndZ=0
    g2: LineSegment StartX=-190.141 StartY=20.303 StartZ=0 EndX=-186.139 EndY=31.3 EndZ=0
    g3: LineSegment StartX=-178.754 StartY=39.2 StartZ=0 EndX=-180.791 EndY=33.6029 EndZ=0
    g4: ArcOfCircle CenterX=-184.08 CenterY=34.8 CenterZ=0 NormalX=0 NormalY=0 NormalZ=1 AngleXU=0 Radius=3.5 StartAngle=4.71239 EndAngle=5.93412
    g5: LineSegment StartX=-184.08 StartY=31.3 StartZ=0 EndX=-186.139 EndY=31.3 EndZ=0
    g6: LineSegment StartX=-137.815 StartY=39.2 StartZ=0 EndX=-156.815 EndY=39.2 EndZ=0
    g7: LineSegment StartX=-168.815 StartY=39.2 StartZ=0 EndX=-178.754 EndY=39.2 EndZ=0
    g8: LineSegment StartX=-157.815 StartY=39.2 StartZ=0 EndX=-167.815 EndY=39.2 EndZ=0
    g9: LineSegment StartX=-168.815 StartY=31.2 StartZ=0 EndX=-156.815 EndY=31.2 EndZ=0
    g10: LineSegment StartX=-167.436 StartY=36.2 StartZ=0 EndX=-157.436 EndY=36.2 EndZ=0
    g11: ArcOfCircle CenterX=-176.411 CenterY=35.2 CenterZ=0 NormalX=0 NormalY=0 NormalZ=1 AngleXU=0 Radius=20 StartAngle=6.08183 EndAngle=6.48454
    g12: ArcOfCircle CenterX=-188.411 CenterY=35.2 CenterZ=0 NormalX=0 NormalY=0 NormalZ=1 AngleXU=0 Radius=20 StartAngle=6.08183 EndAngle=6.48454
    g13: ArcOfCircle CenterX=-177.411 CenterY=35.2 CenterZ=0 NormalX=0 NormalY=0 NormalZ=1 AngleXU=0 Radius=20 StartAngle=0.0500209 EndAngle=0.201358
    g14: ArcOfCircle CenterX=-187.411 CenterY=35.2 CenterZ=0 NormalX=0 NormalY=0 NormalZ=1 AngleXU=0 Radius=20 StartAngle=0.0500209 EndAngle=0.201358
  constraints (46):
    c: PointOnObject(g0,g-3)
    c: Tangent(g0,g-5)
    c: Coincident(g1,g0)
    c: Horizontal(g1)
    c: Coincident(g2,g1)
    c: PointOnObject(g3,g-3)
    c: Parallel(g3,g-6)
    c: Parallel(g2,g-6)
    c: Radius(g4) = 3.5
    c: Coincident(g4,g-7)
    c: Tangent(g3,g4) = 1.5708
    c: Horizontal(g5)
    c: Tangent(g5,g4) = 1.5708
    c: DistanceX(g-8,g5) = 3.8
    c: Coincident(g2,g5)
    c: Coincident(g6,g0)
    c: PointOnObject(g6,g-3)
    c: DistanceX(g6,g6) = 19
    c: PointOnObject(g7,g-3)
    c: DistanceX(g7,g6) = 12
    c: Coincident(g7,g3)
    c: PointOnObject(g8,g-3)
    c: PointOnObject(g8,g-3)
    c: DistanceX(g8,g8) = 10
    c: DistanceX(g8,g6) = 1
    c: Horizontal(g9)
    c: Vertical(g7,g9)
    c: Vertical(g6,g9)
    c: DistanceY(g9,g7) = 8
    c: Horizontal(g10)
    c: Equal(g8,g10)
    c: DistanceY(g10,g8) = 3
    c: Radius(g11) = 20
    c: Coincident(g11,g6)
    c: Coincident(g11,g9)
    c: Radius(g12) = 20
    c: Coincident(g12,g7)
    c: Coincident(g12,g9)
    c: Equal(g13,g11)
    c: Coincident(g13,g8)
    c: Coincident(g13,g10)
    c: Horizontal(g13,g11)
    c: Equal(g14,g12)
    c: Coincident(g14,g8)
    c: Coincident(g14,g10)
    c: Horizontal(g1,g-6)
FEATURE [Sketcher::SketchObject] Sketch122
  ArcFitTolerance = 1e-06
  AttachmentSupport = -> [Pad011]
  ExternalGeometry = -> [Binder001]
  FullyConstrained = true
  MakeInternals = false
  MapMode = 5
  Placement = pos=(0,-2,0) rot=(1,0,0;1.5708rad)
  sketch-geometry (8):
    g0: LineSegment StartX=-202.765 StartY=20.303 StartZ=0 EndX=-143.955 EndY=20.303 EndZ=0
    g1: ArcOfCircle CenterX=-184.801 CenterY=-67.3089 CenterZ=0 NormalX=0 NormalY=0 NormalZ=1 AngleXU=0 Radius=33.7833 StartAngle=2.70526 EndAngle=3.54053
    g2: LineSegment StartX=-176.685 StartY=-80.4316 StartZ=0 EndX=-215.932 EndY=-80.4316 EndZ=0
    g3: LineSegment StartX=-215.42 StartY=-53.0315 StartZ=0 EndX=-192.176 EndY=-3.18454 EndZ=0
    g4: ArcOfCircle CenterX=-207.583 CenterY=4 CenterZ=0 NormalX=0 NormalY=0 NormalZ=1 AngleXU=0 Radius=17 StartAngle=5.84685 EndAngle=7.56663
    g5: Circle CenterX=-213.443 CenterY=-76.8316 CenterZ=0 NormalX=0 NormalY=0 NormalZ=1 AngleXU=0 Radius=3
    g6: Circle CenterX=-179.305 CenterY=-76.8316 CenterZ=0 NormalX=0 NormalY=0 NormalZ=1 AngleXU=0 Radius=3
    g7: LineSegment StartX=-143.955 StartY=20.303 StartZ=0 EndX=-176.685 EndY=-80.4316 EndZ=0
  constraints (18):
    c: Coincident(g0,g-6)
    c: Coincident(g1,g-7)
    c: Coincident(g1,g-8)
    c: Coincident(g2,g1)
    c: Tangent(g3,g-5)
    c: Coincident(g4,g-6)
    c: Coincident(g4,g0)
    c: Coincident(g3,g4)
    c: Coincident(g1,g3)
    c: Diameter(g5) = 6
    c: Diameter(g6) = 6
    c: Coincident(g5,g-9)
    c: Coincident(g6,g-10)
    c: Horizontal(g0)
    c: Horizontal(g2)
    c: Coincident(g7,g0)
    c: Coincident(g7,g2)
    c: Tangent(g7,g-4)
FEATURE [Sketcher::SketchObject] Sketch123
  ArcFitTolerance = 1e-06
  AttachmentSupport = -> [Pad011]
  ExternalGeometry = -> [Binder001]
  FullyConstrained = true
  MakeInternals = false
  MapMode = 5
  Placement = pos=(0,-2,0) rot=(1,0,0;1.5708rad)
  sketch-geometry (4):
    g0: LineSegment StartX=-108 StartY=36.8 StartZ=0 EndX=-90 EndY=36.8 EndZ=0
    g1: LineSegment StartX=-108 StartY=36.8 StartZ=0 EndX=-108 EndY=26.8 EndZ=0
    g2: LineSegment StartX=-108 StartY=26.8 StartZ=0 EndX=-90 EndY=26.8 EndZ=0
    g3: ArcOfCircle CenterX=-94 CenterY=31.8 CenterZ=0 NormalX=0 NormalY=0 NormalZ=1 AngleXU=0 Radius=6.40312 StartAngle=5.38713 EndAngle=7.17924
  constraints (13):
    c: Horizontal(g0)
    c: Coincident(g1,g0)
    c: Vertical(g1)
    c: Coincident(g2,g1)
    c: Horizontal(g2)
    c: DistanceX(g0,g0) = 18
    c: DistanceY(g1,g1) = 10
    c: Equal(g0,g2)
    c: DistanceX(g0,g-3) = 90
    c: DistanceY(g0,g-3) = 2.4
    c: Coincident(g3,g0)
    c: Coincident(g3,g2)
    c: DistanceX(g3,g0) = 4
FEATURE [PartDesign::Chamfer] Chamfer014
  Angle = 45
  Base = -> Pad011 [Edge80,Edge4,Edge7]
  BaseFeature = -> Pad011
  ChamferType = 0
  FlipDirection = false
  Refine = true
  Size = 1.9
  Size2 = 1
  SupportTransform = false
  Suppressed = false
  UseAllEdges = false
FEATURE [PartDesign::Pocket] Pocket006
  BaseFeature = -> Chamfer014
  Direction = (0,-1,2e-16)
  Length = 1.2
  Length2 = 5
  Profile = -> Sketch115
  ReferenceAxis = -> Sketch115 [N_Axis]
  Refine = true
  Suppressed = false
  Type = 0
FEATURE [Sketcher::SketchObject] Sketch116  label="Sketch116 - pieno per inserto M3 x 3 x 4,5"
  ArcFitTolerance = 1e-06
  AttachmentSupport = -> [Pocket006]
  ExternalGeometry = -> [Binder001]
  FullyConstrained = true
  MakeInternals = false
  MapMode = 5
  Placement = pos=(0,1.7e-15,0) rot=(0,0.707107,0.707107;3.14159rad)
  sketch-geometry (4):
    g0: Circle CenterX=43.2 CenterY=30.3 CenterZ=0 NormalX=0 NormalY=0 NormalZ=1 AngleXU=0 Radius=3.4
    g1: Circle CenterX=43.2 CenterY=12.1 CenterZ=0 NormalX=0 NormalY=0 NormalZ=1 AngleXU=0 Radius=3.4
    g2: Circle CenterX=18.6 CenterY=30.3 CenterZ=0 NormalX=0 NormalY=0 NormalZ=1 AngleXU=0 Radius=3.4
    g3: Circle CenterX=18.6 CenterY=12.1 CenterZ=0 NormalX=0 NormalY=0 NormalZ=1 AngleXU=0 Radius=3.4
  constraints (8):
    c: Diameter(g0) = 6.8
    c: Diameter(g1) = 6.8
    c: Diameter(g2) = 6.8
    c: Diameter(g3) = 6.8
    c: Coincident(g2,g-3)
    c: Coincident(g0,g-4)
    c: Coincident(g3,g-6)
    c: Coincident(g1,g-5)
FEATURE [PartDesign::Pad] Pad012
  BaseFeature = -> Pocket006
  Direction = (0,1,-2e-16)
  Length = 2.4
  Length2 = 10
  Profile = -> Sketch116
  ReferenceAxis = -> Sketch116 [N_Axis]
  Refine = true
  Suppressed = false
  Type = 0
FEATURE [PartDesign::Pocket] Pocket007
  BaseFeature = -> Pad012
  Direction = (0,-1,2e-16)
  Length = 0.6
  Length2 = 2.4
  Profile = -> Sketch117
  ReferenceAxis = -> Sketch117 [N_Axis]
  Refine = true
  Suppressed = false
  Type = 4
FEATURE [PartDesign::Pad] Pad013
  BaseFeature = -> Pocket007
  Direction = (0,-1,2e-16)
  Length = 1.6
  Length2 = 10
  Profile = -> Sketch118
  ReferenceAxis = -> Sketch118 [N_Axis]
  Refine = true
  Suppressed = false
  Type = 0
FEATURE [Sketcher::SketchObject] Sketch119
  ArcFitTolerance = 1e-06
  AttachmentSupport = -> [Pad013]
  ExternalGeometry = -> [Binder001]
  FullyConstrained = true
  MakeInternals = false
  MapMode = 5
  Placement = pos=(0,-3.6,0) rot=(1,0,0;1.5708rad)
  sketch-geometry (21):
    g0: LineSegment [constr] StartX=-82.8 StartY=3.2 StartZ=0 EndX=-82.8 EndY=39.2 EndZ=0
    g1: ArcOfCircle CenterX=-78.51 CenterY=34.8 CenterZ=0 NormalX=0 NormalY=0 NormalZ=1 AngleXU=0 Radius=3.5 StartAngle=4.71239 EndAngle=6.28319
    g2: ArcOfCircle CenterX=-78.51 CenterY=7.6 CenterZ=0 NormalX=0 NormalY=0 NormalZ=1 AngleXU=0 Radius=3.5 StartAngle=0 EndAngle=1.5708
    g3: ArcOfCircle CenterX=-5.6 CenterY=34.8 CenterZ=0 NormalX=0 NormalY=0 NormalZ=1 AngleXU=0 Radius=3.5 StartAngle=3.14159 EndAngle=4.71239
    g4: ArcOfCircle CenterX=-5.6 CenterY=7.6 CenterZ=0 NormalX=0 NormalY=0 NormalZ=1 AngleXU=0 Radius=3.5 StartAngle=1.5708 EndAngle=3.14159
    g5: LineSegment StartX=0 StartY=39.2 StartZ=0 EndX=0 EndY=31.3 EndZ=0
    g6: LineSegment StartX=0 StartY=39.2 StartZ=0 EndX=-9.1 EndY=39.2 EndZ=0
    g7: LineSegment StartX=0 StartY=3.2 StartZ=0 EndX=0 EndY=11.1 EndZ=0
    g8: LineSegment StartX=0 StartY=3.2 StartZ=0 EndX=-9.1 EndY=3.2 EndZ=0
    g9: LineSegment StartX=-82.8 StartY=3.2 StartZ=0 EndX=-75.01 EndY=3.2 EndZ=0
    g10: LineSegment StartX=-82.8 StartY=3.2 StartZ=0 EndX=-82.8 EndY=11.1 EndZ=0
    g11: LineSegment StartX=-82.8 StartY=39.2 StartZ=0 EndX=-82.8 EndY=31.3 EndZ=0
    g12: LineSegment StartX=-82.8 StartY=39.2 StartZ=0 EndX=-75.01 EndY=39.2 EndZ=0
    g13: LineSegment StartX=-82.8 StartY=31.3 StartZ=0 EndX=-78.51 EndY=31.3 EndZ=0
    g14: LineSegment StartX=-75.01 StartY=39.2 StartZ=0 EndX=-75.01 EndY=34.8 EndZ=0
    g15: LineSegment StartX=-82.8 StartY=11.1 StartZ=0 EndX=-78.51 EndY=11.1 EndZ=0
    g16: LineSegment StartX=-75.01 StartY=3.2 StartZ=0 EndX=-75.01 EndY=7.6 EndZ=0
    g17: LineSegment StartX=-9.1 StartY=39.2 StartZ=0 EndX=-9.1 EndY=34.8 EndZ=0
    g18: LineSegment StartX=0 StartY=31.3 StartZ=0 EndX=-5.6 EndY=31.3 EndZ=0
    g19: LineSegment StartX=0 StartY=11.1 StartZ=0 EndX=-5.6 EndY=11.1 EndZ=0
    g20: LineSegment StartX=-9.1 StartY=3.2 StartZ=0 EndX=-9.1 EndY=7.6 EndZ=0
  constraints (51):
    c: Coincident(g0,g-10)
    c: PointOnObject(g0,g-8)
    c: Vertical(g0)
    c: Coincident(g1,g-3)
    c: Coincident(g2,g-4)
    c: Coincident(g3,g-5)
    c: Coincident(g4,g-6)
    c: Radius(g4) = 3.5
    c: Radius(g3) = 3.5
    c: Radius(g1) = 3.5
    c: Radius(g2) = 3.5
    c: Coincident(g5,g-9)
    c: PointOnObject(g5,g-9)
    c: Coincident(g6,g5)
    c: PointOnObject(g6,g-8)
    c: Coincident(g7,g-9)
    c: PointOnObject(g7,g-9)
    c: Coincident(g8,g7)
    c: PointOnObject(g8,g-7)
    c: Coincident(g9,g0)
    c: PointOnObject(g9,g-7)
    c: Coincident(g10,g0)
    c: PointOnObject(g10,g0)
    c: Coincident(g11,g0)
    c: PointOnObject(g11,g0)
    c: Coincident(g12,g0)
    c: PointOnObject(g12,g-8)
    c: Coincident(g13,g11)
    c: Horizontal(g13)
    c: Coincident(g14,g12)
    c: Vertical(g14)
    c: Coincident(g15,g10)
    c: Horizontal(g15)
    c: Coincident(g16,g9)
    c: Vertical(g16)
    c: Coincident(g17,g6)
    c: Vertical(g17)
    c: Coincident(g18,g5)
    c: Horizontal(g18)
    c: Coincident(g19,g7)
    c: Horizontal(g19)
    c: Coincident(g20,g8)
    c: Vertical(g20)
    c: Tangent(g20,g4) = 1.5708
    c: Tangent(g4,g19) = -1.5708
    c: Tangent(g18,g3) = 1.5708
    c: Tangent(g3,g17) = -1.5708
    c: Tangent(g13,g1) = -1.5708
    c: Tangent(g1,g14) = 1.5708
    c: Tangent(g16,g2) = -1.5708
    c: Tangent(g2,g15) = 1.5708
FEATURE [PartDesign::Pocket] Pocket008
  BaseFeature = -> Pad013
  Direction = (0,1,-2e-16)
  Length = 1.6
  Length2 = 5
  Profile = -> Sketch119
  ReferenceAxis = -> Sketch119 [N_Axis]
  Refine = true
  Suppressed = false
  Type = 0
FEATURE [PartDesign::Pad] Pad017
  BaseFeature = -> Pocket008
  Direction = (0,-1,2e-16)
  Length = 1.6
  Length2 = 10
  Profile = -> Sketch123
  ReferenceAxis = -> Sketch123 [N_Axis]
  Refine = true
  Suppressed = false
  Type = 0
FEATURE [Sketcher::SketchObject] Sketch125
  ArcFitTolerance = 1e-06
  AttachmentSupport = -> [Pad017]
  ExternalGeometry = -> [Pad017]
  FullyConstrained = true
  MakeInternals = false
  MapMode = 5
  Placement = pos=(0,-3.6,8e-16) rot=(1,0,0;1.5708rad)
  sketch-geometry (20):
    g0: LineSegment StartX=-108 StartY=35.8 StartZ=0 EndX=-108 EndY=35 EndZ=0
    g1: LineSegment StartX=-108 StartY=35 StartZ=0 EndX=-97 EndY=35 EndZ=0
    g2: LineSegment StartX=-97 StartY=35 StartZ=0 EndX=-97 EndY=35.8 EndZ=0
    g3: LineSegment StartX=-97 StartY=35.8 StartZ=0 EndX=-108 EndY=35.8 EndZ=0
    g4: LineSegment StartX=-108 StartY=28.6 StartZ=0 EndX=-108 EndY=27.8 EndZ=0
    g5: LineSegment StartX=-108 StartY=27.8 StartZ=0 EndX=-97 EndY=27.8 EndZ=0
    g6: LineSegment StartX=-97 StartY=27.8 StartZ=0 EndX=-97 EndY=28.6 EndZ=0
    g7: LineSegment StartX=-97 StartY=28.6 StartZ=0 EndX=-108 EndY=28.6 EndZ=0
    g8: LineSegment StartX=-108 StartY=30.4 StartZ=0 EndX=-108 EndY=29.6 EndZ=0
    g9: LineSegment StartX=-108 StartY=29.6 StartZ=0 EndX=-97 EndY=29.6 EndZ=0
    g10: LineSegment StartX=-97 StartY=29.6 StartZ=0 EndX=-97 EndY=30.4 EndZ=0
    g11: LineSegment StartX=-97 StartY=30.4 StartZ=0 EndX=-108 EndY=30.4 EndZ=0
    g12: LineSegment StartX=-108 StartY=32.2 StartZ=0 EndX=-108 EndY=31.4 EndZ=0
    g13: LineSegment StartX=-108 StartY=31.4 StartZ=0 EndX=-97 EndY=31.4 EndZ=0
    g14: LineSegment StartX=-97 StartY=31.4 StartZ=0 EndX=-97 EndY=32.2 EndZ=0
    g15: LineSegment StartX=-97 StartY=32.2 StartZ=0 EndX=-108 EndY=32.2 EndZ=0
    g16: LineSegment StartX=-108 StartY=34 StartZ=0 EndX=-108 EndY=33.2 EndZ=0
    g17: LineSegment StartX=-108 StartY=33.2 StartZ=0 EndX=-97 EndY=33.2 EndZ=0
    g18: LineSegment StartX=-97 StartY=33.2 StartZ=0 EndX=-97 EndY=34 EndZ=0
    g19: LineSegment StartX=-97 StartY=34 StartZ=0 EndX=-108 EndY=34 EndZ=0
  constraints (55):
    c: Coincident(g1,g0)
    c: Horizontal(g1)
    c: Coincident(g2,g1)
    c: Vertical(g2)
    c: Coincident(g3,g2)
    c: Horizontal(g3)
    c: Coincident(g3,g0)
    c: DistanceX(g1,g1) = 11
    c: DistanceY(g2,g2) = 0.8
    c: Coincident(g5,g4)
    c: Horizontal(g5)
    c: Coincident(g6,g5)
    c: Vertical(g6)
    c: Coincident(g7,g6)
    c: Horizontal(g7)
    c: Coincident(g7,g4)
    c: Coincident(g9,g8)
    c: Horizontal(g9)
    c: Coincident(g10,g9)
    c: Vertical(g10)
    c: Coincident(g11,g10)
    c: Horizontal(g11)
    c: Coincident(g11,g8)
    c: Coincident(g13,g12)
    c: Horizontal(g13)
    c: Coincident(g14,g13)
    c: Vertical(g14)
    c: Coincident(g15,g14)
    c: Horizontal(g15)
    c: Coincident(g15,g12)
    c: Coincident(g17,g16)
    c: Horizontal(g17)
    c: Coincident(g18,g17)
    c: Vertical(g18)
    c: Coincident(g19,g18)
    c: Horizontal(g19)
    c: Coincident(g19,g16)
    c: Equal(g3,g19)
    c: Equal(g3,g15)
    c: Equal(g3,g11)
    c: Equal(g3,g7)
    c: Equal(g2,g18)
    c: Equal(g2,g14)
    c: Equal(g2,g10)
    c: Equal(g2,g6)
    c: DistanceY(g-4,g4) = 1
    c: DistanceY(g4,g8) = 1
    c: DistanceY(g8,g12) = 1
    c: DistanceY(g12,g16) = 1
    c: DistanceY(g16,g0) = 1
    c: Tangent(g0,g-5)
    c: Tangent(g16,g-5)
    c: Tangent(g12,g-5)
    c: Tangent(g8,g-5)
    c: Tangent(g4,g-5)
FEATURE [PartDesign::Chamfer] Chamfer009
  Angle = 45
  Base = -> Pad017 [Edge151,Edge154]
  BaseFeature = -> Pad017
  ChamferType = 1
  FlipDirection = false
  Refine = true
  Size = 1.5
  Size2 = 2.8
  SupportTransform = false
  Suppressed = false
  UseAllEdges = false
FEATURE [PartDesign::Pocket] Pocket009
  BaseFeature = -> Chamfer009
  Direction = (0,1,-2e-16)
  Length = 1
  Length2 = 5
  Profile = -> Sketch125
  ReferenceAxis = -> Sketch125 [N_Axis]
  Refine = true
  Suppressed = false
  Type = 0
FEATURE [PartDesign::Pad] Pad014
  BaseFeature = -> Pocket009
  Direction = (0,-1,2e-16)
  Length = 0.8
  Length2 = 10
  Profile = -> Sketch120
  ReferenceAxis = -> Sketch120 [N_Axis]
  Refine = true
  Suppressed = false
  Type = 0
FEATURE [Sketcher::SketchObject] Sketch124
  ArcFitTolerance = 1e-06
  AttachmentSupport = -> [Pad014]
  ExternalGeometry = -> [Binder001]
  FullyConstrained = true
  MakeInternals = false
  MapMode = 5
  Placement = pos=(0,-2.8,6e-16) rot=(1,0,0;1.5708rad)
  sketch-geometry (4):
    g0: LineSegment StartX=-129 StartY=39.2 StartZ=0 EndX=-131.599 EndY=31.2 EndZ=0
    g1: LineSegment StartX=-118 StartY=39.2 StartZ=0 EndX=-120.599 EndY=31.2 EndZ=0
    g2: LineSegment StartX=-129 StartY=39.2 StartZ=0 EndX=-118 EndY=39.2 EndZ=0
    g3: LineSegment StartX=-120.599 StartY=31.2 StartZ=0 EndX=-131.599 EndY=31.2 EndZ=0
  constraints (12):
    c: PointOnObject(g0,g-3)
    c: PointOnObject(g1,g-3)
    c: Parallel(g-4,g0)
    c: Parallel(g-4,g1)
    c: Coincident(g2,g0)
    c: Coincident(g2,g1)
    c: DistanceX(g2,g2) = 11
    c: DistanceY(g1,g1) = 8
    c: Coincident(g3,g1)
    c: Horizontal(g3)
    c: Coincident(g3,g0)
    c: DistanceX(g1,g-3) = 118
FEATURE [PartDesign::Pad] Pad018
  BaseFeature = -> Pad014
  Direction = (0,-1,2e-16)
  Length = 1.2
  Length2 = 10
  Profile = -> Sketch124
  ReferenceAxis = -> Sketch124 [N_Axis]
  Refine = true
  Suppressed = false
  Type = 0
FEATURE [Sketcher::SketchObject] Sketch126
  ArcFitTolerance = 1e-06
  AttachmentSupport = -> [Pad018]
  ExternalGeometry = -> [Pad018]
  FullyConstrained = true
  MakeInternals = false
  MapMode = 5
  Placement = pos=(0,-4,0) rot=(1,0,0;1.5708rad)
  sketch-geometry (8):
    g0: LineSegment StartX=-129.877 StartY=36.5 StartZ=0 EndX=-130.137 EndY=35.7 EndZ=0
    g1: LineSegment StartX=-130.69 StartY=34 StartZ=0 EndX=-130.95 EndY=33.2 EndZ=0
    g2: LineSegment StartX=-129.877 StartY=36.5 StartZ=0 EndX=-118.877 EndY=36.5 EndZ=0
    g3: LineSegment StartX=-130.137 StartY=35.7 StartZ=0 EndX=-119.137 EndY=35.7 EndZ=0
    g4: LineSegment StartX=-130.69 StartY=34 StartZ=0 EndX=-119.69 EndY=34 EndZ=0
    g5: LineSegment StartX=-130.95 StartY=33.2 StartZ=0 EndX=-119.95 EndY=33.2 EndZ=0
    g6: LineSegment StartX=-118.877 StartY=36.5 StartZ=0 EndX=-119.137 EndY=35.7 EndZ=0
    g7: LineSegment StartX=-119.69 StartY=34 StartZ=0 EndX=-119.95 EndY=33.2 EndZ=0
  constraints (20):
    c: Coincident(g2,g0)
    c: Horizontal(g2)
    c: Coincident(g3,g0)
    c: Horizontal(g3)
    c: Coincident(g4,g1)
    c: Horizontal(g4)
    c: Coincident(g5,g1)
    c: Horizontal(g5)
    c: Coincident(g6,g2)
    c: Coincident(g6,g3)
    c: Coincident(g7,g4)
    c: Coincident(g7,g5)
    c: Tangent(g0,g-4)
    c: Tangent(g6,g-5)
    c: Tangent(g1,g-4)
    c: Tangent(g7,g-5)
    c: DistanceY(g3,g2) = 0.8
    c: DistanceY(g5,g4) = 0.8
    c: DistanceY(g-6,g1) = 2
    c: DistanceY(g-6,g0) = 4.5
FEATURE [PartDesign::Chamfer] Chamfer008
  Angle = 45
  Base = -> Pad018 [Edge257]
  BaseFeature = -> Pad018
  ChamferType = 1
  FlipDirection = false
  Refine = true
  Size = 1
  Size2 = 6
  SupportTransform = false
  Suppressed = false
  UseAllEdges = false
FEATURE [PartDesign::Pocket] Pocket010
  BaseFeature = -> Chamfer008
  Direction = (0,1,-2e-16)
  Length = 1
  Length2 = 5
  Profile = -> Sketch126
  ReferenceAxis = -> Sketch126 [N_Axis]
  Refine = true
  Suppressed = false
  Type = 0
FEATURE [PartDesign::Pad] Pad015
  BaseFeature = -> Pocket010
  Direction = (0,-1,2e-16)
  Length = 2
  Length2 = 10
  Profile = -> Sketch121
  ReferenceAxis = -> Sketch121 [N_Axis]
  Refine = true
  Suppressed = false
  Type = 0
FEATURE [PartDesign::Pad] Pad016
  BaseFeature = -> Pad015
  Direction = (0,-1,2e-16)
  Length = 1.6
  Length2 = 10
  Profile = -> Sketch122
  ReferenceAxis = -> Sketch122 [N_Axis]
  Refine = true
  Suppressed = false
  Type = 0
FEATURE [Sketcher::SketchObject] Sketch127
  ArcFitTolerance = 1e-06
  AttachmentSupport = -> [Pad016]
  ExternalGeometry = -> [Pad016]
  FullyConstrained = true
  MakeInternals = false
  MapMode = 5
  Placement = pos=(0,0,-80.4316) rot=(1,0,0;3.14159rad)
  sketch-geometry (8):
    g0: LineSegment StartX=-176.685 StartY=3.6 StartZ=0 EndX=-186.685 EndY=3.6 EndZ=0
    g1: LineSegment [constr] StartX=-186.685 StartY=3.6 StartZ=0 EndX=-186.685 EndY=-9e-16 EndZ=0
    g2: LineSegment StartX=-176.685 StartY=3.6 StartZ=0 EndX=-176.685 EndY=0 EndZ=0
    g3: ArcOfEllipse CenterX=-186.685 CenterY=-9e-16 CenterZ=0 NormalX=0 NormalY=0 NormalZ=1 MajorRadius=10 MinorRadius=3.6 AngleXU=1e-16 StartAngle=0 EndAngle=1.5708
    g4: LineSegment [constr] StartX=-176.685 StartY=-2e-15 StartZ=0 EndX=-196.685 EndY=-2e-15 EndZ=0
    g5: LineSegment [constr] StartX=-186.685 StartY=3.6 StartZ=0 EndX=-186.685 EndY=-3.6 EndZ=0
    g6: GeomPoint [constr] X=-177.356 Y=0 Z=0
    g7: GeomPoint [constr] X=-196.015 Y=-1.9e-15 Z=0
  constraints (13):
    c: Coincident(g0,g-4)
    c: PointOnObject(g0,g-4)
    c: DistanceX(g0,g0) = 10
    c: Coincident(g1,g0)
    c: PointOnObject(g1,g-5)
    c: Vertical(g1)
    c: Coincident(g2,g0)
    c: Coincident(g2,g-5)
    c: InternalAlignment(g4-g7 -> g3) x4
    c: Coincident(g3,g1)
    c: Coincident(g3,g0)
    c: Coincident(g3,g2)
    c: Horizontal(g4)
FEATURE [Sketcher::SketchObject] Sketch128
  ArcFitTolerance = 1e-06
  AttachmentSupport = -> [Pad016]
  ExternalGeometry = -> [Pad016]
  FullyConstrained = true
  MakeInternals = false
  MapMode = 5
  Placement = pos=(0,0,-80.4316) rot=(1,0,0;3.14159rad)
  sketch-geometry (8):
    g0: LineSegment StartX=-215.932 StartY=3.6 StartZ=0 EndX=-215.932 EndY=-1.3e-15 EndZ=0
    g1: LineSegment StartX=-215.932 StartY=3.6 StartZ=0 EndX=-205.932 EndY=3.6 EndZ=0
    g2: LineSegment [constr] StartX=-205.932 StartY=3.6 StartZ=0 EndX=-205.932 EndY=-9e-16 EndZ=0
    g3: ArcOfEllipse CenterX=-205.932 CenterY=-9e-16 CenterZ=0 NormalX=0 NormalY=0 NormalZ=1 MajorRadius=10 MinorRadius=3.6 AngleXU=-3.14159 StartAngle=4.71239 EndAngle=6.28319
    g4: LineSegment [constr] StartX=-215.932 StartY=-1e-15 StartZ=0 EndX=-195.932 EndY=-1e-15 EndZ=0
    g5: LineSegment [constr] StartX=-205.932 StartY=-3.6 StartZ=0 EndX=-205.932 EndY=3.6 EndZ=0
    g6: GeomPoint [constr] X=-215.262 Y=-2e-15 Z=0
    g7: GeomPoint [constr] X=-196.602 Y=-1e-15 Z=0
  constraints (13):
    c: Coincident(g0,g-4)
    c: Coincident(g0,g-5)
    c: Coincident(g1,g0)
    c: PointOnObject(g1,g-3)
    c: DistanceX(g1,g1) = 10
    c: Coincident(g2,g1)
    c: Vertical(g2)
    c: PointOnObject(g2,g-5)
    c: InternalAlignment(g4-g7 -> g3) x4
    c: Coincident(g3,g2)
    c: Coincident(g3,g1)
    c: Coincident(g3,g0)
    c: Horizontal(g4)
FEATURE [PartDesign::SubtractivePipe] SubtractivePipe002
  AuxilleryCurvelinear = true
  AuxillerySpineTangent = false
  BaseFeature = -> Pad016
  Binormal = (0,0,0)
  Mode = 0
  Profile = -> Sketch127
  Refine = true
  Spine = -> Pad016 [Edge254]
  SpineTangent = false
  Suppressed = false
  Transformation = 0
  Transition = 0
FEATURE [PartDesign::SubtractivePipe] SubtractivePipe003
  AuxilleryCurvelinear = true
  AuxillerySpineTangent = false
  BaseFeature = -> SubtractivePipe002
  Binormal = (0,0,0)
  Mode = 0
  Profile = -> Sketch128
  Refine = true
  Spine = -> Pad016 [Edge256,Edge251,Edge252]
  SpineTangent = false
  Suppressed = false
  Transformation = 0
  Transition = 0
FEATURE [Sketcher::SketchObject] Sketch129
  ArcFitTolerance = 1e-06
  AttachmentSupport = -> [Pad016]
  ExternalGeometry = -> [Binder001]
  FullyConstrained = true
  MakeInternals = false
  MapMode = 5
  Placement = pos=(0,-3.6,0) rot=(1,0,0;1.5708rad)
  sketch-geometry (12):
    g0: LineSegment [constr] StartX=-192.176 StartY=-3.18451 StartZ=0 EndX=-181.223 EndY=20.303 EndZ=0
    g1: LineSegment [constr] StartX=-202.765 StartY=20.303 StartZ=0 EndX=-181.223 EndY=20.303 EndZ=0
    g2: LineSegment StartX=-202.765 StartY=20.303 StartZ=0 EndX=-181.223 EndY=20.303 EndZ=0
    g3: LineSegment StartX=-192.176 StartY=-3.18451 StartZ=0 EndX=-196.804 EndY=-13.1107 EndZ=0
    g4: ArcOfCircle CenterX=-207.583 CenterY=4 CenterZ=0 NormalX=0 NormalY=0 NormalZ=1 AngleXU=0 Radius=17 StartAngle=5.84685 EndAngle=7.56663
    g5: ArcOfEllipse CenterX=-181.223 CenterY=8.55923 CenterZ=0 NormalX=0 NormalY=0 NormalZ=1 MajorRadius=23.4779 MinorRadius=11.7437 AngleXU=2e-16 StartAngle=4.71239 EndAngle=7.85398
    g6: LineSegment [constr] StartX=-157.745 StartY=8.55923 StartZ=0 EndX=-204.701 EndY=8.55923 EndZ=0
    g7: LineSegment [constr] StartX=-181.223 StartY=20.303 StartZ=0 EndX=-181.223 EndY=-3.18451 EndZ=0
    g8: GeomPoint [constr] X=-160.894 Y=8.55923 Z=0
    g9: GeomPoint [constr] X=-201.553 Y=8.55923 Z=0
    g10: ArcOfCircle CenterX=-181.223 CenterY=-20.3763 CenterZ=0 NormalX=0 NormalY=0 NormalZ=1 AngleXU=0 Radius=17.1918 StartAngle=1.57079 EndAngle=2.70526
    g11: GeomPoint [constr] X=-181.223 Y=-3.18451 Z=0
  constraints (23):
    c: Coincident(g0,g-5)
    c: Coincident(g1,g-6)
    c: Horizontal(g1)
    c: Coincident(g1,g0)
    c: Parallel(g0,g-4)
    c: Coincident(g2,g1)
    c: Coincident(g2,g0)
    c: Coincident(g3,g0)
    c: Equal(g4,g-5)
    c: Coincident(g4,g1)
    c: Coincident(g4,g0)
    c: InternalAlignment(g6-g9 -> g5) x4
    c: Vertical(g5,g0)
    c: Horizontal(g6)
    c: Coincident(g5,g0)
    c: DistanceX(g6,g-3) = 10.1
    c: Tangent(g10,g3) = -1.5708
    c: PointOnObject(g11,g10)
    c: Tangent(g5,g10,g11) = 1.5708
    c: Coincident(g10,g5)
    c: Coincident(g11,g7)
    c: Parallel(g3,g-4)
    c: Horizontal(g5,g0)
FEATURE [Sketcher::SketchObject] Sketch130
  ArcFitTolerance = 1e-06
  AttachmentOffset = pos=(0,0,-1.6) rot=(0,0,1;0rad)
  AttachmentSupport = -> [Pad016]
  ExternalGeometry = -> [Binder001]
  FullyConstrained = true
  MakeInternals = false
  MapMode = 5
  Placement = pos=(0,-2,-4e-16) rot=(1,0,0;1.5708rad)
  sketch-geometry (12):
    g0: LineSegment [constr] StartX=-192.176 StartY=-3.18451 StartZ=0 EndX=-181.223 EndY=20.303 EndZ=0
    g1: LineSegment [constr] StartX=-202.765 StartY=20.303 StartZ=0 EndX=-181.223 EndY=20.303 EndZ=0
    g2: LineSegment StartX=-202.765 StartY=20.303 StartZ=0 EndX=-181.223 EndY=20.303 EndZ=0
    g3: LineSegment StartX=-192.176 StartY=-3.18451 StartZ=0 EndX=-193.827 EndY=-6.72678 EndZ=0
    g4: ArcOfCircle CenterX=-207.583 CenterY=4 CenterZ=0 NormalX=0 NormalY=0 NormalZ=1 AngleXU=0 Radius=17 StartAngle=5.84685 EndAngle=7.56663
    g5: ArcOfEllipse CenterX=-181.223 CenterY=10.803 CenterZ=0 NormalX=0 NormalY=0 NormalZ=1 MajorRadius=14.4779 MinorRadius=9.5 AngleXU=0 StartAngle=4.71239 EndAngle=7.85398
    g6: LineSegment [constr] StartX=-166.745 StartY=10.803 StartZ=0 EndX=-195.701 EndY=10.803 EndZ=0
    g7: LineSegment [constr] StartX=-181.223 StartY=20.303 StartZ=0 EndX=-181.223 EndY=1.30297 EndZ=0
    g8: GeomPoint [constr] X=-170.298 Y=10.803 Z=0
    g9: GeomPoint [constr] X=-192.148 Y=10.803 Z=0
    g10: ArcOfCircle CenterX=-181.223 CenterY=-12.6042 CenterZ=0 NormalX=0 NormalY=0 NormalZ=1 AngleXU=0 Radius=13.9072 StartAngle=1.5708 EndAngle=2.70526
    g11: GeomPoint [constr] X=-181.223 Y=1.30297 Z=0
  constraints (23):
    c: Coincident(g0,g-5)
    c: Coincident(g1,g-6)
    c: Horizontal(g1)
    c: Coincident(g1,g0)
    c: Parallel(g0,g-4)
    c: Coincident(g2,g1)
    c: Coincident(g2,g0)
    c: Coincident(g3,g0)
    c: Equal(g4,g-5)
    c: Coincident(g4,g1)
    c: Coincident(g4,g0)
    c: InternalAlignment(g6-g9 -> g5) x4
    c: Vertical(g5,g0)
    c: Horizontal(g6)
    c: Coincident(g5,g0)
    c: DistanceX(g6,g-3) = 19.1
    c: Tangent(g10,g3) = -1.5708
    c: PointOnObject(g11,g10)
    c: Tangent(g5,g10,g11) = 1.5708
    c: Coincident(g10,g5)
    c: Coincident(g11,g7)
    c: Parallel(g3,g-4)
    c: DistanceY(g5,g0) = 19
FEATURE [Part::Part2DObjectPython] Clone2D001  label="Sketch130 (2D)"  # Draft 2D object (typed FeaturePython)
  Fuse = false
  Objects = -> [Sketch130]
  Placement = pos=(0,-2,-4e-16) rot=(1,0,0;1.5708rad)
  Scale = (1,1,1)
FEATURE [Sketcher::SketchObject] Sketch131
  ArcFitTolerance = 1e-06
  AttachmentOffset = pos=(0,0,-3.5) rot=(0,0,1;0rad)
  AttachmentSupport = -> [Pad016]
  ExternalGeometry = -> [Binder001]
  FullyConstrained = true
  MakeInternals = false
  MapMode = 5
  Placement = pos=(0,-0.1,-8e-16) rot=(1,0,0;1.5708rad)
  sketch-geometry (1):
    g0: GeomPoint X=-197.47 Y=8.55923 Z=0
  constraints (1):
    c: Symmetric(g-6,g-4,g0)
FEATURE [PartDesign::SubtractiveLoft] SubtractiveLoft002
  BaseFeature = -> SubtractivePipe003
  Closed = false
  Profile = -> Sketch129
  Refine = true
  Ruled = false
  Sections = -> [Sketch130]
  Suppressed = false
FEATURE [PartDesign::SubtractiveLoft] SubtractiveLoft003
  BaseFeature = -> SubtractiveLoft002
  Closed = false
  Profile = -> Clone2D001
  Refine = true
  Ruled = false
  Sections = -> [Sketch131]
  Suppressed = false
FEATURE [PartDesign::Chamfer] Chamfer010
  Angle = 45
  Base = -> SubtractiveLoft003 [Edge200,Edge201,Edge203,Edge202,Edge194]
  BaseFeature = -> SubtractiveLoft003
  ChamferType = 0
  FlipDirection = false
  Refine = true
  Size = 1.5
  Size2 = 1
  SupportTransform = false
  Suppressed = false
  UseAllEdges = false
FEATURE [PartDesign::Chamfer] Chamfer011
  Angle = 45
  Base = -> Chamfer010 [Edge15]
  BaseFeature = -> Chamfer010
  ChamferType = 0
  FlipDirection = false
  Refine = true
  Size = 1.6
  Size2 = 1
  SupportTransform = false
  Suppressed = false
  UseAllEdges = false
FEATURE [PartDesign::Chamfer] Chamfer012
  Angle = 45
  Base = -> Chamfer011 [Edge10]
  BaseFeature = -> Chamfer011
  ChamferType = 0
  FlipDirection = false
  Refine = true
  Size = 3.5
  Size2 = 1
  SupportTransform = false
  Suppressed = false
  UseAllEdges = false
FEATURE [PartDesign::Chamfer] Chamfer013
  Angle = 45
  Base = -> Chamfer012 [Edge145,Edge94]
  BaseFeature = -> Chamfer012
  ChamferType = 0
  FlipDirection = false
  Refine = true
  Size = 1.9
  Size2 = 1
  SupportTransform = false
  Suppressed = false
  UseAllEdges = false
FEATURE [Sketcher::SketchObject] Sketch132
  ArcFitTolerance = 1e-06
  AttachmentSupport = -> [Pad016]
  ExternalGeometry = -> [Binder001]
  FullyConstrained = true
  MakeInternals = false
  MapMode = 5
  Placement = pos=(0,-3.6,0) rot=(1,0,0;1.5708rad)
  sketch-geometry (3):
    g0: LineSegment [constr] StartX=-215.42 StartY=-53.0314 StartZ=0 EndX=-167.782 EndY=-53.0314 EndZ=0
    g1: Circle CenterX=-191.282 CenterY=-53.0314 CenterZ=0 NormalX=0 NormalY=0 NormalZ=1 AngleXU=0 Radius=11.5
    g2: Circle CenterX=-191.282 CenterY=-53.0314 CenterZ=0 NormalX=0 NormalY=0 NormalZ=1 AngleXU=0 Radius=10.7
  constraints (8):
    c: Coincident(g0,g-3)
    c: PointOnObject(g0,g-4)
    c: Horizontal(g0)
    c: Diameter(g1) = 23
    c: PointOnObject(g1,g0)
    c: DistanceX(g1,g0) = 23.5
    c: Diameter(g2) = 21.4
    c: Coincident(g2,g1)
FEATURE [PartDesign::Fillet] Fillet007
  Base = -> Chamfer013 [Edge83]
  BaseFeature = -> Chamfer013
  Radius = 1.1
  Refine = true
  SupportTransform = false
  Suppressed = false
  UseAllEdges = false
FEATURE [PartDesign::Fillet] Fillet008
  Base = -> Fillet007 [Edge76]
  BaseFeature = -> Fillet007
  Radius = 1.9
  Refine = true
  SupportTransform = false
  Suppressed = false
  UseAllEdges = false
FEATURE [PartDesign::Pocket] Pocket011
  BaseFeature = -> Fillet008
  Direction = (0,1,-2e-16)
  Length = 0.8
  Length2 = 5
  Profile = -> Sketch132
  ReferenceAxis = -> Sketch132 [N_Axis]
  Refine = true
  Suppressed = false
  Type = 0
FEATURE [Part::Part2DObjectPython] ShapeString  # Draft 2D object (typed FeaturePython)
  FontFile = <path>
  Fuse = false
  Justification = 6
  JustificationReference = 0
  KeepLeftMargin = false
  MakeFace = true
  ObliqueAngle = 0
  Placement = pos=(-199,-3.6,-57.5) rot=(1,0,0;1.5708rad)
  ScaleToSize = true
  Size = 10
  String = AS
  Tracking = 0
FEATURE [PartDesign::Pocket] Pocket012
  BaseFeature = -> Pocket011
  Direction = (0,1,0)
  Length = 1
  Length2 = 5
  Profile = -> ShapeString
  ReferenceAxis = -> ShapeString [N_Axis]
  Refine = true
  Suppressed = false
  Type = 0
FEATURE [PartDesign::Body] Body007  label="lato DX"
  AllowCompound = false
  Group = -> [Binder001,Sketch114,Pad011,Chamfer014,Sketch115,Pocket006,Sketch116,Pad012,Sketch117,Pocket007,Sketch118,Pad013,Sketch119,Pocket008,Pad017,Chamfer009,Pocket009,Sketch123,Sketch120,Pad014,Pad018,Chamfer008,Pocket010,Sketch121,Pad015,Sketch122,Pad016,Sketch124,Sketch125,Sketch126,Sketch127,Sketch128,SubtractivePipe002,SubtractivePipe003,Sketch129,Sketch130,Clone2D001,Sketch131,SubtractiveLoft002,+11 more]
  Origin = -> Origin007
  Tip = -> Pocket012
FEATURE [Sketcher::SketchObject] Sketch133
  ArcFitTolerance = 1e-06
  AttachmentSupport = -> [Binder]
  ExternalGeometry = -> [Binder]
  FullyConstrained = true
  MakeInternals = false
  MapMode = 5
  Placement = pos=(0,9e-16,0) rot=(0,0.707107,0.707107;3.14159rad)
  sketch-geometry (30):
    g0: LineSegment StartX=0 StartY=39.2 StartZ=0 EndX=0 EndY=3.2 EndZ=0
    g1: LineSegment StartX=0 StartY=3.2 StartZ=0 EndX=82.8 EndY=3.2 EndZ=0
    g2: LineSegment StartX=82.8 StartY=3.2 StartZ=0 EndX=82.8 EndY=6.2 EndZ=0
    g3: LineSegment StartX=82.8 StartY=6.2 StartZ=0 EndX=91.752 EndY=6.2 EndZ=0
    g4: LineSegment StartX=0 StartY=39.2 StartZ=0 EndX=195.887 EndY=39.2 EndZ=0
    g5: LineSegment StartX=195.887 StartY=39.2 StartZ=0 EndX=202.765 EndY=20.303 EndZ=0
    g6: LineSegment StartX=192.333 StartY=24.9893 StartZ=0 EndX=196.467 EndY=26.4942 EndZ=0
    g7: LineSegment StartX=196.467 StartY=26.4942 StartZ=0 EndX=194.073 EndY=33.0721 EndZ=0
    g8: LineSegment StartX=194.073 StartY=33.0721 StartZ=0 EndX=189.939 EndY=31.5672 EndZ=0
    g9: LineSegment StartX=189.939 StartY=31.5672 StartZ=0 EndX=192.333 EndY=24.9893 EndZ=0
    g10: ArcOfCircle CenterX=107.6 CenterY=4 CenterZ=0 NormalX=0 NormalY=0 NormalZ=1 AngleXU=0 Radius=16 StartAngle=1.5708 EndAngle=3.00366
    g11: LineSegment StartX=107.6 StartY=20 StartZ=0 EndX=132.428 EndY=20 EndZ=0
    g12: ArcOfCircle [constr] CenterX=132.428 CenterY=4 CenterZ=0 NormalX=0 NormalY=0 NormalZ=1 AngleXU=0 Radius=16 StartAngle=0.314159 EndAngle=1.5708
    g13: LineSegment StartX=147.645 StartY=8.94427 StartZ=0 EndX=176.685 EndY=-80.4316 EndZ=0
    g14: LineSegment StartX=176.685 StartY=-80.4316 StartZ=0 EndX=215.932 EndY=-80.4316 EndZ=0
    g15: ArcOfCircle CenterX=207.583 CenterY=4 CenterZ=0 NormalX=0 NormalY=0 NormalZ=1 AngleXU=0 Radius=17 StartAngle=1.85815 EndAngle=3.57792
    g16: ArcOfCircle CenterX=184.801 CenterY=-67.3089 CenterZ=0 NormalX=0 NormalY=0 NormalZ=1 AngleXU=0 Radius=33.7833 StartAngle=5.88425 EndAngle=6.71952
    g17: LineSegment StartX=192.176 StartY=-3.18451 StartZ=0 EndX=215.42 EndY=-53.0314 EndZ=0
    g18: Circle CenterX=5.6 CenterY=34.8 CenterZ=0 NormalX=0 NormalY=0 NormalZ=1 AngleXU=0 Radius=1.8
    g19: Circle CenterX=5.6 CenterY=7.6 CenterZ=0 NormalX=0 NormalY=0 NormalZ=1 AngleXU=0 Radius=1.8
    g20: Circle CenterX=78.51 CenterY=34.8 CenterZ=0 NormalX=0 NormalY=0 NormalZ=1 AngleXU=0 Radius=1.8
    g21: Circle CenterX=78.51 CenterY=7.6 CenterZ=0 NormalX=0 NormalY=0 NormalZ=1 AngleXU=0 Radius=1.8
    g22: Circle CenterX=184.08 CenterY=34.8 CenterZ=0 NormalX=0 NormalY=0 NormalZ=1 AngleXU=0 Radius=1.8
    g23: Circle CenterX=179.305 CenterY=-76.8316 CenterZ=0 NormalX=0 NormalY=0 NormalZ=1 AngleXU=0 Radius=1.8
    g24: Circle CenterX=213.443 CenterY=-76.8316 CenterZ=0 NormalX=0 NormalY=0 NormalZ=1 AngleXU=0 Radius=1.8
    g25: Circle CenterX=19 CenterY=21.2 CenterZ=0 NormalX=0 NormalY=0 NormalZ=1 AngleXU=0 Radius=6.3
    g26: Circle CenterX=42 CenterY=21.2 CenterZ=0 NormalX=0 NormalY=0 NormalZ=1 AngleXU=0 Radius=6.3
    g27: Circle CenterX=65 CenterY=21.2 CenterZ=0 NormalX=0 NormalY=0 NormalZ=1 AngleXU=0 Radius=6.3
    g28: LineSegment StartX=132.428 StartY=20 StartZ=0 EndX=144.053 EndY=20 EndZ=0
    g29: LineSegment StartX=147.645 StartY=8.94427 StartZ=0 EndX=144.053 EndY=20 EndZ=0
  constraints (65):
    c: Coincident(g0,g-4)
    c: Coincident(g0,g-5)
    c: Coincident(g1,g0)
    c: Coincident(g1,g-6)
    c: Coincident(g2,g1)
    c: Coincident(g2,g-7)
    c: Coincident(g3,g2)
    c: Coincident(g3,g-8)
    c: Coincident(g4,g0)
    c: Coincident(g4,g-16)
    c: Coincident(g5,g4)
    c: Coincident(g5,g-16)
    c: Coincident(g6,g-20)
    c: Coincident(g6,g-21)
    c: Coincident(g7,g6)
    c: Coincident(g7,g-23)
    c: Coincident(g8,g7)
    c: Coincident(g8,g-22)
    c: Coincident(g9,g8)
    c: Coincident(g9,g6)
    c: Equal(g10,g-8)
    c: Coincident(g10,g3)
    c: Coincident(g10,g-9)
    c: Coincident(g11,g10)
    c: Coincident(g11,g-10)
    c: Equal(g12,g-10)
    c: Coincident(g12,g11)
    c: Coincident(g12,g-11)
    c: Coincident(g13,g12)
    c: Coincident(g13,g-12)
    c: Coincident(g14,g13)
    c: Coincident(g14,g-13)
    c: Equal(g15,g-15)
    c: Coincident(g15,g5)
    c: Coincident(g15,g-15)
    c: Equal(g16,g-13)
    c: Coincident(g16,g14)
    c: Coincident(g16,g-14)
    c: Coincident(g17,g15)
    c: Coincident(g17,g16)
    c: Equal(g18,g-28)
    c: Equal(g19,g-29)
    c: Equal(g20,g-26)
    c: Equal(g21,g-27)
    c: Equal(g22,g-17)
    c: Equal(g24,g-25)
    c: Equal(g23,g-24)
    c: Coincident(g23,g-24)
    c: Coincident(g24,g-25)
    c: Coincident(g22,g-17)
    c: Coincident(g20,g-26)
    c: Coincident(g21,g-27)
    c: Coincident(g18,g-28)
    c: Coincident(g19,g-29)
    c: Equal(g25,g-30)
    c: Equal(g26,g-31)
    c: Equal(g27,g-32)
    c: Coincident(g25,g-30)
    c: Coincident(g26,g-31)
    c: Coincident(g27,g-32)
    c: Parallel(g28,g11)
    c: Parallel(g29,g13)
    c: Coincident(g28,g11)
    c: Coincident(g29,g12)
    c: Coincident(g29,g28)
FEATURE [PartDesign::Pad] Pad019
  Direction = (0,1,-2e-16)
  Length = 2
  Length2 = 10
  Profile = -> Sketch133
  ReferenceAxis = -> Sketch133 [N_Axis]
  Refine = true
  Suppressed = false
  Type = 0
FEATURE [Sketcher::SketchObject] Sketch091  label="Sketch091 - forma anteriore"
  ArcFitTolerance = 1e-06
  AttachmentSupport = -> [Pad019]
  ExternalGeometry = -> [Binder]
  FullyConstrained = true
  MakeInternals = false
  MapMode = 5
  Placement = pos=(0,2,0) rot=(0,0.707107,0.707107;3.14159rad)
  sketch-geometry (12):
    g0: Circle CenterX=5.6 CenterY=34.8 CenterZ=0 NormalX=0 NormalY=0 NormalZ=1 AngleXU=0 Radius=1.8
    g1: Circle CenterX=5.6 CenterY=7.6 CenterZ=0 NormalX=0 NormalY=0 NormalZ=1 AngleXU=0 Radius=1.8
    g2: Circle CenterX=78.51 CenterY=34.8 CenterZ=0 NormalX=0 NormalY=0 NormalZ=1 AngleXU=0 Radius=1.8
    g3: Circle CenterX=78.51 CenterY=7.6 CenterZ=0 NormalX=0 NormalY=0 NormalZ=1 AngleXU=0 Radius=1.8
    g4: LineSegment StartX=0 StartY=39.2 StartZ=0 EndX=0 EndY=3.2 EndZ=0
    g5: LineSegment StartX=0 StartY=3.2 StartZ=0 EndX=82.8 EndY=3.2 EndZ=0
    g6: LineSegment StartX=82.8 StartY=3.2 StartZ=0 EndX=82.8 EndY=39.2 EndZ=0
    g7: LineSegment StartX=82.8 StartY=39.2 StartZ=0 EndX=0 EndY=39.2 EndZ=0
    g8: ArcOfCircle CenterX=19 CenterY=21.2 CenterZ=0 NormalX=0 NormalY=0 NormalZ=1 AngleXU=0 Radius=10 StartAngle=1.5708 EndAngle=4.71239
    g9: ArcOfCircle CenterX=65 CenterY=21.2 CenterZ=0 NormalX=0 NormalY=0 NormalZ=1 AngleXU=0 Radius=10 StartAngle=4.71239 EndAngle=7.85398
    g10: LineSegment StartX=19 StartY=31.2 StartZ=0 EndX=65 EndY=31.2 EndZ=0
    g11: LineSegment StartX=19 StartY=11.2 StartZ=0 EndX=65 EndY=11.2 EndZ=0
  constraints (25):
    c: Equal(g2,g-7)
    c: Equal(g3,g-8)
    c: Equal(g1,g-13)
    c: Equal(g0,g-12)
    c: Coincident(g0,g-12)
    c: Coincident(g1,g-13)
    c: Coincident(g3,g-8)
    c: Coincident(g2,g-7)
    c: Coincident(g4,g-4)
    c: Coincident(g4,g-5)
    c: Coincident(g5,g4)
    c: Coincident(g5,g-6)
    c: Coincident(g6,g5)
    c: PointOnObject(g6,g-3)
    c: Vertical(g6)
    c: Coincident(g7,g6)
    c: Coincident(g7,g4)
    c: Tangent(g8,g10) = 1.5708
    c: Tangent(g8,g11) = -1.5708
    c: Tangent(g9,g10) = 1.5708
    c: Tangent(g9,g11) = -1.5708
    c: Equal(g8,g9)
    c: Radius(g8) = 10
    c: Coincident(g8,g-11)
    c: Coincident(g9,g-9)
FEATURE [Sketcher::SketchObject] Sketch093  label="Sketch093 - scavi interni pulsanti"
  ArcFitTolerance = 1e-06
  AttachmentSupport = -> [Pad019]
  ExternalGeometry = -> [Binder]
  FullyConstrained = true
  MakeInternals = false
  MapMode = 5
  Placement = pos=(0,1.8e-15,0) rot=(1,0,0;1.5708rad)
  sketch-geometry (3):
    g0: Circle CenterX=-65 CenterY=21.2 CenterZ=0 NormalX=0 NormalY=0 NormalZ=1 AngleXU=0 Radius=7.3
    g1: Circle CenterX=-42 CenterY=21.2 CenterZ=0 NormalX=0 NormalY=0 NormalZ=1 AngleXU=0 Radius=7.3
    g2: Circle CenterX=-19 CenterY=21.2 CenterZ=0 NormalX=0 NormalY=0 NormalZ=1 AngleXU=0 Radius=7.3
  constraints (6):
    c: Coincident(g0,g-3)
    c: Coincident(g1,g-4)
    c: Coincident(g2,g-5)
    c: Diameter(g0) = 14.6
    c: Diameter(g1) = 14.6
    c: Diameter(g2) = 14.6
FEATURE [Sketcher::SketchObject] Sketch094  label="Sketch094 - forma centrale"
  ArcFitTolerance = 1e-06
  AttachmentSupport = -> [Pad019]
  ExternalGeometry = -> [Binder]
  FullyConstrained = true
  MakeInternals = false
  MapMode = 5
  Placement = pos=(0,2,0) rot=(0,0.707107,0.707107;3.14159rad)
  sketch-geometry (4):
    g0: LineSegment StartX=137.815 StartY=39.2 StartZ=0 EndX=142.655 EndY=24.303 EndZ=0
    g1: LineSegment StartX=110.815 StartY=24.303 StartZ=0 EndX=142.655 EndY=24.303 EndZ=0
    g2: LineSegment StartX=137.815 StartY=39.2 StartZ=0 EndX=110.815 EndY=39.2 EndZ=0
    g3: ArcOfCircle CenterX=92.2534 CenterY=31.7515 CenterZ=0 NormalX=0 NormalY=0 NormalZ=1 AngleXU=0 Radius=20 StartAngle=5.90156 EndAngle=6.66481
  constraints (12):
    c: PointOnObject(g0,g-3)
    c: Tangent(g0,g-5)
    c: Horizontal(g1)
    c: Coincident(g1,g0)
    c: Coincident(g2,g0)
    c: PointOnObject(g2,g-3)
    c: DistanceX(g2,g2) = 27
    c: Vertical(g1,g2)
    c: Coincident(g3,g2)
    c: Radius(g3) = 20
    c: Coincident(g3,g1)
    c: DistanceY(g-6,g0) = 4
FEATURE [Sketcher::SketchObject] Sketch095  label="Sketch095 - forma posteriore"
  ArcFitTolerance = 1e-06
  AttachmentSupport = -> [Pad019]
  ExternalGeometry = -> [Binder]
  FullyConstrained = true
  MakeInternals = false
  MapMode = 5
  Placement = pos=(0,2,0) rot=(0,0.707107,0.707107;3.14159rad)
  sketch-geometry (15):
    g0: LineSegment StartX=137.815 StartY=39.2 StartZ=0 EndX=143.955 EndY=20.303 EndZ=0
    g1: LineSegment StartX=143.955 StartY=20.303 StartZ=0 EndX=190.141 EndY=20.303 EndZ=0
    g2: ArcOfCircle CenterX=184.08 CenterY=34.8 CenterZ=0 NormalX=0 NormalY=0 NormalZ=1 AngleXU=0 Radius=3.5 StartAngle=3.49066 EndAngle=4.71239
    g3: LineSegment StartX=180.791 StartY=33.6029 StartZ=0 EndX=178.754 EndY=39.2 EndZ=0
    g4: LineSegment StartX=184.08 StartY=31.3 StartZ=0 EndX=186.139 EndY=31.3 EndZ=0
    g5: LineSegment StartX=190.141 StartY=20.303 StartZ=0 EndX=186.139 EndY=31.3 EndZ=0
    g6: LineSegment StartX=137.815 StartY=39.2 StartZ=0 EndX=156.815 EndY=39.2 EndZ=0
    g7: LineSegment StartX=178.754 StartY=39.2 StartZ=0 EndX=168.815 EndY=39.2 EndZ=0
    g8: LineSegment StartX=156.815 StartY=31.2 StartZ=0 EndX=168.815 EndY=31.2 EndZ=0
    g9: ArcOfCircle CenterX=176.411 CenterY=35.2 CenterZ=0 NormalX=0 NormalY=0 NormalZ=1 AngleXU=0 Radius=20 StartAngle=2.94023 EndAngle=3.34295
    g10: ArcOfCircle CenterX=188.411 CenterY=35.2 CenterZ=0 NormalX=0 NormalY=0 NormalZ=1 AngleXU=0 Radius=20 StartAngle=2.94023 EndAngle=3.34295
    g11: LineSegment StartX=157.815 StartY=39.2 StartZ=0 EndX=167.815 EndY=39.2 EndZ=0
    g12: LineSegment StartX=157.436 StartY=36.2 StartZ=0 EndX=167.436 EndY=36.2 EndZ=0
    g13: ArcOfCircle CenterX=177.411 CenterY=35.2 CenterZ=0 NormalX=0 NormalY=0 NormalZ=1 AngleXU=0 Radius=20 StartAngle=2.94023 EndAngle=3.09157
    g14: ArcOfCircle CenterX=187.411 CenterY=35.2 CenterZ=0 NormalX=0 NormalY=0 NormalZ=1 AngleXU=0 Radius=20 StartAngle=2.94023 EndAngle=3.09157
  constraints (46):
    c: PointOnObject(g0,g-3)
    c: Tangent(g0,g-6)
    c: Coincident(g1,g0)
    c: Horizontal(g1)
    c: Radius(g2) = 3.5
    c: Coincident(g2,g-5)
    c: PointOnObject(g3,g-3)
    c: Parallel(g3,g-4)
    c: Tangent(g3,g2) = 1.5708
    c: Horizontal(g4)
    c: Tangent(g4,g2) = -1.5708
    c: Coincident(g5,g1)
    c: Parallel(g5,g-4)
    c: Coincident(g5,g4)
    c: DistanceX(g4,g-8) = 3.8
    c: Coincident(g6,g0)
    c: PointOnObject(g6,g-3)
    c: Coincident(g7,g3)
    c: PointOnObject(g7,g-3)
    c: Horizontal(g8)
    c: DistanceX(g6,g7) = 12
    c: Vertical(g8,g6)
    c: Vertical(g7,g8)
    c: DistanceY(g8,g6) = 8
    c: Coincident(g9,g8)
    c: Coincident(g9,g6)
    c: Coincident(g10,g7)
    c: Coincident(g10,g8)
    c: Radius(g9) = 20
    c: Radius(g10) = 20
    c: PointOnObject(g11,g-3)
    c: PointOnObject(g11,g-3)
    c: DistanceX(g11,g11) = 10
    c: DistanceX(g6,g11) = 1
    c: Horizontal(g12)
    c: Equal(g12,g11)
    c: DistanceY(g12,g11) = 3
    c: Coincident(g13,g11)
    c: Coincident(g13,g12)
    c: Radius(g13) = 20
    c: Coincident(g14,g11)
    c: Coincident(g14,g12)
    c: Radius(g14) = 20
    c: DistanceX(g0,g6) = 19
    c: Horizontal(g9,g13)
    c: Horizontal(g0,g-4)
FEATURE [Sketcher::SketchObject] Sketch096  label="Sketch096 - forma impugnatura"
  ArcFitTolerance = 1e-06
  AttachmentSupport = -> [Pad019]
  ExternalGeometry = -> [Binder]
  FullyConstrained = true
  MakeInternals = false
  MapMode = 5
  Placement = pos=(0,2,0) rot=(0,0.707107,0.707107;3.14159rad)
  sketch-geometry (8):
    g0: LineSegment StartX=176.685 StartY=-80.4316 StartZ=0 EndX=143.955 EndY=20.303 EndZ=0
    g1: LineSegment StartX=176.685 StartY=-80.4316 StartZ=0 EndX=215.932 EndY=-80.4316 EndZ=0
    g2: Circle CenterX=179.305 CenterY=-76.8316 CenterZ=0 NormalX=0 NormalY=0 NormalZ=1 AngleXU=0 Radius=3
    g3: Circle CenterX=213.443 CenterY=-76.8316 CenterZ=0 NormalX=0 NormalY=0 NormalZ=1 AngleXU=0 Radius=3
    g4: LineSegment StartX=143.955 StartY=20.303 StartZ=0 EndX=202.765 EndY=20.303 EndZ=0
    g5: LineSegment StartX=215.42 StartY=-53.0314 StartZ=0 EndX=192.176 EndY=-3.18451 EndZ=0
    g6: ArcOfCircle CenterX=184.801 CenterY=-67.3089 CenterZ=0 NormalX=0 NormalY=0 NormalZ=1 AngleXU=0 Radius=33.7833 StartAngle=5.88425 EndAngle=6.71952
    g7: ArcOfCircle CenterX=207.583 CenterY=4 CenterZ=0 NormalX=0 NormalY=0 NormalZ=1 AngleXU=0 Radius=17 StartAngle=1.85815 EndAngle=3.57792
  constraints (19):
    c: Coincident(g0,g-4)
    c: PointOnObject(g0,g-3)
    c: Horizontal(g0,g-7)
    c: Coincident(g1,g0)
    c: Coincident(g1,g-5)
    c: Diameter(g2) = 6
    c: Diameter(g3) = 6
    c: Coincident(g2,g-9)
    c: Coincident(g3,g-10)
    c: Coincident(g4,g0)
    c: Coincident(g5,g-6)
    c: Coincident(g6,g1)
    c: Coincident(g6,g5)
    c: Equal(g-5,g6)
    c: Coincident(g5,g-7)
    c: Coincident(g4,g-7)
    c: Tangent(g7,g-7)
    c: Coincident(g7,g4)
    c: Coincident(g7,g5)
FEATURE [Sketcher::SketchObject] Sketch097
  ArcFitTolerance = 1e-06
  AttachmentSupport = -> [Pad019]
  ExternalGeometry = -> [Binder]
  FullyConstrained = true
  MakeInternals = false
  MapMode = 5
  Placement = pos=(0,2,0) rot=(0,0.707107,0.707107;3.14159rad)
  sketch-geometry (4):
    g0: LineSegment StartX=90 StartY=36.8 StartZ=0 EndX=108 EndY=36.8 EndZ=0
    g1: LineSegment StartX=108 StartY=36.8 StartZ=0 EndX=108 EndY=26.8 EndZ=0
    g2: LineSegment StartX=108 StartY=26.8 StartZ=0 EndX=90 EndY=26.8 EndZ=0
    g3: ArcOfCircle CenterX=94 CenterY=31.8 CenterZ=0 NormalX=0 NormalY=0 NormalZ=1 AngleXU=0 Radius=6.40312 StartAngle=2.24554 EndAngle=4.03765
  constraints (13):
    c: Horizontal(g0)
    c: Coincident(g1,g0)
    c: Vertical(g1)
    c: DistanceX(g0,g0) = 18
    c: DistanceY(g1,g1) = 10
    c: Coincident(g2,g1)
    c: Horizontal(g2)
    c: Equal(g2,g0)
    c: DistanceY(g0,g-3) = 2.4
    c: Coincident(g3,g0)
    c: Coincident(g3,g2)
    c: DistanceX(g2,g3) = 4
    c: DistanceX(g-3,g0) = 90
FEATURE [PartDesign::Chamfer] Chamfer015
  Angle = 45
  Base = -> Pad019 [Edge19,Edge22,Edge79]
  BaseFeature = -> Pad019
  ChamferType = 0
  FlipDirection = false
  Refine = true
  Size = 1.9
  Size2 = 1
  SupportTransform = false
  Suppressed = false
  UseAllEdges = false
FEATURE [PartDesign::Pocket] Pocket002
  BaseFeature = -> Chamfer015
  Direction = (0,1,-2e-16)
  Length = 1.2
  Length2 = 5
  Profile = -> Sketch093
  ReferenceAxis = -> Sketch093 [N_Axis]
  Refine = true
  Suppressed = false
  Type = 0
FEATURE [PartDesign::Pad] Pad005
  BaseFeature = -> Pocket002
  Direction = (0,1,-2e-16)
  Length = 1.6
  Length2 = 10
  Profile = -> Sketch091
  ReferenceAxis = -> Sketch091 [N_Axis]
  Refine = true
  Suppressed = false
  Type = 0
FEATURE [Sketcher::SketchObject] Sketch092  label="Sketch092 - scavi per viti anteriori"
  ArcFitTolerance = 1e-06
  AttachmentSupport = -> [Pad005]
  ExternalGeometry = -> [Binder]
  FullyConstrained = true
  MakeInternals = false
  MapMode = 5
  Placement = pos=(0,3.6,0) rot=(0,0.707107,0.707107;3.14159rad)
  sketch-geometry (20):
    g0: ArcOfCircle CenterX=5.6 CenterY=7.6 CenterZ=0 NormalX=0 NormalY=0 NormalZ=1 AngleXU=0 Radius=3.5 StartAngle=0 EndAngle=1.5708
    g1: ArcOfCircle CenterX=5.6 CenterY=34.8 CenterZ=0 NormalX=0 NormalY=0 NormalZ=1 AngleXU=0 Radius=3.5 StartAngle=4.71239 EndAngle=6.28319
    g2: ArcOfCircle CenterX=78.51 CenterY=34.8 CenterZ=0 NormalX=0 NormalY=0 NormalZ=1 AngleXU=0 Radius=3.5 StartAngle=3.14159 EndAngle=4.71239
    g3: ArcOfCircle CenterX=78.51 CenterY=7.6 CenterZ=0 NormalX=0 NormalY=0 NormalZ=1 AngleXU=0 Radius=3.5 StartAngle=1.5708 EndAngle=3.14159
    g4: LineSegment StartX=0 StartY=3.2 StartZ=0 EndX=0 EndY=11.1 EndZ=0
    g5: LineSegment StartX=0 StartY=11.1 StartZ=0 EndX=5.6 EndY=11.1 EndZ=0
    g6: LineSegment StartX=0 StartY=3.2 StartZ=0 EndX=9.1 EndY=3.2 EndZ=0
    g7: LineSegment StartX=9.1 StartY=3.2 StartZ=0 EndX=9.1 EndY=7.6 EndZ=0
    g8: LineSegment StartX=0 StartY=39.2 StartZ=0 EndX=0 EndY=31.3 EndZ=0
    g9: LineSegment StartX=0 StartY=31.3 StartZ=0 EndX=5.6 EndY=31.3 EndZ=0
    g10: LineSegment StartX=0 StartY=39.2 StartZ=0 EndX=9.1 EndY=39.2 EndZ=0
    g11: LineSegment StartX=9.1 StartY=39.2 StartZ=0 EndX=9.1 EndY=34.8 EndZ=0
    g12: LineSegment StartX=82.8 StartY=39.2 StartZ=0 EndX=75.01 EndY=39.2 EndZ=0
    g13: LineSegment StartX=82.8 StartY=39.2 StartZ=0 EndX=82.8 EndY=31.3 EndZ=0
    g14: LineSegment StartX=82.8 StartY=31.3 StartZ=0 EndX=78.51 EndY=31.3 EndZ=0
    g15: LineSegment StartX=82.8 StartY=3.2 StartZ=0 EndX=75.01 EndY=3.2 EndZ=0
    g16: LineSegment StartX=75.01 StartY=3.2 StartZ=0 EndX=75.01 EndY=7.6 EndZ=0
    g17: LineSegment StartX=82.8 StartY=3.2 StartZ=0 EndX=82.8 EndY=11.1 EndZ=0
    g18: LineSegment StartX=82.8 StartY=11.1 StartZ=0 EndX=78.51 EndY=11.1 EndZ=0
    g19: LineSegment StartX=75.01 StartY=39.2 StartZ=0 EndX=75.01 EndY=34.8 EndZ=0
  constraints (48):
    c: Radius(g0) = 3.5
    c: Coincident(g0,g-10)
    c: Radius(g1) = 3.5
    c: Coincident(g1,g-9)
    c: Radius(g2) = 3.5
    c: Coincident(g2,g-8)
    c: Radius(g3) = 3.5
    c: Coincident(g3,g-7)
    c: Coincident(g4,g-5)
    c: PointOnObject(g4,g-4)
    c: Coincident(g5,g4)
    c: Horizontal(g5)
    c: Coincident(g6,g4)
    c: PointOnObject(g6,g-5)
    c: Coincident(g7,g6)
    c: Vertical(g7)
    c: Coincident(g8,g-4)
    c: PointOnObject(g8,g-4)
    c: Coincident(g9,g8)
    c: Horizontal(g9)
    c: Coincident(g10,g8)
    c: PointOnObject(g10,g-3)
    c: Coincident(g11,g10)
    c: Vertical(g11)
    c: PointOnObject(g12,g-3)
    c: PointOnObject(g12,g-3)
    c: Coincident(g13,g12)
    c: Vertical(g13)
    c: Coincident(g14,g13)
    c: Horizontal(g14)
    c: Coincident(g15,g-6)
    c: PointOnObject(g15,g-5)
    c: Coincident(g16,g15)
    c: Vertical(g16)
    c: Coincident(g17,g15)
    c: Coincident(g18,g17)
    c: Horizontal(g18)
    c: Tangent(g3,g18) = -1.5708
    c: Tangent(g16,g3) = 1.5708
    c: Coincident(g19,g12)
    c: Vertical(g19)
    c: Tangent(g2,g19) = -1.5708
    c: Tangent(g2,g14) = 1.5708
    c: Tangent(g0,g7) = -1.5708
    c: Tangent(g0,g5) = 1.5708
    c: Tangent(g9,g1) = -1.5708
    c: Tangent(g1,g11) = 1.5708
    c: Tangent(g17,g13)
FEATURE [PartDesign::Pocket] Pocket001
  BaseFeature = -> Pad005
  Direction = (0,-1,2e-16)
  Length = 1.6
  Length2 = 5
  Profile = -> Sketch092
  ReferenceAxis = -> Sketch092 [N_Axis]
  Refine = true
  Suppressed = false
  Type = 0
FEATURE [PartDesign::Pad] Pad006
  BaseFeature = -> Pocket001
  Direction = (0,1,-2e-16)
  Length = 0.8
  Length2 = 10
  Profile = -> Sketch094
  ReferenceAxis = -> Sketch094 [N_Axis]
  Refine = true
  Suppressed = false
  Type = 0
FEATURE [PartDesign::Pad] Pad007
  BaseFeature = -> Pad006
  Direction = (0,1,-2e-16)
  Length = 2
  Length2 = 10
  Profile = -> Sketch095
  ReferenceAxis = -> Sketch095 [N_Axis]
  Refine = true
  Suppressed = false
  Type = 0
FEATURE [PartDesign::Pad] Pad008  label="Pad008 - forma impugnatura"
  BaseFeature = -> Pad007
  Direction = (0,1,-2e-16)
  Length = 1.6
  Length2 = 10
  Profile = -> Sketch096
  ReferenceAxis = -> Sketch096 [N_Axis]
  Refine = true
  Suppressed = false
  Type = 0
FEATURE [PartDesign::Pad] Pad009
  BaseFeature = -> Pad008
  Direction = (0,1,-2e-16)
  Length = 1.6
  Length2 = 10
  Profile = -> Sketch097
  ReferenceAxis = -> Sketch097 [N_Axis]
  Refine = true
  Suppressed = false
  Type = 0
FEATURE [Sketcher::SketchObject] Sketch098
  ArcFitTolerance = 1e-06
  AttachmentSupport = -> [Pad006]
  ExternalGeometry = -> [Binder]
  FullyConstrained = true
  MakeInternals = false
  MapMode = 5
  Placement = pos=(0,2.8,-7e-16) rot=(0,0.707107,0.707107;3.14159rad)
  sketch-geometry (4):
    g0: LineSegment StartX=118 StartY=39.2 StartZ=0 EndX=129 EndY=39.2 EndZ=0
    g1: LineSegment StartX=120.599 StartY=31.2 StartZ=0 EndX=131.599 EndY=31.2 EndZ=0
    g2: LineSegment StartX=129 StartY=39.2 StartZ=0 EndX=131.599 EndY=31.2 EndZ=0
    g3: LineSegment StartX=118 StartY=39.2 StartZ=0 EndX=120.599 EndY=31.2 EndZ=0
  constraints (12):
    c: PointOnObject(g0,g-3)
    c: PointOnObject(g0,g-3)
    c: DistanceX(g0,g0) = 11
    c: Horizontal(g1)
    c: Equal(g1,g0)
    c: Coincident(g2,g0)
    c: Coincident(g3,g0)
    c: Parallel(g-4,g2)
    c: Coincident(g1,g2)
    c: Coincident(g1,g3)
    c: DistanceY(g1,g0) = 8
    c: DistanceX(g-3,g0) = 118
FEATURE [Sketcher::SketchObject] Sketch099
  ArcFitTolerance = 1e-06
  AttachmentSupport = -> [Pad008]
  ExternalGeometry = -> [Binder]
  FullyConstrained = true
  MakeInternals = false
  MapMode = 5
  Placement = pos=(0,3.6,0) rot=(0,0.707107,0.707107;3.14159rad)
  sketch-geometry (13):
    g0: LineSegment StartX=192.176 StartY=-3.18451 StartZ=0 EndX=196.804 EndY=-13.1108 EndZ=0
    g1: LineSegment [constr] StartX=202.765 StartY=20.303 StartZ=0 EndX=181.223 EndY=20.303 EndZ=0
    g2: LineSegment [constr] StartX=181.223 StartY=20.303 StartZ=0 EndX=181.223 EndY=-3.18451 EndZ=0
    g3: ArcOfCircle CenterX=181.223 CenterY=-20.3764 CenterZ=0 NormalX=0 NormalY=0 NormalZ=1 AngleXU=0 Radius=17.1918 StartAngle=0.436332 EndAngle=1.57079
    g4: ArcOfEllipse CenterX=181.223 CenterY=8.55923 CenterZ=0 NormalX=0 NormalY=0 NormalZ=1 MajorRadius=23.4779 MinorRadius=11.7437 AngleXU=0 StartAngle=1.5708 EndAngle=4.71239
    g5: LineSegment [constr] StartX=204.701 StartY=8.55923 StartZ=0 EndX=157.745 EndY=8.55923 EndZ=0
    g6: LineSegment [constr] StartX=181.223 StartY=20.303 StartZ=0 EndX=181.223 EndY=-3.18451 EndZ=0
    g7: GeomPoint [constr] X=201.553 Y=8.55923 Z=0
    g8: GeomPoint [constr] X=160.894 Y=8.55923 Z=0
    g9: GeomPoint [constr] X=181.223 Y=-3.18451 Z=0
    g10: LineSegment StartX=181.223 StartY=20.303 StartZ=0 EndX=202.765 EndY=20.303 EndZ=0
    g11: ArcOfCircle CenterX=207.583 CenterY=4 CenterZ=0 NormalX=0 NormalY=0 NormalZ=1 AngleXU=0 Radius=17 StartAngle=1.85815 EndAngle=3.57792
    g12: LineSegment [constr] StartX=172.411 StartY=39.2 StartZ=0 EndX=192.176 EndY=-3.18451 EndZ=0
  constraints (27):
    c: Coincident(g1,g-7)
    c: Horizontal(g1)
    c: Coincident(g2,g1)
    c: Vertical(g2)
    c: Horizontal(g2,g0)
    c: Coincident(g3,g0)
    c: Coincident(g3,g2)
    c: InternalAlignment(g5-g8 -> g4) x4
    c: Horizontal(g5)
    c: PointOnObject(g4,g2)
    c: Coincident(g4,g1)
    c: DistanceX(g-3,g5) = 10.1
    c: Coincident(g4,g2)
    c: Tangent(g3,g-5)
    c: PointOnObject(g9,g4)
    c: PointOnObject(g9,g3)
    c: Tangent(g4,g3,g9) = 1.5708
    c: Coincident(g10,g1)
    c: Coincident(g10,g1)
    c: Equal(g11,g-4)
    c: Coincident(g11,g1)
    c: Coincident(g11,g0)
    c: PointOnObject(g12,g-6)
    c: PointOnObject(g1,g12)
    c: Tangent(g12,g-5) = -1.5708
    c: Tangent(g0,g-5) = -1.5708
    c: Horizontal(g9,g12)
FEATURE [Sketcher::SketchObject] Sketch106  label="Sketch106 - smusso impuniatura interno"
  ArcFitTolerance = 1e-06
  AttachmentSupport = -> [Pad008]
  ExternalGeometry = -> [Pad008]
  FullyConstrained = true
  MakeInternals = false
  MapMode = 5
  Placement = pos=(0,-1.585e-13,-80.4316) rot=(1,0,0;3.14159rad)
  sketch-geometry (9):
    g0: LineSegment StartX=-176.685 StartY=-3.6 StartZ=0 EndX=-176.685 EndY=2.12528e-11 EndZ=0
    g1: LineSegment [constr] StartX=-176.685 StartY=1.79e-14 StartZ=0 EndX=-176.685 EndY=2.12527e-11 EndZ=0
    g2: LineSegment [constr] StartX=-186.685 StartY=-3.6 StartZ=0 EndX=-186.685 EndY=2.12528e-11 EndZ=0
    g3: ArcOfEllipse CenterX=-186.685 CenterY=2.12527e-11 CenterZ=0 NormalX=0 NormalY=0 NormalZ=1 MajorRadius=10 MinorRadius=3.6 AngleXU=-3.14159 StartAngle=1.5708 EndAngle=3.14159
    g4: LineSegment [constr] StartX=-196.685 StartY=1.79e-14 StartZ=0 EndX=-176.685 EndY=1.79e-14 EndZ=0
    g5: LineSegment [constr] StartX=-186.685 StartY=-3.6 StartZ=0 EndX=-186.685 EndY=3.6 EndZ=0
    g6: GeomPoint [constr] X=-196.015 Y=1.55e-14 Z=0
    g7: GeomPoint [constr] X=-177.356 Y=1.85e-14 Z=0
    g8: LineSegment StartX=-176.685 StartY=-3.6 StartZ=0 EndX=-186.685 EndY=-3.6 EndZ=0
  constraints (15):
    c: PointOnObject(g2,g-3)
    c: Coincident(g1,g-5)
    c: DistanceY(g1,g1) = 0
    c: Coincident(g0,g1)
    c: DistanceX(g2,g-5) = 10
    c: Vertical(g2)
    c: Horizontal(g2,g0)
    c: InternalAlignment(g4-g7 -> g3) x4
    c: Coincident(g3,g2)
    c: Horizontal(g4)
    c: Coincident(g3,g0)
    c: Tangent(g0,g-5) = 1.5708
    c: Coincident(g3,g2)
    c: Coincident(g8,g0)
    c: Coincident(g8,g2)
FEATURE [Sketcher::SketchObject] Sketch107  label="Sketch107 - smusso impugnatura esterno"
  ArcFitTolerance = 1e-06
  AttachmentSupport = -> [Pad008]
  ExternalGeometry = -> [Pad008]
  FullyConstrained = true
  MakeInternals = false
  MapMode = 5
  Placement = pos=(0,-1.585e-13,-80.4316) rot=(1,0,0;3.14159rad)
  sketch-geometry (9):
    g0: LineSegment [constr] StartX=-215.932 StartY=1.79e-14 StartZ=0 EndX=-215.932 EndY=2.09e-14 EndZ=0
    g1: LineSegment StartX=-215.932 StartY=-3.6 StartZ=0 EndX=-215.932 EndY=2.09e-14 EndZ=0
    g2: LineSegment StartX=-215.932 StartY=-3.6 StartZ=0 EndX=-205.932 EndY=-3.6 EndZ=0
    g3: LineSegment [constr] StartX=-205.932 StartY=-3.6 StartZ=0 EndX=-205.932 EndY=2.09e-14 EndZ=0
    g4: ArcOfEllipse CenterX=-205.932 CenterY=2.09e-14 CenterZ=0 NormalX=0 NormalY=0 NormalZ=1 MajorRadius=10 MinorRadius=3.6 AngleXU=3.14159 StartAngle=1e-16 EndAngle=1.5708
    g5: LineSegment [constr] StartX=-215.932 StartY=1.79e-14 StartZ=0 EndX=-195.932 EndY=1.79e-14 EndZ=0
    g6: LineSegment [constr] StartX=-205.932 StartY=-3.6 StartZ=0 EndX=-205.932 EndY=3.6 EndZ=0
    g7: GeomPoint [constr] X=-215.262 Y=2.14e-14 Z=0
    g8: GeomPoint [constr] X=-196.602 Y=1.78e-14 Z=0
  constraints (16):
    c: Coincident(g0,g-6)
    c: PointOnObject(g0,g-6)
    c: DistanceY(g0,g0) = 0
    c: Coincident(g1,g-6)
    c: Coincident(g1,g0)
    c: Tangent(g2,g-3)
    c: DistanceX(g2,g2) = 10
    c: Coincident(g3,g2)
    c: Vertical(g3)
    c: Horizontal(g3,g0)
    c: InternalAlignment(g5-g8 -> g4) x4
    c: Coincident(g4,g3)
    c: Horizontal(g5)
    c: Coincident(g4,g0)
    c: Coincident(g4,g2)
    c: PointOnObject(g2,g1)
FEATURE [Sketcher::SketchObject] Sketch108
  ArcFitTolerance = 1e-06
  AttachmentOffset = pos=(0,0,-1.6) rot=(0,0,1;0rad)
  AttachmentSupport = -> [Pad008]
  ExternalGeometry = -> [Binder]
  FullyConstrained = true
  MakeInternals = false
  MapMode = 5
  Placement = pos=(0,2,4e-16) rot=(0,0.707107,0.707107;3.14159rad)
  sketch-geometry (14):
    g0: LineSegment StartX=192.176 StartY=-3.18451 StartZ=0 EndX=193.827 EndY=-6.72678 EndZ=0
    g1: LineSegment [constr] StartX=202.765 StartY=20.303 StartZ=0 EndX=181.223 EndY=20.303 EndZ=0
    g2: LineSegment [constr] StartX=181.223 StartY=20.303 StartZ=0 EndX=181.223 EndY=1.30297 EndZ=0
    g3: ArcOfCircle CenterX=181.223 CenterY=-12.6042 CenterZ=0 NormalX=0 NormalY=0 NormalZ=1 AngleXU=0 Radius=13.9072 StartAngle=0.436332 EndAngle=1.5708
    g4: ArcOfEllipse CenterX=181.223 CenterY=10.803 CenterZ=0 NormalX=0 NormalY=0 NormalZ=1 MajorRadius=14.4779 MinorRadius=9.5 AngleXU=0 StartAngle=1.5708 EndAngle=4.71239
    g5: LineSegment [constr] StartX=195.701 StartY=10.803 StartZ=0 EndX=166.745 EndY=10.803 EndZ=0
    g6: LineSegment [constr] StartX=181.223 StartY=20.303 StartZ=0 EndX=181.223 EndY=1.30297 EndZ=0
    g7: GeomPoint [constr] X=192.148 Y=10.803 Z=0
    g8: GeomPoint [constr] X=170.298 Y=10.803 Z=0
    g9: LineSegment StartX=181.223 StartY=20.303 StartZ=0 EndX=202.765 EndY=20.303 EndZ=0
    g10: ArcOfCircle CenterX=207.583 CenterY=4 CenterZ=0 NormalX=0 NormalY=0 NormalZ=1 AngleXU=0 Radius=17 StartAngle=1.85815 EndAngle=3.57792
    g11: LineSegment [constr] StartX=172.411 StartY=39.2 StartZ=0 EndX=192.176 EndY=-3.18451 EndZ=0
    g12: GeomPoint [constr] X=181.223 Y=1.30297 Z=0
    g13: GeomPoint [constr] X=181.223 Y=1.30297 Z=0
  constraints (28):
    c: Coincident(g1,g-7)
    c: Horizontal(g1)
    c: Coincident(g2,g1)
    c: Vertical(g2)
    c: Coincident(g3,g2)
    c: InternalAlignment(g5-g8 -> g4) x4
    c: Horizontal(g5)
    c: PointOnObject(g4,g2)
    c: Coincident(g4,g1)
    c: DistanceX(g-3,g5) = 19.1
    c: Coincident(g4,g2)
    c: Coincident(g9,g1)
    c: Coincident(g9,g1)
    c: Coincident(g10,g1)
    c: Coincident(g10,g0)
    c: PointOnObject(g11,g-6)
    c: PointOnObject(g1,g11)
    c: DistanceY(g2,g1) = 19
    c: Coincident(g10,g-4)
    c: PointOnObject(g12,g4)
    c: PointOnObject(g12,g3)
    c: Tangent(g11,g-5) = -1.5708
    c: Tangent(g0,g-5) = -1.5708
    c: Tangent(g3,g0) = 1.5708
    c: PointOnObject(g13,g4)
    c: PointOnObject(g13,g3)
    c: Tangent(g4,g3,g13) = 1.5708
    c: Horizontal(g11,g0)
FEATURE [Part::Part2DObjectPython] Clone2D  label="Sketch108 (2D)"  # Draft 2D object (typed FeaturePython)
  Fuse = false
  Objects = -> [Sketch108]
  Placement = pos=(0,2,4e-16) rot=(0,0.707107,0.707107;3.14159rad)
  Scale = (1,1,1)
FEATURE [Sketcher::SketchObject] Sketch109
  ArcFitTolerance = 1e-06
  AttachmentOffset = pos=(0,0,-3.5) rot=(0,0,1;0rad)
  AttachmentSupport = -> [Pad008]
  ExternalGeometry = -> [Binder]
  FullyConstrained = true
  MakeInternals = false
  MapMode = 5
  Placement = pos=(0,0.1,8e-16) rot=(0,0.707107,0.707107;3.14159rad)
  sketch-geometry (1):
    g0: GeomPoint X=197.47 Y=8.55923 Z=0
  constraints (1):
    c: Symmetric(g-7,g-5,g0)
FEATURE [PartDesign::Chamfer] Chamfer005
  Angle = 45
  Base = -> Pad009 [Edge215,Edge212]
  BaseFeature = -> Pad009
  ChamferType = 1
  FlipDirection = false
  Refine = true
  Size = 1.5
  Size2 = 2.8
  SupportTransform = false
  Suppressed = false
  UseAllEdges = false
FEATURE [Sketcher::SketchObject] Sketch111
  ArcFitTolerance = 1e-06
  AttachmentSupport = -> [Pad009]
  ExternalGeometry = -> [Pad009]
  FullyConstrained = true
  MakeInternals = false
  MapMode = 5
  Placement = pos=(0,3.6,-8e-16) rot=(0,0.707107,0.707107;3.14159rad)
  sketch-geometry (21):
    g0: LineSegment [constr] StartX=97 StartY=36.8 StartZ=0 EndX=97 EndY=26.8 EndZ=0
    g1: LineSegment StartX=97 StartY=28.6 StartZ=0 EndX=97 EndY=27.8 EndZ=0
    g2: LineSegment StartX=97 StartY=27.8 StartZ=0 EndX=108 EndY=27.8 EndZ=0
    g3: LineSegment StartX=108 StartY=27.8 StartZ=0 EndX=108 EndY=28.6 EndZ=0
    g4: LineSegment StartX=108 StartY=28.6 StartZ=0 EndX=97 EndY=28.6 EndZ=0
    g5: LineSegment StartX=97 StartY=35.8 StartZ=0 EndX=97 EndY=35 EndZ=0
    g6: LineSegment StartX=97 StartY=35 StartZ=0 EndX=108 EndY=35 EndZ=0
    g7: LineSegment StartX=108 StartY=35 StartZ=0 EndX=108 EndY=35.8 EndZ=0
    g8: LineSegment StartX=108 StartY=35.8 StartZ=0 EndX=97 EndY=35.8 EndZ=0
    g9: LineSegment StartX=97 StartY=30.4 StartZ=0 EndX=97 EndY=29.6 EndZ=0
    g10: LineSegment StartX=97 StartY=29.6 StartZ=0 EndX=108 EndY=29.6 EndZ=0
    g11: LineSegment StartX=108 StartY=29.6 StartZ=0 EndX=108 EndY=30.4 EndZ=0
    g12: LineSegment StartX=108 StartY=30.4 StartZ=0 EndX=97 EndY=30.4 EndZ=0
    g13: LineSegment StartX=97 StartY=34 StartZ=0 EndX=97 EndY=33.2 EndZ=0
    g14: LineSegment StartX=97 StartY=33.2 StartZ=0 EndX=108 EndY=33.2 EndZ=0
    g15: LineSegment StartX=108 StartY=33.2 StartZ=0 EndX=108 EndY=34 EndZ=0
    g16: LineSegment StartX=108 StartY=34 StartZ=0 EndX=97 EndY=34 EndZ=0
    g17: LineSegment StartX=97 StartY=32.2 StartZ=0 EndX=97 EndY=31.4 EndZ=0
    g18: LineSegment StartX=97 StartY=31.4 StartZ=0 EndX=108 EndY=31.4 EndZ=0
    g19: LineSegment StartX=108 StartY=31.4 StartZ=0 EndX=108 EndY=32.2 EndZ=0
    g20: LineSegment StartX=108 StartY=32.2 StartZ=0 EndX=97 EndY=32.2 EndZ=0
  constraints (54):
    c: Vertical(g0)
    c: PointOnObject(g0,g-3)
    c: PointOnObject(g0,g-4)
    c: DistanceX(g0,g-5) = 11
    c: Coincident(g1,g2)
    c: Coincident(g2,g3)
    c: Coincident(g3,g4)
    c: Coincident(g4,g1)
    c: Horizontal(g2)
    c: Horizontal(g4)
    c: Tangent(g1,g0)
    c: Tangent(g3,g-5)
    c: DistanceY(g2,g3) = 0.8
    c: Coincident(g5,g6)
    c: Coincident(g6,g7)
    c: Coincident(g7,g8)
    c: Coincident(g8,g5)
    c: Horizontal(g6)
    c: Horizontal(g8)
    c: DistanceY(g6,g7) = 0.8
    c: Coincident(g9,g10)
    c: Coincident(g10,g11)
    c: Coincident(g11,g12)
    c: Coincident(g12,g9)
    c: Horizontal(g10)
    c: Horizontal(g12)
    c: DistanceY(g10,g11) = 0.8
    c: Tangent(g5,g0)
    c: Tangent(g7,g-5)
    c: Tangent(g9,g0)
    c: Tangent(g11,g-5)
    c: Coincident(g13,g14)
    c: Coincident(g14,g15)
    c: Coincident(g15,g16)
    c: Coincident(g16,g13)
    c: Horizontal(g14)
    c: Horizontal(g16)
    c: DistanceY(g14,g15) = 0.8
    c: Tangent(g13,g0)
    c: Tangent(g15,g-5)
    c: Coincident(g17,g18)
    c: Coincident(g18,g19)
    c: Coincident(g19,g20)
    c: Coincident(g20,g17)
    c: Horizontal(g18)
    c: Horizontal(g20)
    c: DistanceY(g18,g19) = 0.8
    c: Tangent(g17,g0)
    c: Tangent(g19,g-5)
    c: DistanceY(g1,g9) = 1
    c: DistanceY(g9,g17) = 1
    c: DistanceY(g17,g13) = 1
    c: DistanceY(g13,g5) = 1
    c: DistanceY(g0,g1) = 1
FEATURE [PartDesign::Pocket] Pocket004
  BaseFeature = -> Chamfer005
  Direction = (0,-1,2e-16)
  Length = 1
  Length2 = 5
  Profile = -> Sketch111
  ReferenceAxis = -> Sketch111 [N_Axis]
  Refine = true
  Suppressed = false
  Type = 0
FEATURE [PartDesign::Pad] Pad010
  BaseFeature = -> Pocket004
  Direction = (0,1,-2e-16)
  Length = 1.2
  Length2 = 10
  Profile = -> Sketch098
  ReferenceAxis = -> Sketch098 [N_Axis]
  Refine = true
  Suppressed = false
  Type = 0
FEATURE [PartDesign::Chamfer] Chamfer006
  Angle = 45
  Base = -> Pad010 [Edge291]
  BaseFeature = -> Pad010
  ChamferType = 1
  FlipDirection = false
  Refine = true
  Size = 1
  Size2 = 6
  SupportTransform = false
  Suppressed = false
  UseAllEdges = false
FEATURE [Sketcher::SketchObject] Sketch110
  ArcFitTolerance = 1e-06
  AttachmentSupport = -> [Pad010]
  ExternalGeometry = -> [Sketch098]
  FullyConstrained = true
  MakeInternals = false
  MapMode = 5
  Placement = pos=(0,4,-9e-16) rot=(0,0.707107,0.707107;3.14159rad)
  sketch-geometry (8):
    g0: LineSegment StartX=119.69 StartY=34 StartZ=0 EndX=130.69 EndY=34 EndZ=0
    g1: LineSegment StartX=119.95 StartY=33.2 StartZ=0 EndX=130.95 EndY=33.2 EndZ=0
    g2: LineSegment StartX=119.137 StartY=35.7 StartZ=0 EndX=130.137 EndY=35.7 EndZ=0
    g3: LineSegment StartX=118.877 StartY=36.5 StartZ=0 EndX=129.877 EndY=36.5 EndZ=0
    g4: LineSegment StartX=118.877 StartY=36.5 StartZ=0 EndX=119.137 EndY=35.7 EndZ=0
    g5: LineSegment StartX=129.877 StartY=36.5 StartZ=0 EndX=130.137 EndY=35.7 EndZ=0
    g6: LineSegment StartX=119.69 StartY=34 StartZ=0 EndX=119.95 EndY=33.2 EndZ=0
    g7: LineSegment StartX=130.69 StartY=34 StartZ=0 EndX=130.95 EndY=33.2 EndZ=0
  constraints (24):
    c: Horizontal(g0)
    c: Horizontal(g1)
    c: Horizontal(g2)
    c: Horizontal(g3)
    c: Equal(g1,g-5)
    c: Equal(g0,g-5)
    c: Equal(g2,g-5)
    c: Equal(g3,g-5)
    c: PointOnObject(g0,g-3)
    c: PointOnObject(g1,g-3)
    c: PointOnObject(g2,g-3)
    c: PointOnObject(g3,g-3)
    c: Coincident(g4,g3)
    c: Coincident(g4,g2)
    c: Coincident(g5,g3)
    c: Coincident(g5,g2)
    c: Coincident(g6,g0)
    c: Coincident(g6,g1)
    c: Coincident(g7,g0)
    c: Coincident(g7,g1)
    c: DistanceY(g1,g0) = 0.8
    c: DistanceY(g2,g3) = 0.8
    c: DistanceY(g-5,g1) = 2
    c: DistanceY(g-5,g2) = 4.5
FEATURE [PartDesign::Pocket] Pocket003
  BaseFeature = -> Chamfer006
  Direction = (0,-1,2e-16)
  Length = 1
  Length2 = 5
  Profile = -> Sketch110
  ReferenceAxis = -> Sketch110 [N_Axis]
  Refine = true
  Suppressed = false
  Type = 0
FEATURE [PartDesign::SubtractivePipe] SubtractivePipe
  AuxilleryCurvelinear = true
  AuxillerySpineTangent = false
  BaseFeature = -> Pocket003
  Binormal = (0,0,0)
  Mode = 0
  Profile = -> Sketch106
  Refine = true
  Spine = -> Pad008 [Edge215]
  SpineTangent = false
  Suppressed = false
  Transformation = 0
  Transition = 0
FEATURE [PartDesign::SubtractivePipe] SubtractivePipe001
  AuxilleryCurvelinear = true
  AuxillerySpineTangent = false
  BaseFeature = -> SubtractivePipe
  Binormal = (0,0,0)
  Mode = 0
  Profile = -> Sketch107
  Refine = true
  Spine = -> Pad008 [Edge213,Edge216,Edge210]
  SpineTangent = false
  Suppressed = false
  Transformation = 0
  Transition = 0
FEATURE [PartDesign::SubtractiveLoft] SubtractiveLoft
  BaseFeature = -> SubtractivePipe001
  Closed = false
  Profile = -> Sketch099
  Refine = true
  Ruled = false
  Sections = -> [Sketch108]
  Suppressed = false
FEATURE [PartDesign::SubtractiveLoft] SubtractiveLoft001
  BaseFeature = -> SubtractiveLoft
  Closed = false
  Profile = -> Clone2D
  Refine = true
  Ruled = false
  Sections = -> [Sketch109]
  Suppressed = false
FEATURE [Sketcher::SketchObject] Sketch112
  ArcFitTolerance = 1e-06
  AttachmentSupport = -> [Pad008]
  ExternalGeometry = -> [Binder]
  FullyConstrained = true
  MakeInternals = false
  MapMode = 5
  Placement = pos=(0,3.6,0) rot=(0,0.707107,0.707107;3.14159rad)
  sketch-geometry (4):
    g0: LineSegment [constr] StartX=167.782 StartY=-53.0314 StartZ=0 EndX=215.42 EndY=-53.0314 EndZ=0
    g1: GeomPoint [constr] X=191.282 Y=-53.0314 Z=0
    g2: Circle CenterX=191.282 CenterY=-53.0314 CenterZ=0 NormalX=0 NormalY=0 NormalZ=1 AngleXU=0 Radius=11.5
    g3: Circle CenterX=191.282 CenterY=-53.0314 CenterZ=0 NormalX=0 NormalY=0 NormalZ=1 AngleXU=0 Radius=10.7
  constraints (9):
    c: Horizontal(g0)
    c: PointOnObject(g0,g-3)
    c: Diameter(g2) = 23
    c: Coincident(g2,g1)
    c: Diameter(g3) = 21.4
    c: Coincident(g3,g1)
    c: DistanceX(g0,g1) = 23.5
    c: PointOnObject(g1,g0)
    c: Coincident(g0,g-4)
FEATURE [PartDesign::Chamfer] Chamfer016
  Angle = 45
  Base = -> SubtractiveLoft001 [Edge118,Edge117,Edge119,Edge120,Edge109]
  BaseFeature = -> SubtractiveLoft001
  ChamferType = 0
  FlipDirection = false
  Refine = true
  Size = 1.5
  Size2 = 1
  SupportTransform = false
  Suppressed = false
  UseAllEdges = false
FEATURE [PartDesign::Chamfer] Chamfer017
  Angle = 45
  Base = -> Chamfer016 [Edge15]
  BaseFeature = -> Chamfer016
  ChamferType = 0
  FlipDirection = false
  Refine = true
  Size = 1.6
  Size2 = 1
  SupportTransform = false
  Suppressed = false
  UseAllEdges = false
FEATURE [PartDesign::Chamfer] Chamfer018
  Angle = 45
  Base = -> Chamfer017 [Edge10]
  BaseFeature = -> Chamfer017
  ChamferType = 0
  FlipDirection = false
  Refine = true
  Size = 3.5
  Size2 = 1
  SupportTransform = false
  Suppressed = false
  UseAllEdges = false
FEATURE [PartDesign::Chamfer] Chamfer019
  Angle = 45
  Base = -> Chamfer018 [Edge94,Edge199]
  BaseFeature = -> Chamfer018
  ChamferType = 0
  FlipDirection = false
  Refine = true
  Size = 1.9
  Size2 = 1
  SupportTransform = false
  Suppressed = false
  UseAllEdges = false
FEATURE [PartDesign::Fillet] Fillet009
  Base = -> Chamfer019 [Edge83]
  BaseFeature = -> Chamfer019
  Radius = 1.1
  Refine = true
  SupportTransform = false
  Suppressed = false
  UseAllEdges = false
FEATURE [PartDesign::Fillet] Fillet010
  Base = -> Fillet009 [Edge77]
  BaseFeature = -> Fillet009
  Radius = 1.9
  Refine = true
  SupportTransform = false
  Suppressed = false
  UseAllEdges = false
FEATURE [PartDesign::Pocket] Pocket005
  BaseFeature = -> Fillet010
  Direction = (0,-1,2e-16)
  Length = 0.8
  Length2 = 5
  Profile = -> Sketch112
  ReferenceAxis = -> Sketch112 [N_Axis]
  Refine = true
  Suppressed = false
  Type = 0
FEATURE [Part::Part2DObjectPython] ShapeString001  # Draft 2D object (typed FeaturePython)
  FontFile = <path>
  Fuse = false
  Justification = 6
  JustificationReference = 0
  KeepLeftMargin = false
  MakeFace = true
  ObliqueAngle = 0
  Placement = pos=(-183.5,3.6,-57.5) rot=(0,0.707107,0.707107;3.14159rad)
  ScaleToSize = true
  Size = 10
  String = AS
  Tracking = 0
FEATURE [PartDesign::Pocket] Pocket013
  BaseFeature = -> Pocket005
  Direction = (-1e-16,-1,2e-16)
  Length = 1
  Length2 = 5
  Profile = -> ShapeString001
  ReferenceAxis = -> ShapeString001 [N_Axis]
  Refine = true
  Suppressed = false
  Type = 0
FEATURE [PartDesign::Body] Body006  label="lato SX"
  AllowCompound = false
  Group = -> [Binder,Pad019,Chamfer015,Pocket002,Sketch133,Sketch091,Pad005,Sketch092,Pocket001,Sketch093,Sketch094,Pad006,Sketch095,Pad007,Sketch096,Pad008,Sketch097,Pad009,Chamfer005,Pocket004,Sketch098,Pad010,Chamfer006,Pocket003,SubtractivePipe,SubtractivePipe001,Sketch099,Sketch106,Sketch107,Sketch108,Clone2D,Sketch109,SubtractiveLoft,SubtractiveLoft001,Sketch110,Sketch111,Sketch112,Chamfer016,Chamfer017,+7 more]
  Origin = -> Origin006
  Tip = -> Pocket013
FEATURE [PartDesign::Pad] Pad020
  Direction = (0,-1,2e-16)
  Length = 25.2
  Length2 = 10
  Midplane = true
  Placement = pos=(0,0,0) rot=(1,0,0;1.5708rad)
  Profile = -> Sketch021
  ReferenceAxis = -> Sketch021 [N_Axis]
  Refine = true
  Suppressed = false
  Type = 0
FEATURE [PartDesign::Body] Body001  label="perno fermo rumble e driver solenoide"
  AllowCompound = false
  Group = -> [Sketch021,Pad020]
  Origin = -> Origin001
  Tip = -> Pad020
FEATURE [PartDesign::Pad] Pad021
  Direction = (0,-1,2e-16)
  Length = 16.8
  Length2 = 10
  Midplane = true
  Placement = pos=(0,0,0) rot=(1,0,0;1.5708rad)
  Profile = -> Sketch061
  ReferenceAxis = -> Sketch061 [N_Axis]
  Refine = true
  Suppressed = false
  Type = 0
FEATURE [PartDesign::Pocket] Pocket014
  BaseFeature = -> Pad021
  Direction = (0,1,-2e-16)
  Length = 12.8
  Length2 = 5
  Midplane = true
  Placement = pos=(0,0,0) rot=(1,0,0;1.5708rad)
  Profile = -> Sketch062
  ReferenceAxis = -> Sketch062 [N_Axis]
  Refine = true
  Suppressed = false
  Type = 0
FEATURE [PartDesign::Pad] Pad022
  BaseFeature = -> Pocket014
  Direction = (0,-1,2e-16)
  Length = 7.6
  Length2 = 10
  Midplane = true
  Placement = pos=(0,0,0) rot=(1,0,0;1.5708rad)
  Profile = -> Sketch063
  ReferenceAxis = -> Sketch063 [N_Axis]
  Refine = true
  Suppressed = false
  Type = 0
FEATURE [PartDesign::Body] Body003  label="blocco switch"
  AllowCompound = false
  Group = -> [Sketch061,Sketch062,Sketch063,Pad021,Pocket014,Pad022]
  Origin = -> Origin003
  Tip = -> Pad022
FEATURE [PartDesign::Pad] Pad024
  Direction = (0,-1,2e-16)
  Length = 17
  Length2 = 10
  Midplane = true
  Placement = pos=(0,0,0) rot=(1,0,0;1.5708rad)
  Profile = -> Sketch045
  ReferenceAxis = -> Sketch045 [N_Axis]
  Refine = true
  Suppressed = false
  Type = 0
FEATURE [PartDesign::Pocket] Pocket015
  BaseFeature = -> Pad024
  Direction = (-1,0,0)
  Length = 8
  Length2 = 5
  Placement = pos=(0,0,0) rot=(1,0,0;1.5708rad)
  Profile = -> Sketch047
  ReferenceAxis = -> Sketch047 [N_Axis]
  Refine = true
  Reversed = true
  Suppressed = false
  Type = 0
FEATURE [PartDesign::Pocket] Pocket016
  BaseFeature = -> Pocket015
  Direction = (-1,0,0)
  Length = 1
  Length2 = 5
  Placement = pos=(0,0,0) rot=(1,0,0;1.5708rad)
  Profile = -> Sketch046
  ReferenceAxis = -> Sketch046 [N_Axis]
  Refine = true
  Reversed = true
  Suppressed = false
  Type = 0
FEATURE [PartDesign::Pocket] Pocket017
  BaseFeature = -> Pocket016
  Direction = (0,1,-2e-16)
  Length = 17
  Length2 = 5
  Midplane = true
  Placement = pos=(0,0,0) rot=(1,0,0;1.5708rad)
  Profile = -> Sketch048
  ReferenceAxis = -> Sketch048 [N_Axis]
  Refine = true
  Suppressed = false
  Type = 0
FEATURE [PartDesign::Pad] Pad025
  BaseFeature = -> Pocket017
  Direction = (0,-1,2e-16)
  Length = 17
  Length2 = 10
  Midplane = true
  Placement = pos=(0,0,0) rot=(1,0,0;1.5708rad)
  Profile = -> Sketch049
  ReferenceAxis = -> Sketch049 [N_Axis]
  Refine = true
  Suppressed = false
  Type = 0
FEATURE [PartDesign::Pad] Pad026
  BaseFeature = -> Pad025
  Direction = (0,-1,2e-16)
  Length = 17
  Length2 = 10
  Midplane = true
  Placement = pos=(0,0,0) rot=(1,0,0;1.5708rad)
  Profile = -> Sketch066
  ReferenceAxis = -> Sketch066 [N_Axis]
  Refine = true
  Suppressed = false
  Type = 0
FEATURE [PartDesign::Pad] Pad027
  BaseFeature = -> Pad026
  Direction = (0,-1,2e-16)
  Length = 5
  Length2 = 10
  Midplane = true
  Placement = pos=(0,0,0) rot=(1,0,0;1.5708rad)
  Profile = -> Sketch064
  ReferenceAxis = -> Sketch064 [N_Axis]
  Refine = true
  Suppressed = false
  Type = 0
FEATURE [PartDesign::Pad] Pad028
  BaseFeature = -> Pad027
  Direction = (1,0,0)
  Length = 1
  Length2 = 10
  Placement = pos=(0,0,0) rot=(1,0,0;1.5708rad)
  Profile = -> Sketch068
  ReferenceAxis = -> Sketch068 [N_Axis]
  Refine = true
  Reversed = true
  Suppressed = false
  Type = 0
FEATURE [PartDesign::Chamfer] Chamfer020
  Angle = 45
  Base = -> Pad028 [Edge73,Edge75,Edge78,Edge77]
  BaseFeature = -> Pad028
  ChamferType = 0
  FlipDirection = false
  Placement = pos=(0,0,0) rot=(1,0,0;1.5708rad)
  Refine = true
  Size = 0.5
  Size2 = 1
  SupportTransform = false
  Suppressed = false
  UseAllEdges = false
FEATURE [PartDesign::Body] Body002  label="supporto per neopixel"
  AllowCompound = false
  Group = -> [Sketch045,Sketch047,Sketch046,Sketch048,Sketch049,Sketch066,Sketch064,Sketch068,Pad024,Pocket015,Pocket016,Pocket017,Pad025,Pad026,Pad027,Pad028,Chamfer020]
  Origin = -> Origin002
  Tip = -> Chamfer020
FEATURE [Sketcher::SketchObject] Sketch134  label="perno fermo rumble002"
  ArcFitTolerance = 1e-06
  AttachmentSupport = -> [XZ_Plane008]
  FullyConstrained = true
  MakeInternals = false
  MapMode = 5
  Placement = pos=(0,0,0) rot=(1,0,0;1.5708rad)
  sketch-geometry (16):
    g0: LineSegment StartX=0 StartY=0.45 StartZ=0 EndX=0 EndY=1.55 EndZ=0
    g1: LineSegment StartX=0.45 StartY=2 StartZ=0 EndX=1.55 EndY=2 EndZ=0
    g2: LineSegment StartX=2 StartY=1.55 StartZ=0 EndX=2 EndY=0.45 EndZ=0
    g3: LineSegment StartX=1.55 StartY=0 StartZ=0 EndX=0.45 EndY=0 EndZ=0
    g4: ArcOfCircle [constr] CenterX=0.45 CenterY=1.55 CenterZ=0 NormalX=0 NormalY=0 NormalZ=1 AngleXU=0 Radius=0.45 StartAngle=1.5708 EndAngle=3.14159
    g5: GeomPoint [constr] X=0 Y=2 Z=0
    g6: LineSegment StartX=0.45 StartY=2 StartZ=0 EndX=0 EndY=1.55 EndZ=0
    g7: ArcOfCircle [constr] CenterX=1.55 CenterY=1.55 CenterZ=0 NormalX=0 NormalY=0 NormalZ=1 AngleXU=0 Radius=0.45 StartAngle=0 EndAngle=1.5708
    g8: GeomPoint [constr] X=2 Y=2 Z=0
    g9: LineSegment StartX=2 StartY=1.55 StartZ=0 EndX=1.55 EndY=2 EndZ=0
    g10: ArcOfCircle [constr] CenterX=1.55 CenterY=0.45 CenterZ=0 NormalX=0 NormalY=0 NormalZ=1 AngleXU=0 Radius=0.45 StartAngle=4.71239 EndAngle=6.28319
    g11: GeomPoint [constr] X=2 Y=0 Z=0
    g12: LineSegment StartX=1.55 StartY=0 StartZ=0 EndX=2 EndY=0.45 EndZ=0
    g13: ArcOfCircle [constr] CenterX=0.45 CenterY=0.45 CenterZ=0 NormalX=0 NormalY=0 NormalZ=1 AngleXU=0 Radius=0.45 StartAngle=3.14159 EndAngle=4.71239
    g14: GeomPoint [constr] X=0 Y=0 Z=0
    g15: LineSegment StartX=0 StartY=0.45 StartZ=0 EndX=0.45 EndY=0 EndZ=0
  constraints (35):
    c: Coincident(g14,g-1)
    c: PointOnObject(g5,g-2)
    c: Horizontal(g1)
    c: Vertical(g2)
    c: Horizontal(g3)
    c: DistanceX(g5,g8) = 2
    c: DistanceY(g11,g8) = 2
    c: PointOnObject(g5,g0)
    c: PointOnObject(g5,g1)
    c: Tangent(g0,g4) = 1.5708
    c: Tangent(g1,g4) = 1.5708
    c: Coincident(g6,g0)
    c: Coincident(g6,g1)
    c: PointOnObject(g8,g2)
    c: PointOnObject(g8,g1)
    c: Tangent(g2,g7) = 1.5708
    c: Tangent(g1,g7) = 1.5708
    c: Coincident(g9,g2)
    c: Coincident(g9,g1)
    c: PointOnObject(g11,g2)
    c: PointOnObject(g11,g3)
    c: Tangent(g2,g10) = 1.5708
    c: Tangent(g3,g10) = 1.5708
    c: Coincident(g12,g2)
    c: Coincident(g12,g3)
    c: PointOnObject(g14,g0)
    c: PointOnObject(g14,g3)
    c: Tangent(g0,g13) = 1.5708
    c: Tangent(g3,g13) = 1.5708
    c: Coincident(g15,g0)
    c: Coincident(g15,g3)
    c: Equal(g6,g9)
    c: Equal(g9,g12)
    c: Equal(g12,g15)
    c: DistanceX(g14,g3) = 0.45
FEATURE [PartDesign::Pad] Pad029
  Direction = (0,-1,2e-16)
  Length = 17
  Length2 = 10
  Midplane = true
  Placement = pos=(0,0,0) rot=(1,0,0;1.5708rad)
  Profile = -> Sketch134
  ReferenceAxis = -> Sketch134 [N_Axis]
  Refine = true
  Suppressed = false
  Type = 0
FEATURE [PartDesign::Body] Body008  label="perno fermo neopixel"
  AllowCompound = false
  Group = -> [Sketch134,Pad029]
  Origin = -> Origin008
  Tip = -> Pad029
FEATURE [Sketcher::SketchObject] Sketch135  label="perno fermo rumble003"
  ArcFitTolerance = 1e-06
  AttachmentSupport = -> [XZ_Plane009]
  FullyConstrained = true
  MakeInternals = false
  MapMode = 5
  Placement = pos=(0,0,0) rot=(1,0,0;1.5708rad)
  sketch-geometry (16):
    g0: LineSegment StartX=4.69e-14 StartY=0.8 StartZ=0 EndX=-3.04e-14 EndY=3.1 EndZ=0
    g1: LineSegment StartX=0.8 StartY=3.9 StartZ=0 EndX=3.1 EndY=3.9 EndZ=0
    g2: LineSegment StartX=3.9 StartY=3.1 StartZ=0 EndX=3.9 EndY=0.8 EndZ=0
    g3: LineSegment StartX=3.1 StartY=0 StartZ=0 EndX=0.8 EndY=0 EndZ=0
    g4: ArcOfCircle [constr] CenterX=0.8 CenterY=3.1 CenterZ=0 NormalX=0 NormalY=0 NormalZ=1 AngleXU=0 Radius=0.8 StartAngle=1.5708 EndAngle=3.14159
    g5: GeomPoint [constr] X=0 Y=3.9 Z=0
    g6: LineSegment StartX=0.8 StartY=3.9 StartZ=0 EndX=-3.04e-14 EndY=3.1 EndZ=0
    g7: ArcOfCircle [constr] CenterX=3.1 CenterY=3.1 CenterZ=0 NormalX=0 NormalY=0 NormalZ=1 AngleXU=0 Radius=0.8 StartAngle=-2.4e-14 EndAngle=1.5708
    g8: GeomPoint [constr] X=3.9 Y=3.9 Z=0
    g9: LineSegment StartX=3.9 StartY=3.1 StartZ=0 EndX=3.1 EndY=3.9 EndZ=0
    g10: ArcOfCircle [constr] CenterX=3.1 CenterY=0.8 CenterZ=0 NormalX=0 NormalY=0 NormalZ=1 AngleXU=0 Radius=0.8 StartAngle=4.71239 EndAngle=6.28319
    g11: GeomPoint [constr] X=3.9 Y=0 Z=0
    g12: LineSegment StartX=3.1 StartY=0 StartZ=0 EndX=3.9 EndY=0.8 EndZ=0
    g13: ArcOfCircle [constr] CenterX=0.8 CenterY=0.8 CenterZ=0 NormalX=0 NormalY=0 NormalZ=1 AngleXU=0 Radius=0.8 StartAngle=3.14159 EndAngle=4.71239
    g14: GeomPoint [constr] X=0 Y=0 Z=0
    g15: LineSegment StartX=4.69e-14 StartY=0.8 StartZ=0 EndX=0.8 EndY=0 EndZ=0
  constraints (35):
    c: Coincident(g14,g-1)
    c: PointOnObject(g5,g-2)
    c: Horizontal(g1)
    c: Vertical(g2)
    c: Horizontal(g3)
    c: DistanceX(g5,g8) = 3.9
    c: DistanceY(g11,g8) = 3.9
    c: PointOnObject(g5,g0)
    c: PointOnObject(g5,g1)
    c: Tangent(g0,g4) = 1.5708
    c: Tangent(g1,g4) = 1.5708
    c: Coincident(g6,g0)
    c: Coincident(g6,g1)
    c: PointOnObject(g8,g2)
    c: PointOnObject(g8,g1)
    c: Tangent(g2,g7) = 1.5708
    c: Tangent(g1,g7) = 1.5708
    c: Coincident(g9,g2)
    c: Coincident(g9,g1)
    c: PointOnObject(g11,g2)
    c: PointOnObject(g11,g3)
    c: Tangent(g2,g10) = 1.5708
    c: Tangent(g3,g10) = 1.5708
    c: Coincident(g12,g2)
    c: Coincident(g12,g3)
    c: PointOnObject(g14,g0)
    c: PointOnObject(g14,g3)
    c: Tangent(g0,g13) = 1.5708
    c: Tangent(g3,g13) = 1.5708
    c: Coincident(g15,g0)
    c: Coincident(g15,g3)
    c: Equal(g6,g9)
    c: Equal(g9,g12)
    c: Equal(g12,g15)
    c: DistanceX(g14,g3) = 0.8
FEATURE [PartDesign::Pad] Pad030
  Direction = (0,-1,2e-16)
  Length = 25.2
  Length2 = 10
  Midplane = true
  Placement = pos=(0,0,0) rot=(1,0,0;1.5708rad)
  Profile = -> Sketch135
  ReferenceAxis = -> Sketch135 [N_Axis]
  Refine = true
  Suppressed = false
  Type = 0
FEATURE [PartDesign::Body] Body009  label="perno fermo switch - caricabatterie - grilletto"
  AllowCompound = false
  Group = -> [Sketch135,Pad030]
  Origin = -> Origin009
  Tip = -> Pad030
note: 2 file-system paths scrubbed to <path> (originals preserved in the JSON sidecar)
